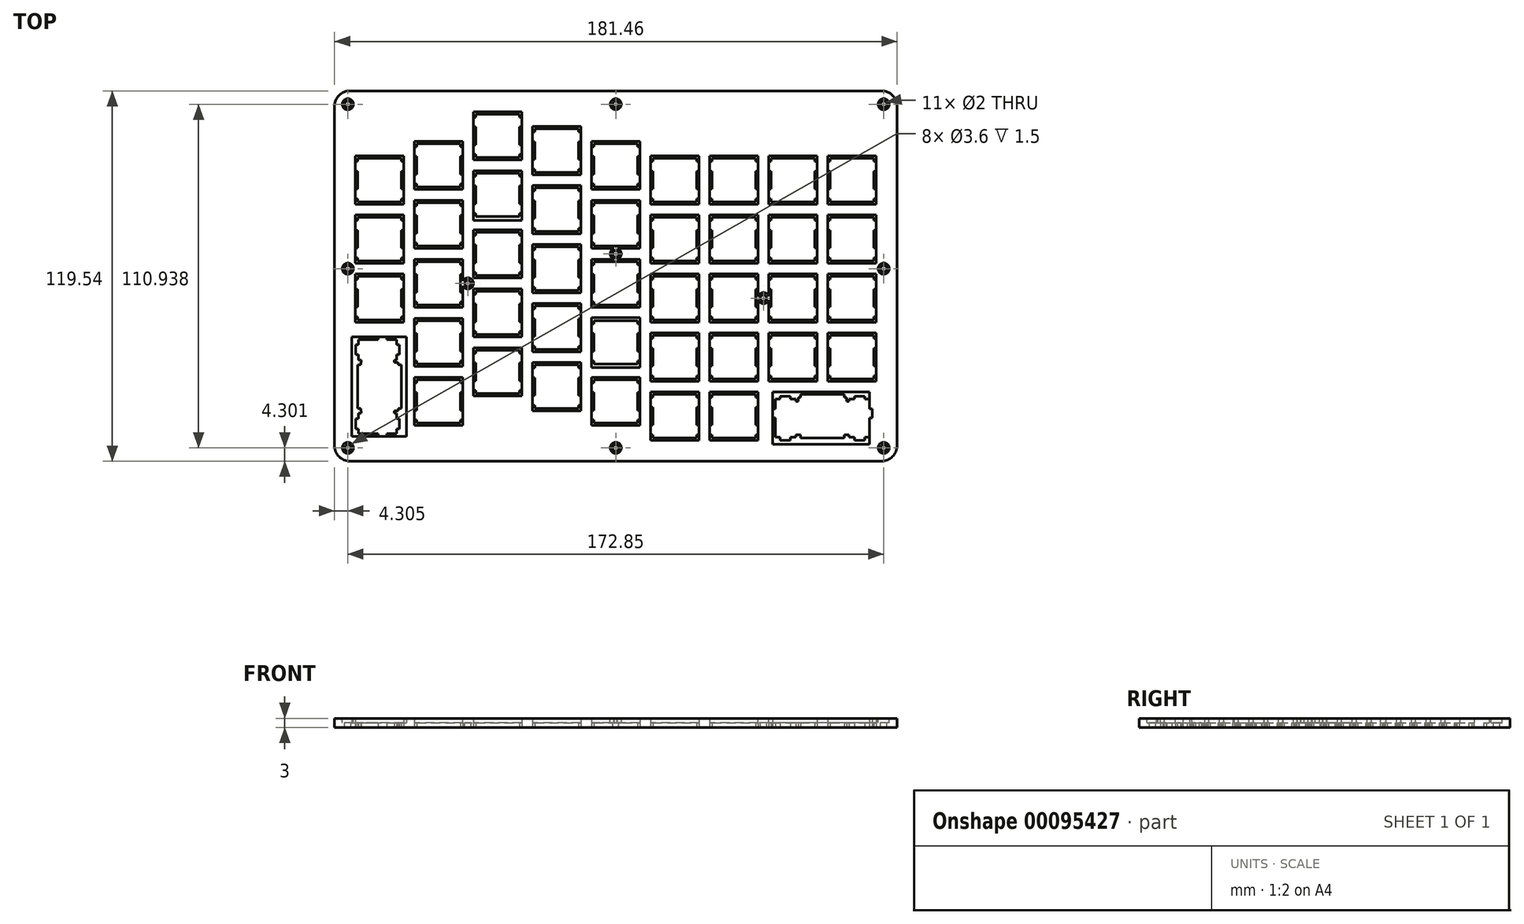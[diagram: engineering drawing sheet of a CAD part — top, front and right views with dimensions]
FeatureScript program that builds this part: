
annotation { "Feature Type Name" : "Feature", "Feature Type Description" : "" }
export const myFeature = defineFeature(function(context is Context, id is Id, definition is map)
    precondition{}
    {
        {
            var Q0;
            Q0=qCreatedBy(makeId("Top.planeOp"),FACE);
            var sketch = newSketch(context, id + "F0", { "sketchPlane" : qUnion([Q0])});
            skLineSegment(sketch, "E0", {"start": v(-90.73, 59.77) * mm, "end": v(90.73, 59.77) * mm});
            skLineSegment(sketch, "E1", {"start": v(90.73, 59.77) * mm, "end": v(90.73, -59.77) * mm});
            skLineSegment(sketch, "E2", {"start": v(90.73, -59.77) * mm, "end": v(-90.73, -59.77) * mm});
            skLineSegment(sketch, "E3", {"start": v(-90.73, -59.77) * mm, "end": v(-90.73, 59.77) * mm});
            skLineSegment(sketch, "E4", {"start": v(-70.2, -42.72) * mm, "end": v(-70.2, -43.52) * mm});
            skLineSegment(sketch, "E5", {"start": v(-70.2, -43.52) * mm, "end": v(-71.47, -43.52) * mm});
            skLineSegment(sketch, "E6", {"start": v(-71.47, -43.52) * mm, "end": v(-71.47, -44.3) * mm});
            skLineSegment(sketch, "E7", {"start": v(-71.47, -44.3) * mm, "end": v(-70.67, -44.3) * mm});
            skLineSegment(sketch, "E8", {"start": v(-70.67, -44.3) * mm, "end": v(-70.67, -46.02) * mm});
            skLineSegment(sketch, "E9", {"start": v(-70.67, -46.02) * mm, "end": v(-69.75, -46.02) * mm});
            skLineSegment(sketch, "E10", {"start": v(-69.75, -46.02) * mm, "end": v(-69.75, -49.32) * mm});
            skLineSegment(sketch, "E11", {"start": v(-69.75, -49.32) * mm, "end": v(-70.67, -49.32) * mm});
            skLineSegment(sketch, "E12", {"start": v(-70.67, -49.32) * mm, "end": v(-70.67, -50.94) * mm});
            skLineSegment(sketch, "E13", {"start": v(-70.67, -50.94) * mm, "end": v(-73.9, -50.94) * mm});
            skLineSegment(sketch, "E14", {"start": v(-73.9, -50.94) * mm, "end": v(-73.9, -51.82) * mm});
            skLineSegment(sketch, "E15", {"start": v(-73.9, -51.82) * mm, "end": v(-76.7, -51.82) * mm});
            skLineSegment(sketch, "E16", {"start": v(-76.7, -51.82) * mm, "end": v(-76.7, -50.94) * mm});
            skLineSegment(sketch, "E17", {"start": v(-76.7, -50.94) * mm, "end": v(-82.97, -50.94) * mm});
            skLineSegment(sketch, "E18", {"start": v(-82.97, -50.94) * mm, "end": v(-82.97, -49.32) * mm});
            skLineSegment(sketch, "E19", {"start": v(-82.97, -49.32) * mm, "end": v(-83.95, -49.32) * mm});
            skLineSegment(sketch, "E20", {"start": v(-83.95, -49.32) * mm, "end": v(-83.95, -46.02) * mm});
            skLineSegment(sketch, "E21", {"start": v(-83.95, -46.02) * mm, "end": v(-82.97, -46.02) * mm});
            skLineSegment(sketch, "E22", {"start": v(-82.97, -46.02) * mm, "end": v(-82.97, -44.3) * mm});
            skLineSegment(sketch, "E23", {"start": v(-82.97, -44.3) * mm, "end": v(-82.17, -44.3) * mm});
            skLineSegment(sketch, "E24", {"start": v(-82.17, -44.3) * mm, "end": v(-82.17, -43.52) * mm});
            skLineSegment(sketch, "E25", {"start": v(-82.17, -43.52) * mm, "end": v(-82.2, -43.52) * mm});
            skLineSegment(sketch, "E26", {"start": v(-82.2, -43.52) * mm, "end": v(-82.2, -42.72) * mm});
            skLineSegment(sketch, "E27", {"start": v(-82.2, -42.72) * mm, "end": v(-83.2, -42.72) * mm});
            skLineSegment(sketch, "E28", {"start": v(-83.2, -42.72) * mm, "end": v(-83.2, -28.72) * mm});
            skLineSegment(sketch, "E29", {"start": v(-83.2, -28.72) * mm, "end": v(-82.2, -28.72) * mm});
            skLineSegment(sketch, "E30", {"start": v(-82.2, -28.72) * mm, "end": v(-82.2, -27.92) * mm});
            skLineSegment(sketch, "E31", {"start": v(-82.2, -27.92) * mm, "end": v(-82.17, -27.92) * mm});
            skLineSegment(sketch, "E32", {"start": v(-82.17, -27.92) * mm, "end": v(-82.17, -27.14) * mm});
            skLineSegment(sketch, "E33", {"start": v(-82.17, -27.14) * mm, "end": v(-82.97, -27.14) * mm});
            skLineSegment(sketch, "E34", {"start": v(-82.97, -27.14) * mm, "end": v(-82.97, -25.42) * mm});
            skLineSegment(sketch, "E35", {"start": v(-82.97, -25.42) * mm, "end": v(-83.95, -25.42) * mm});
            skLineSegment(sketch, "E36", {"start": v(-83.95, -25.42) * mm, "end": v(-83.95, -22.12) * mm});
            skLineSegment(sketch, "E37", {"start": v(-83.95, -22.12) * mm, "end": v(-82.97, -22.12) * mm});
            skLineSegment(sketch, "E38", {"start": v(-82.97, -22.12) * mm, "end": v(-82.97, -20.5) * mm});
            skLineSegment(sketch, "E39", {"start": v(-82.97, -20.5) * mm, "end": v(-76.7, -20.5) * mm});
            skLineSegment(sketch, "E40", {"start": v(-76.7, -20.5) * mm, "end": v(-76.7, -19.62) * mm});
            skLineSegment(sketch, "E41", {"start": v(-76.7, -19.62) * mm, "end": v(-73.9, -19.62) * mm});
            skLineSegment(sketch, "E42", {"start": v(-73.9, -19.62) * mm, "end": v(-73.9, -20.5) * mm});
            skLineSegment(sketch, "E43", {"start": v(-73.9, -20.5) * mm, "end": v(-70.67, -20.5) * mm});
            skLineSegment(sketch, "E44", {"start": v(-70.67, -20.5) * mm, "end": v(-70.67, -22.12) * mm});
            skLineSegment(sketch, "E45", {"start": v(-70.67, -22.12) * mm, "end": v(-69.75, -22.12) * mm});
            skLineSegment(sketch, "E46", {"start": v(-69.75, -22.12) * mm, "end": v(-69.75, -25.42) * mm});
            skLineSegment(sketch, "E47", {"start": v(-69.75, -25.42) * mm, "end": v(-70.67, -25.42) * mm});
            skLineSegment(sketch, "E48", {"start": v(-70.67, -25.42) * mm, "end": v(-70.67, -27.14) * mm});
            skLineSegment(sketch, "E49", {"start": v(-70.67, -27.14) * mm, "end": v(-71.47, -27.14) * mm});
            skLineSegment(sketch, "E50", {"start": v(-71.47, -27.14) * mm, "end": v(-71.47, -27.92) * mm});
            skLineSegment(sketch, "E51", {"start": v(-71.47, -27.92) * mm, "end": v(-70.2, -27.92) * mm});
            skLineSegment(sketch, "E52", {"start": v(-70.2, -27.92) * mm, "end": v(-70.2, -28.72) * mm});
            skLineSegment(sketch, "E53", {"start": v(-70.2, -28.72) * mm, "end": v(-69.2, -28.72) * mm});
            skLineSegment(sketch, "E54", {"start": v(-69.2, -28.72) * mm, "end": v(-69.2, -42.72) * mm});
            skLineSegment(sketch, "E55", {"start": v(-69.2, -42.72) * mm, "end": v(-70.2, -42.72) * mm});
            skLineSegment(sketch, "E56", {"start": v(-69.2, 24.96) * mm, "end": v(-69.2, 23.96) * mm});
            skLineSegment(sketch, "E57", {"start": v(-69.2, 23.96) * mm, "end": v(-83.2, 23.96) * mm});
            skLineSegment(sketch, "E58", {"start": v(-83.2, 23.96) * mm, "end": v(-83.2, 24.96) * mm});
            skLineSegment(sketch, "E59", {"start": v(-83.2, 24.96) * mm, "end": v(-84, 24.96) * mm});
            skLineSegment(sketch, "E60", {"start": v(-84, 24.96) * mm, "end": v(-84, 28.06) * mm});
            skLineSegment(sketch, "E61", {"start": v(-84, 28.06) * mm, "end": v(-83.2, 28.06) * mm});
            skLineSegment(sketch, "E62", {"start": v(-83.2, 28.06) * mm, "end": v(-83.2, 33.86) * mm});
            skLineSegment(sketch, "E63", {"start": v(-83.2, 33.86) * mm, "end": v(-84, 33.86) * mm});
            skLineSegment(sketch, "E64", {"start": v(-84, 33.86) * mm, "end": v(-84, 36.96) * mm});
            skLineSegment(sketch, "E65", {"start": v(-84, 36.96) * mm, "end": v(-83.2, 36.96) * mm});
            skLineSegment(sketch, "E66", {"start": v(-83.2, 36.96) * mm, "end": v(-83.2, 37.96) * mm});
            skLineSegment(sketch, "E67", {"start": v(-83.2, 37.96) * mm, "end": v(-69.2, 37.96) * mm});
            skLineSegment(sketch, "E68", {"start": v(-69.2, 37.96) * mm, "end": v(-69.2, 36.96) * mm});
            skLineSegment(sketch, "E69", {"start": v(-69.2, 36.96) * mm, "end": v(-68.4, 36.96) * mm});
            skLineSegment(sketch, "E70", {"start": v(-68.4, 36.96) * mm, "end": v(-68.4, 33.86) * mm});
            skLineSegment(sketch, "E71", {"start": v(-68.4, 33.86) * mm, "end": v(-69.2, 33.86) * mm});
            skLineSegment(sketch, "E72", {"start": v(-69.2, 33.86) * mm, "end": v(-69.2, 28.06) * mm});
            skLineSegment(sketch, "E73", {"start": v(-69.2, 28.06) * mm, "end": v(-68.4, 28.06) * mm});
            skLineSegment(sketch, "E74", {"start": v(-68.4, 28.06) * mm, "end": v(-68.4, 24.96) * mm});
            skLineSegment(sketch, "E75", {"start": v(-68.4, 24.96) * mm, "end": v(-69.2, 24.96) * mm});
            skLineSegment(sketch, "E76", {"start": v(-69.2, 5.9) * mm, "end": v(-69.2, 4.9) * mm});
            skLineSegment(sketch, "E77", {"start": v(-69.2, 4.9) * mm, "end": v(-83.2, 4.9) * mm});
            skLineSegment(sketch, "E78", {"start": v(-83.2, 4.9) * mm, "end": v(-83.2, 5.9) * mm});
            skLineSegment(sketch, "E79", {"start": v(-83.2, 5.9) * mm, "end": v(-84, 5.9) * mm});
            skLineSegment(sketch, "E80", {"start": v(-84, 5.9) * mm, "end": v(-84, 9) * mm});
            skLineSegment(sketch, "E81", {"start": v(-84, 9) * mm, "end": v(-83.2, 9) * mm});
            skLineSegment(sketch, "E82", {"start": v(-83.2, 9) * mm, "end": v(-83.2, 14.8) * mm});
            skLineSegment(sketch, "E83", {"start": v(-83.2, 14.8) * mm, "end": v(-84, 14.8) * mm});
            skLineSegment(sketch, "E84", {"start": v(-84, 14.8) * mm, "end": v(-84, 17.9) * mm});
            skLineSegment(sketch, "E85", {"start": v(-84, 17.9) * mm, "end": v(-83.2, 17.9) * mm});
            skLineSegment(sketch, "E86", {"start": v(-83.2, 17.9) * mm, "end": v(-83.2, 18.9) * mm});
            skLineSegment(sketch, "E87", {"start": v(-83.2, 18.9) * mm, "end": v(-69.2, 18.9) * mm});
            skLineSegment(sketch, "E88", {"start": v(-69.2, 18.9) * mm, "end": v(-69.2, 17.9) * mm});
            skLineSegment(sketch, "E89", {"start": v(-69.2, 17.9) * mm, "end": v(-68.4, 17.9) * mm});
            skLineSegment(sketch, "E90", {"start": v(-68.4, 17.9) * mm, "end": v(-68.4, 14.8) * mm});
            skLineSegment(sketch, "E91", {"start": v(-68.4, 14.8) * mm, "end": v(-69.2, 14.8) * mm});
            skLineSegment(sketch, "E92", {"start": v(-69.2, 14.8) * mm, "end": v(-69.2, 9) * mm});
            skLineSegment(sketch, "E93", {"start": v(-69.2, 9) * mm, "end": v(-68.4, 9) * mm});
            skLineSegment(sketch, "E94", {"start": v(-68.4, 9) * mm, "end": v(-68.4, 5.9) * mm});
            skLineSegment(sketch, "E95", {"start": v(-68.4, 5.9) * mm, "end": v(-69.2, 5.9) * mm});
            skLineSegment(sketch, "E96", {"start": v(-69.2, -13.14) * mm, "end": v(-69.2, -14.14) * mm});
            skLineSegment(sketch, "E97", {"start": v(-69.2, -14.14) * mm, "end": v(-83.2, -14.14) * mm});
            skLineSegment(sketch, "E98", {"start": v(-83.2, -14.14) * mm, "end": v(-83.2, -13.14) * mm});
            skLineSegment(sketch, "E99", {"start": v(-83.2, -13.14) * mm, "end": v(-84, -13.14) * mm});
            skLineSegment(sketch, "E100", {"start": v(-84, -13.14) * mm, "end": v(-84, -10.04) * mm});
            skLineSegment(sketch, "E101", {"start": v(-84, -10.04) * mm, "end": v(-83.2, -10.04) * mm});
            skLineSegment(sketch, "E102", {"start": v(-83.2, -10.04) * mm, "end": v(-83.2, -4.24) * mm});
            skLineSegment(sketch, "E103", {"start": v(-83.2, -4.24) * mm, "end": v(-84, -4.24) * mm});
            skLineSegment(sketch, "E104", {"start": v(-84, -4.24) * mm, "end": v(-84, -1.14) * mm});
            skLineSegment(sketch, "E105", {"start": v(-84, -1.14) * mm, "end": v(-83.2, -1.14) * mm});
            skLineSegment(sketch, "E106", {"start": v(-83.2, -1.14) * mm, "end": v(-83.2, -0.14) * mm});
            skLineSegment(sketch, "E107", {"start": v(-83.2, -0.14) * mm, "end": v(-69.2, -0.14) * mm});
            skLineSegment(sketch, "E108", {"start": v(-69.2, -0.14) * mm, "end": v(-69.2, -1.14) * mm});
            skLineSegment(sketch, "E109", {"start": v(-69.2, -1.14) * mm, "end": v(-68.4, -1.14) * mm});
            skLineSegment(sketch, "E110", {"start": v(-68.4, -1.14) * mm, "end": v(-68.4, -4.24) * mm});
            skLineSegment(sketch, "E111", {"start": v(-68.4, -4.24) * mm, "end": v(-69.2, -4.24) * mm});
            skLineSegment(sketch, "E112", {"start": v(-69.2, -4.24) * mm, "end": v(-69.2, -10.04) * mm});
            skLineSegment(sketch, "E113", {"start": v(-69.2, -10.04) * mm, "end": v(-68.4, -10.04) * mm});
            skLineSegment(sketch, "E114", {"start": v(-68.4, -10.04) * mm, "end": v(-68.4, -13.14) * mm});
            skLineSegment(sketch, "E115", {"start": v(-68.4, -13.14) * mm, "end": v(-69.2, -13.14) * mm});
            skLineSegment(sketch, "E116", {"start": v(-50.15, 29.72) * mm, "end": v(-50.15, 28.72) * mm});
            skLineSegment(sketch, "E117", {"start": v(-50.15, 28.72) * mm, "end": v(-64.15, 28.72) * mm});
            skLineSegment(sketch, "E118", {"start": v(-64.15, 28.72) * mm, "end": v(-64.15, 29.72) * mm});
            skLineSegment(sketch, "E119", {"start": v(-64.15, 29.72) * mm, "end": v(-64.95, 29.72) * mm});
            skLineSegment(sketch, "E120", {"start": v(-64.95, 29.72) * mm, "end": v(-64.95, 32.82) * mm});
            skLineSegment(sketch, "E121", {"start": v(-64.95, 32.82) * mm, "end": v(-64.15, 32.82) * mm});
            skLineSegment(sketch, "E122", {"start": v(-64.15, 32.82) * mm, "end": v(-64.15, 38.62) * mm});
            skLineSegment(sketch, "E123", {"start": v(-64.15, 38.62) * mm, "end": v(-64.95, 38.62) * mm});
            skLineSegment(sketch, "E124", {"start": v(-64.95, 38.62) * mm, "end": v(-64.95, 41.72) * mm});
            skLineSegment(sketch, "E125", {"start": v(-64.95, 41.72) * mm, "end": v(-64.15, 41.72) * mm});
            skLineSegment(sketch, "E126", {"start": v(-64.15, 41.72) * mm, "end": v(-64.15, 42.72) * mm});
            skLineSegment(sketch, "E127", {"start": v(-64.15, 42.72) * mm, "end": v(-50.15, 42.72) * mm});
            skLineSegment(sketch, "E128", {"start": v(-50.15, 42.72) * mm, "end": v(-50.15, 41.72) * mm});
            skLineSegment(sketch, "E129", {"start": v(-50.15, 41.72) * mm, "end": v(-49.35, 41.72) * mm});
            skLineSegment(sketch, "E130", {"start": v(-49.35, 41.72) * mm, "end": v(-49.35, 38.62) * mm});
            skLineSegment(sketch, "E131", {"start": v(-49.35, 38.62) * mm, "end": v(-50.15, 38.62) * mm});
            skLineSegment(sketch, "E132", {"start": v(-50.15, 38.62) * mm, "end": v(-50.15, 32.82) * mm});
            skLineSegment(sketch, "E133", {"start": v(-50.15, 32.82) * mm, "end": v(-49.35, 32.82) * mm});
            skLineSegment(sketch, "E134", {"start": v(-49.35, 32.82) * mm, "end": v(-49.35, 29.72) * mm});
            skLineSegment(sketch, "E135", {"start": v(-49.35, 29.72) * mm, "end": v(-50.15, 29.72) * mm});
            skLineSegment(sketch, "E136", {"start": v(-50.15, 10.67) * mm, "end": v(-50.15, 9.67) * mm});
            skLineSegment(sketch, "E137", {"start": v(-50.15, 9.67) * mm, "end": v(-64.15, 9.67) * mm});
            skLineSegment(sketch, "E138", {"start": v(-64.15, 9.67) * mm, "end": v(-64.15, 10.67) * mm});
            skLineSegment(sketch, "E139", {"start": v(-64.15, 10.67) * mm, "end": v(-64.95, 10.67) * mm});
            skLineSegment(sketch, "E140", {"start": v(-64.95, 10.67) * mm, "end": v(-64.95, 13.77) * mm});
            skLineSegment(sketch, "E141", {"start": v(-64.95, 13.77) * mm, "end": v(-64.15, 13.77) * mm});
            skLineSegment(sketch, "E142", {"start": v(-64.15, 13.77) * mm, "end": v(-64.15, 19.57) * mm});
            skLineSegment(sketch, "E143", {"start": v(-64.15, 19.57) * mm, "end": v(-64.95, 19.57) * mm});
            skLineSegment(sketch, "E144", {"start": v(-64.95, 19.57) * mm, "end": v(-64.95, 22.67) * mm});
            skLineSegment(sketch, "E145", {"start": v(-64.95, 22.67) * mm, "end": v(-64.15, 22.67) * mm});
            skLineSegment(sketch, "E146", {"start": v(-64.15, 22.67) * mm, "end": v(-64.15, 23.67) * mm});
            skLineSegment(sketch, "E147", {"start": v(-64.15, 23.67) * mm, "end": v(-50.15, 23.67) * mm});
            skLineSegment(sketch, "E148", {"start": v(-50.15, 23.67) * mm, "end": v(-50.15, 22.67) * mm});
            skLineSegment(sketch, "E149", {"start": v(-50.15, 22.67) * mm, "end": v(-49.35, 22.67) * mm});
            skLineSegment(sketch, "E150", {"start": v(-49.35, 22.67) * mm, "end": v(-49.35, 19.57) * mm});
            skLineSegment(sketch, "E151", {"start": v(-49.35, 19.57) * mm, "end": v(-50.15, 19.57) * mm});
            skLineSegment(sketch, "E152", {"start": v(-50.15, 19.57) * mm, "end": v(-50.15, 13.77) * mm});
            skLineSegment(sketch, "E153", {"start": v(-50.15, 13.77) * mm, "end": v(-49.35, 13.77) * mm});
            skLineSegment(sketch, "E154", {"start": v(-49.35, 13.77) * mm, "end": v(-49.35, 10.67) * mm});
            skLineSegment(sketch, "E155", {"start": v(-49.35, 10.67) * mm, "end": v(-50.15, 10.67) * mm});
            skLineSegment(sketch, "E156", {"start": v(-50.15, -8.38) * mm, "end": v(-50.15, -9.38) * mm});
            skLineSegment(sketch, "E157", {"start": v(-50.15, -9.38) * mm, "end": v(-64.15, -9.38) * mm});
            skLineSegment(sketch, "E158", {"start": v(-64.15, -9.38) * mm, "end": v(-64.15, -8.38) * mm});
            skLineSegment(sketch, "E159", {"start": v(-64.15, -8.38) * mm, "end": v(-64.95, -8.38) * mm});
            skLineSegment(sketch, "E160", {"start": v(-64.95, -8.38) * mm, "end": v(-64.95, -5.28) * mm});
            skLineSegment(sketch, "E161", {"start": v(-64.95, -5.28) * mm, "end": v(-64.15, -5.28) * mm});
            skLineSegment(sketch, "E162", {"start": v(-64.15, -5.28) * mm, "end": v(-64.15, 0.52) * mm});
            skLineSegment(sketch, "E163", {"start": v(-64.15, 0.52) * mm, "end": v(-64.95, 0.52) * mm});
            skLineSegment(sketch, "E164", {"start": v(-64.95, 0.52) * mm, "end": v(-64.95, 3.62) * mm});
            skLineSegment(sketch, "E165", {"start": v(-64.95, 3.62) * mm, "end": v(-64.15, 3.62) * mm});
            skLineSegment(sketch, "E166", {"start": v(-64.15, 3.62) * mm, "end": v(-64.15, 4.62) * mm});
            skLineSegment(sketch, "E167", {"start": v(-64.15, 4.62) * mm, "end": v(-50.15, 4.62) * mm});
            skLineSegment(sketch, "E168", {"start": v(-50.15, 4.62) * mm, "end": v(-50.15, 3.62) * mm});
            skLineSegment(sketch, "E169", {"start": v(-50.15, 3.62) * mm, "end": v(-49.35, 3.62) * mm});
            skLineSegment(sketch, "E170", {"start": v(-49.35, 3.62) * mm, "end": v(-49.35, 0.52) * mm});
            skLineSegment(sketch, "E171", {"start": v(-49.35, 0.52) * mm, "end": v(-50.15, 0.52) * mm});
            skLineSegment(sketch, "E172", {"start": v(-50.15, 0.52) * mm, "end": v(-50.15, -5.28) * mm});
            skLineSegment(sketch, "E173", {"start": v(-50.15, -5.28) * mm, "end": v(-49.35, -5.28) * mm});
            skLineSegment(sketch, "E174", {"start": v(-49.35, -5.28) * mm, "end": v(-49.35, -8.38) * mm});
            skLineSegment(sketch, "E175", {"start": v(-49.35, -8.38) * mm, "end": v(-50.15, -8.38) * mm});
            skLineSegment(sketch, "E176", {"start": v(-50.15, -27.43) * mm, "end": v(-50.15, -28.43) * mm});
            skLineSegment(sketch, "E177", {"start": v(-50.15, -28.43) * mm, "end": v(-64.15, -28.43) * mm});
            skLineSegment(sketch, "E178", {"start": v(-64.15, -28.43) * mm, "end": v(-64.15, -27.43) * mm});
            skLineSegment(sketch, "E179", {"start": v(-64.15, -27.43) * mm, "end": v(-64.95, -27.43) * mm});
            skLineSegment(sketch, "E180", {"start": v(-64.95, -27.43) * mm, "end": v(-64.95, -24.33) * mm});
            skLineSegment(sketch, "E181", {"start": v(-64.95, -24.33) * mm, "end": v(-64.15, -24.33) * mm});
            skLineSegment(sketch, "E182", {"start": v(-64.15, -24.33) * mm, "end": v(-64.15, -18.53) * mm});
            skLineSegment(sketch, "E183", {"start": v(-64.15, -18.53) * mm, "end": v(-64.95, -18.53) * mm});
            skLineSegment(sketch, "E184", {"start": v(-64.95, -18.53) * mm, "end": v(-64.95, -15.43) * mm});
            skLineSegment(sketch, "E185", {"start": v(-64.95, -15.43) * mm, "end": v(-64.15, -15.43) * mm});
            skLineSegment(sketch, "E186", {"start": v(-64.15, -15.43) * mm, "end": v(-64.15, -14.43) * mm});
            skLineSegment(sketch, "E187", {"start": v(-64.15, -14.43) * mm, "end": v(-50.15, -14.43) * mm});
            skLineSegment(sketch, "E188", {"start": v(-50.15, -14.43) * mm, "end": v(-50.15, -15.43) * mm});
            skLineSegment(sketch, "E189", {"start": v(-50.15, -15.43) * mm, "end": v(-49.35, -15.43) * mm});
            skLineSegment(sketch, "E190", {"start": v(-49.35, -15.43) * mm, "end": v(-49.35, -18.53) * mm});
            skLineSegment(sketch, "E191", {"start": v(-49.35, -18.53) * mm, "end": v(-50.15, -18.53) * mm});
            skLineSegment(sketch, "E192", {"start": v(-50.15, -18.53) * mm, "end": v(-50.15, -24.33) * mm});
            skLineSegment(sketch, "E193", {"start": v(-50.15, -24.33) * mm, "end": v(-49.35, -24.33) * mm});
            skLineSegment(sketch, "E194", {"start": v(-49.35, -24.33) * mm, "end": v(-49.35, -27.43) * mm});
            skLineSegment(sketch, "E195", {"start": v(-49.35, -27.43) * mm, "end": v(-50.15, -27.43) * mm});
            skLineSegment(sketch, "E196", {"start": v(-50.15, -46.48) * mm, "end": v(-50.15, -47.48) * mm});
            skLineSegment(sketch, "E197", {"start": v(-50.15, -47.48) * mm, "end": v(-64.15, -47.48) * mm});
            skLineSegment(sketch, "E198", {"start": v(-64.15, -47.48) * mm, "end": v(-64.15, -46.48) * mm});
            skLineSegment(sketch, "E199", {"start": v(-64.15, -46.48) * mm, "end": v(-64.95, -46.48) * mm});
            skLineSegment(sketch, "E200", {"start": v(-64.95, -46.48) * mm, "end": v(-64.95, -43.38) * mm});
            skLineSegment(sketch, "E201", {"start": v(-64.95, -43.38) * mm, "end": v(-64.15, -43.38) * mm});
            skLineSegment(sketch, "E202", {"start": v(-64.15, -43.38) * mm, "end": v(-64.15, -37.58) * mm});
            skLineSegment(sketch, "E203", {"start": v(-64.15, -37.58) * mm, "end": v(-64.95, -37.58) * mm});
            skLineSegment(sketch, "E204", {"start": v(-64.95, -37.58) * mm, "end": v(-64.95, -34.48) * mm});
            skLineSegment(sketch, "E205", {"start": v(-64.95, -34.48) * mm, "end": v(-64.15, -34.48) * mm});
            skLineSegment(sketch, "E206", {"start": v(-64.15, -34.48) * mm, "end": v(-64.15, -33.48) * mm});
            skLineSegment(sketch, "E207", {"start": v(-64.15, -33.48) * mm, "end": v(-50.15, -33.48) * mm});
            skLineSegment(sketch, "E208", {"start": v(-50.15, -33.48) * mm, "end": v(-50.15, -34.48) * mm});
            skLineSegment(sketch, "E209", {"start": v(-50.15, -34.48) * mm, "end": v(-49.35, -34.48) * mm});
            skLineSegment(sketch, "E210", {"start": v(-49.35, -34.48) * mm, "end": v(-49.35, -37.58) * mm});
            skLineSegment(sketch, "E211", {"start": v(-49.35, -37.58) * mm, "end": v(-50.15, -37.58) * mm});
            skLineSegment(sketch, "E212", {"start": v(-50.15, -37.58) * mm, "end": v(-50.15, -43.38) * mm});
            skLineSegment(sketch, "E213", {"start": v(-50.15, -43.38) * mm, "end": v(-49.35, -43.38) * mm});
            skLineSegment(sketch, "E214", {"start": v(-49.35, -43.38) * mm, "end": v(-49.35, -46.48) * mm});
            skLineSegment(sketch, "E215", {"start": v(-49.35, -46.48) * mm, "end": v(-50.15, -46.48) * mm});
            skLineSegment(sketch, "E216", {"start": v(-31.1, 39.24) * mm, "end": v(-31.1, 38.24) * mm});
            skLineSegment(sketch, "E217", {"start": v(-31.1, 38.24) * mm, "end": v(-45.1, 38.24) * mm});
            skLineSegment(sketch, "E218", {"start": v(-45.1, 38.24) * mm, "end": v(-45.1, 39.24) * mm});
            skLineSegment(sketch, "E219", {"start": v(-45.1, 39.24) * mm, "end": v(-45.9, 39.24) * mm});
            skLineSegment(sketch, "E220", {"start": v(-45.9, 39.24) * mm, "end": v(-45.9, 42.34) * mm});
            skLineSegment(sketch, "E221", {"start": v(-45.9, 42.34) * mm, "end": v(-45.1, 42.34) * mm});
            skLineSegment(sketch, "E222", {"start": v(-45.1, 42.34) * mm, "end": v(-45.1, 48.14) * mm});
            skLineSegment(sketch, "E223", {"start": v(-45.1, 48.14) * mm, "end": v(-45.9, 48.14) * mm});
            skLineSegment(sketch, "E224", {"start": v(-45.9, 48.14) * mm, "end": v(-45.9, 51.24) * mm});
            skLineSegment(sketch, "E225", {"start": v(-45.9, 51.24) * mm, "end": v(-45.1, 51.24) * mm});
            skLineSegment(sketch, "E226", {"start": v(-45.1, 51.24) * mm, "end": v(-45.1, 52.24) * mm});
            skLineSegment(sketch, "E227", {"start": v(-45.1, 52.24) * mm, "end": v(-31.1, 52.24) * mm});
            skLineSegment(sketch, "E228", {"start": v(-31.1, 52.24) * mm, "end": v(-31.1, 51.24) * mm});
            skLineSegment(sketch, "E229", {"start": v(-31.1, 51.24) * mm, "end": v(-30.3, 51.24) * mm});
            skLineSegment(sketch, "E230", {"start": v(-30.3, 51.24) * mm, "end": v(-30.3, 48.14) * mm});
            skLineSegment(sketch, "E231", {"start": v(-30.3, 48.14) * mm, "end": v(-31.1, 48.14) * mm});
            skLineSegment(sketch, "E232", {"start": v(-31.1, 48.14) * mm, "end": v(-31.1, 42.34) * mm});
            skLineSegment(sketch, "E233", {"start": v(-31.1, 42.34) * mm, "end": v(-30.3, 42.34) * mm});
            skLineSegment(sketch, "E234", {"start": v(-30.3, 42.34) * mm, "end": v(-30.3, 39.24) * mm});
            skLineSegment(sketch, "E235", {"start": v(-30.3, 39.24) * mm, "end": v(-31.1, 39.24) * mm});
            skLineSegment(sketch, "E236", {"start": v(-31.1, 20.2) * mm, "end": v(-31.1, 19.2) * mm});
            skLineSegment(sketch, "E237", {"start": v(-31.1, 19.2) * mm, "end": v(-45.1, 19.2) * mm});
            skLineSegment(sketch, "E238", {"start": v(-45.1, 19.2) * mm, "end": v(-45.1, 20.2) * mm});
            skLineSegment(sketch, "E239", {"start": v(-45.1, 20.2) * mm, "end": v(-45.9, 20.2) * mm});
            skLineSegment(sketch, "E240", {"start": v(-45.9, 20.2) * mm, "end": v(-45.9, 23.3) * mm});
            skLineSegment(sketch, "E241", {"start": v(-45.9, 23.3) * mm, "end": v(-45.1, 23.3) * mm});
            skLineSegment(sketch, "E242", {"start": v(-45.1, 23.3) * mm, "end": v(-45.1, 29.1) * mm});
            skLineSegment(sketch, "E243", {"start": v(-45.1, 29.1) * mm, "end": v(-45.9, 29.1) * mm});
            skLineSegment(sketch, "E244", {"start": v(-45.9, 29.1) * mm, "end": v(-45.9, 32.2) * mm});
            skLineSegment(sketch, "E245", {"start": v(-45.9, 32.2) * mm, "end": v(-45.1, 32.2) * mm});
            skLineSegment(sketch, "E246", {"start": v(-45.1, 32.2) * mm, "end": v(-45.1, 33.2) * mm});
            skLineSegment(sketch, "E247", {"start": v(-45.1, 33.2) * mm, "end": v(-31.1, 33.2) * mm});
            skLineSegment(sketch, "E248", {"start": v(-31.1, 33.2) * mm, "end": v(-31.1, 32.2) * mm});
            skLineSegment(sketch, "E249", {"start": v(-31.1, 32.2) * mm, "end": v(-30.3, 32.2) * mm});
            skLineSegment(sketch, "E250", {"start": v(-30.3, 32.2) * mm, "end": v(-30.3, 29.1) * mm});
            skLineSegment(sketch, "E251", {"start": v(-30.3, 29.1) * mm, "end": v(-31.1, 29.1) * mm});
            skLineSegment(sketch, "E252", {"start": v(-31.1, 29.1) * mm, "end": v(-31.1, 23.3) * mm});
            skLineSegment(sketch, "E253", {"start": v(-31.1, 23.3) * mm, "end": v(-30.3, 23.3) * mm});
            skLineSegment(sketch, "E254", {"start": v(-30.3, 23.3) * mm, "end": v(-30.3, 20.2) * mm});
            skLineSegment(sketch, "E255", {"start": v(-30.3, 20.2) * mm, "end": v(-31.1, 20.2) * mm});
            skLineSegment(sketch, "E256", {"start": v(-31.1, 1.14) * mm, "end": v(-31.1, 0.14) * mm});
            skLineSegment(sketch, "E257", {"start": v(-31.1, 0.14) * mm, "end": v(-45.1, 0.14) * mm});
            skLineSegment(sketch, "E258", {"start": v(-45.1, 0.14) * mm, "end": v(-45.1, 1.14) * mm});
            skLineSegment(sketch, "E259", {"start": v(-45.1, 1.14) * mm, "end": v(-45.9, 1.14) * mm});
            skLineSegment(sketch, "E260", {"start": v(-45.9, 1.14) * mm, "end": v(-45.9, 4.24) * mm});
            skLineSegment(sketch, "E261", {"start": v(-45.9, 4.24) * mm, "end": v(-45.1, 4.24) * mm});
            skLineSegment(sketch, "E262", {"start": v(-45.1, 4.24) * mm, "end": v(-45.1, 10.04) * mm});
            skLineSegment(sketch, "E263", {"start": v(-45.1, 10.04) * mm, "end": v(-45.9, 10.04) * mm});
            skLineSegment(sketch, "E264", {"start": v(-45.9, 10.04) * mm, "end": v(-45.9, 13.14) * mm});
            skLineSegment(sketch, "E265", {"start": v(-45.9, 13.14) * mm, "end": v(-45.1, 13.14) * mm});
            skLineSegment(sketch, "E266", {"start": v(-45.1, 13.14) * mm, "end": v(-45.1, 14.14) * mm});
            skLineSegment(sketch, "E267", {"start": v(-45.1, 14.14) * mm, "end": v(-31.1, 14.14) * mm});
            skLineSegment(sketch, "E268", {"start": v(-31.1, 14.14) * mm, "end": v(-31.1, 13.14) * mm});
            skLineSegment(sketch, "E269", {"start": v(-31.1, 13.14) * mm, "end": v(-30.3, 13.14) * mm});
            skLineSegment(sketch, "E270", {"start": v(-30.3, 13.14) * mm, "end": v(-30.3, 10.04) * mm});
            skLineSegment(sketch, "E271", {"start": v(-30.3, 10.04) * mm, "end": v(-31.1, 10.04) * mm});
            skLineSegment(sketch, "E272", {"start": v(-31.1, 10.04) * mm, "end": v(-31.1, 4.24) * mm});
            skLineSegment(sketch, "E273", {"start": v(-31.1, 4.24) * mm, "end": v(-30.3, 4.24) * mm});
            skLineSegment(sketch, "E274", {"start": v(-30.3, 4.24) * mm, "end": v(-30.3, 1.14) * mm});
            skLineSegment(sketch, "E275", {"start": v(-30.3, 1.14) * mm, "end": v(-31.1, 1.14) * mm});
            skLineSegment(sketch, "E276", {"start": v(-31.1, -17.9) * mm, "end": v(-31.1, -18.9) * mm});
            skLineSegment(sketch, "E277", {"start": v(-31.1, -18.9) * mm, "end": v(-45.1, -18.9) * mm});
            skLineSegment(sketch, "E278", {"start": v(-45.1, -18.9) * mm, "end": v(-45.1, -17.9) * mm});
            skLineSegment(sketch, "E279", {"start": v(-45.1, -17.9) * mm, "end": v(-45.9, -17.9) * mm});
            skLineSegment(sketch, "E280", {"start": v(-45.9, -17.9) * mm, "end": v(-45.9, -14.8) * mm});
            skLineSegment(sketch, "E281", {"start": v(-45.9, -14.8) * mm, "end": v(-45.1, -14.8) * mm});
            skLineSegment(sketch, "E282", {"start": v(-45.1, -14.8) * mm, "end": v(-45.1, -9) * mm});
            skLineSegment(sketch, "E283", {"start": v(-45.1, -9) * mm, "end": v(-45.9, -9) * mm});
            skLineSegment(sketch, "E284", {"start": v(-45.9, -9) * mm, "end": v(-45.9, -5.9) * mm});
            skLineSegment(sketch, "E285", {"start": v(-45.9, -5.9) * mm, "end": v(-45.1, -5.9) * mm});
            skLineSegment(sketch, "E286", {"start": v(-45.1, -5.9) * mm, "end": v(-45.1, -4.9) * mm});
            skLineSegment(sketch, "E287", {"start": v(-45.1, -4.9) * mm, "end": v(-31.1, -4.9) * mm});
            skLineSegment(sketch, "E288", {"start": v(-31.1, -4.9) * mm, "end": v(-31.1, -5.9) * mm});
            skLineSegment(sketch, "E289", {"start": v(-31.1, -5.9) * mm, "end": v(-30.3, -5.9) * mm});
            skLineSegment(sketch, "E290", {"start": v(-30.3, -5.9) * mm, "end": v(-30.3, -9) * mm});
            skLineSegment(sketch, "E291", {"start": v(-30.3, -9) * mm, "end": v(-31.1, -9) * mm});
            skLineSegment(sketch, "E292", {"start": v(-31.1, -9) * mm, "end": v(-31.1, -14.8) * mm});
            skLineSegment(sketch, "E293", {"start": v(-31.1, -14.8) * mm, "end": v(-30.3, -14.8) * mm});
            skLineSegment(sketch, "E294", {"start": v(-30.3, -14.8) * mm, "end": v(-30.3, -17.9) * mm});
            skLineSegment(sketch, "E295", {"start": v(-30.3, -17.9) * mm, "end": v(-31.1, -17.9) * mm});
            skLineSegment(sketch, "E296", {"start": v(-31.1, -36.96) * mm, "end": v(-31.1, -37.96) * mm});
            skLineSegment(sketch, "E297", {"start": v(-31.1, -37.96) * mm, "end": v(-45.1, -37.96) * mm});
            skLineSegment(sketch, "E298", {"start": v(-45.1, -37.96) * mm, "end": v(-45.1, -36.96) * mm});
            skLineSegment(sketch, "E299", {"start": v(-45.1, -36.96) * mm, "end": v(-45.9, -36.96) * mm});
            skLineSegment(sketch, "E300", {"start": v(-45.9, -36.96) * mm, "end": v(-45.9, -33.86) * mm});
            skLineSegment(sketch, "E301", {"start": v(-45.9, -33.86) * mm, "end": v(-45.1, -33.86) * mm});
            skLineSegment(sketch, "E302", {"start": v(-45.1, -33.86) * mm, "end": v(-45.1, -28.06) * mm});
            skLineSegment(sketch, "E303", {"start": v(-45.1, -28.06) * mm, "end": v(-45.9, -28.06) * mm});
            skLineSegment(sketch, "E304", {"start": v(-45.9, -28.06) * mm, "end": v(-45.9, -24.96) * mm});
            skLineSegment(sketch, "E305", {"start": v(-45.9, -24.96) * mm, "end": v(-45.1, -24.96) * mm});
            skLineSegment(sketch, "E306", {"start": v(-45.1, -24.96) * mm, "end": v(-45.1, -23.96) * mm});
            skLineSegment(sketch, "E307", {"start": v(-45.1, -23.96) * mm, "end": v(-31.1, -23.96) * mm});
            skLineSegment(sketch, "E308", {"start": v(-31.1, -23.96) * mm, "end": v(-31.1, -24.96) * mm});
            skLineSegment(sketch, "E309", {"start": v(-31.1, -24.96) * mm, "end": v(-30.3, -24.96) * mm});
            skLineSegment(sketch, "E310", {"start": v(-30.3, -24.96) * mm, "end": v(-30.3, -28.06) * mm});
            skLineSegment(sketch, "E311", {"start": v(-30.3, -28.06) * mm, "end": v(-31.1, -28.06) * mm});
            skLineSegment(sketch, "E312", {"start": v(-31.1, -28.06) * mm, "end": v(-31.1, -33.86) * mm});
            skLineSegment(sketch, "E313", {"start": v(-31.1, -33.86) * mm, "end": v(-30.3, -33.86) * mm});
            skLineSegment(sketch, "E314", {"start": v(-30.3, -33.86) * mm, "end": v(-30.3, -36.96) * mm});
            skLineSegment(sketch, "E315", {"start": v(-30.3, -36.96) * mm, "end": v(-31.1, -36.96) * mm});
            skLineSegment(sketch, "E316", {"start": v(-12.05, 34.48) * mm, "end": v(-12.05, 33.48) * mm});
            skLineSegment(sketch, "E317", {"start": v(-12.05, 33.48) * mm, "end": v(-26.05, 33.48) * mm});
            skLineSegment(sketch, "E318", {"start": v(-26.05, 33.48) * mm, "end": v(-26.05, 34.48) * mm});
            skLineSegment(sketch, "E319", {"start": v(-26.05, 34.48) * mm, "end": v(-26.85, 34.48) * mm});
            skLineSegment(sketch, "E320", {"start": v(-26.85, 34.48) * mm, "end": v(-26.85, 37.58) * mm});
            skLineSegment(sketch, "E321", {"start": v(-26.85, 37.58) * mm, "end": v(-26.05, 37.58) * mm});
            skLineSegment(sketch, "E322", {"start": v(-26.05, 37.58) * mm, "end": v(-26.05, 43.38) * mm});
            skLineSegment(sketch, "E323", {"start": v(-26.05, 43.38) * mm, "end": v(-26.85, 43.38) * mm});
            skLineSegment(sketch, "E324", {"start": v(-26.85, 43.38) * mm, "end": v(-26.85, 46.48) * mm});
            skLineSegment(sketch, "E325", {"start": v(-26.85, 46.48) * mm, "end": v(-26.05, 46.48) * mm});
            skLineSegment(sketch, "E326", {"start": v(-26.05, 46.48) * mm, "end": v(-26.05, 47.48) * mm});
            skLineSegment(sketch, "E327", {"start": v(-26.05, 47.48) * mm, "end": v(-12.05, 47.48) * mm});
            skLineSegment(sketch, "E328", {"start": v(-12.05, 47.48) * mm, "end": v(-12.05, 46.48) * mm});
            skLineSegment(sketch, "E329", {"start": v(-12.05, 46.48) * mm, "end": v(-11.25, 46.48) * mm});
            skLineSegment(sketch, "E330", {"start": v(-11.25, 46.48) * mm, "end": v(-11.25, 43.38) * mm});
            skLineSegment(sketch, "E331", {"start": v(-11.25, 43.38) * mm, "end": v(-12.05, 43.38) * mm});
            skLineSegment(sketch, "E332", {"start": v(-12.05, 43.38) * mm, "end": v(-12.05, 37.58) * mm});
            skLineSegment(sketch, "E333", {"start": v(-12.05, 37.58) * mm, "end": v(-11.25, 37.58) * mm});
            skLineSegment(sketch, "E334", {"start": v(-11.25, 37.58) * mm, "end": v(-11.25, 34.48) * mm});
            skLineSegment(sketch, "E335", {"start": v(-11.25, 34.48) * mm, "end": v(-12.05, 34.48) * mm});
            skLineSegment(sketch, "E336", {"start": v(-12.05, 15.43) * mm, "end": v(-12.05, 14.43) * mm});
            skLineSegment(sketch, "E337", {"start": v(-12.05, 14.43) * mm, "end": v(-26.05, 14.43) * mm});
            skLineSegment(sketch, "E338", {"start": v(-26.05, 14.43) * mm, "end": v(-26.05, 15.43) * mm});
            skLineSegment(sketch, "E339", {"start": v(-26.05, 15.43) * mm, "end": v(-26.85, 15.43) * mm});
            skLineSegment(sketch, "E340", {"start": v(-26.85, 15.43) * mm, "end": v(-26.85, 18.53) * mm});
            skLineSegment(sketch, "E341", {"start": v(-26.85, 18.53) * mm, "end": v(-26.05, 18.53) * mm});
            skLineSegment(sketch, "E342", {"start": v(-26.05, 18.53) * mm, "end": v(-26.05, 24.33) * mm});
            skLineSegment(sketch, "E343", {"start": v(-26.05, 24.33) * mm, "end": v(-26.85, 24.33) * mm});
            skLineSegment(sketch, "E344", {"start": v(-26.85, 24.33) * mm, "end": v(-26.85, 27.43) * mm});
            skLineSegment(sketch, "E345", {"start": v(-26.85, 27.43) * mm, "end": v(-26.05, 27.43) * mm});
            skLineSegment(sketch, "E346", {"start": v(-26.05, 27.43) * mm, "end": v(-26.05, 28.43) * mm});
            skLineSegment(sketch, "E347", {"start": v(-26.05, 28.43) * mm, "end": v(-12.05, 28.43) * mm});
            skLineSegment(sketch, "E348", {"start": v(-12.05, 28.43) * mm, "end": v(-12.05, 27.43) * mm});
            skLineSegment(sketch, "E349", {"start": v(-12.05, 27.43) * mm, "end": v(-11.25, 27.43) * mm});
            skLineSegment(sketch, "E350", {"start": v(-11.25, 27.43) * mm, "end": v(-11.25, 24.33) * mm});
            skLineSegment(sketch, "E351", {"start": v(-11.25, 24.33) * mm, "end": v(-12.05, 24.33) * mm});
            skLineSegment(sketch, "E352", {"start": v(-12.05, 24.33) * mm, "end": v(-12.05, 18.53) * mm});
            skLineSegment(sketch, "E353", {"start": v(-12.05, 18.53) * mm, "end": v(-11.25, 18.53) * mm});
            skLineSegment(sketch, "E354", {"start": v(-11.25, 18.53) * mm, "end": v(-11.25, 15.43) * mm});
            skLineSegment(sketch, "E355", {"start": v(-11.25, 15.43) * mm, "end": v(-12.05, 15.43) * mm});
            skLineSegment(sketch, "E356", {"start": v(-12.05, -3.62) * mm, "end": v(-12.05, -4.62) * mm});
            skLineSegment(sketch, "E357", {"start": v(-12.05, -4.62) * mm, "end": v(-26.05, -4.62) * mm});
            skLineSegment(sketch, "E358", {"start": v(-26.05, -4.62) * mm, "end": v(-26.05, -3.62) * mm});
            skLineSegment(sketch, "E359", {"start": v(-26.05, -3.62) * mm, "end": v(-26.85, -3.62) * mm});
            skLineSegment(sketch, "E360", {"start": v(-26.85, -3.62) * mm, "end": v(-26.85, -0.52) * mm});
            skLineSegment(sketch, "E361", {"start": v(-26.85, -0.52) * mm, "end": v(-26.05, -0.52) * mm});
            skLineSegment(sketch, "E362", {"start": v(-26.05, -0.52) * mm, "end": v(-26.05, 5.28) * mm});
            skLineSegment(sketch, "E363", {"start": v(-26.05, 5.28) * mm, "end": v(-26.85, 5.28) * mm});
            skLineSegment(sketch, "E364", {"start": v(-26.85, 5.28) * mm, "end": v(-26.85, 8.38) * mm});
            skLineSegment(sketch, "E365", {"start": v(-26.85, 8.38) * mm, "end": v(-26.05, 8.38) * mm});
            skLineSegment(sketch, "E366", {"start": v(-26.05, 8.38) * mm, "end": v(-26.05, 9.38) * mm});
            skLineSegment(sketch, "E367", {"start": v(-26.05, 9.38) * mm, "end": v(-12.05, 9.38) * mm});
            skLineSegment(sketch, "E368", {"start": v(-12.05, 9.38) * mm, "end": v(-12.05, 8.38) * mm});
            skLineSegment(sketch, "E369", {"start": v(-12.05, 8.38) * mm, "end": v(-11.25, 8.38) * mm});
            skLineSegment(sketch, "E370", {"start": v(-11.25, 8.38) * mm, "end": v(-11.25, 5.28) * mm});
            skLineSegment(sketch, "E371", {"start": v(-11.25, 5.28) * mm, "end": v(-12.05, 5.28) * mm});
            skLineSegment(sketch, "E372", {"start": v(-12.05, 5.28) * mm, "end": v(-12.05, -0.52) * mm});
            skLineSegment(sketch, "E373", {"start": v(-12.05, -0.52) * mm, "end": v(-11.25, -0.52) * mm});
            skLineSegment(sketch, "E374", {"start": v(-11.25, -0.52) * mm, "end": v(-11.25, -3.62) * mm});
            skLineSegment(sketch, "E375", {"start": v(-11.25, -3.62) * mm, "end": v(-12.05, -3.62) * mm});
            skLineSegment(sketch, "E376", {"start": v(-12.05, -22.67) * mm, "end": v(-12.05, -23.67) * mm});
            skLineSegment(sketch, "E377", {"start": v(-12.05, -23.67) * mm, "end": v(-26.05, -23.67) * mm});
            skLineSegment(sketch, "E378", {"start": v(-26.05, -23.67) * mm, "end": v(-26.05, -22.67) * mm});
            skLineSegment(sketch, "E379", {"start": v(-26.05, -22.67) * mm, "end": v(-26.85, -22.67) * mm});
            skLineSegment(sketch, "E380", {"start": v(-26.85, -22.67) * mm, "end": v(-26.85, -19.57) * mm});
            skLineSegment(sketch, "E381", {"start": v(-26.85, -19.57) * mm, "end": v(-26.05, -19.57) * mm});
            skLineSegment(sketch, "E382", {"start": v(-26.05, -19.57) * mm, "end": v(-26.05, -13.77) * mm});
            skLineSegment(sketch, "E383", {"start": v(-26.05, -13.77) * mm, "end": v(-26.85, -13.77) * mm});
            skLineSegment(sketch, "E384", {"start": v(-26.85, -13.77) * mm, "end": v(-26.85, -10.67) * mm});
            skLineSegment(sketch, "E385", {"start": v(-26.85, -10.67) * mm, "end": v(-26.05, -10.67) * mm});
            skLineSegment(sketch, "E386", {"start": v(-26.05, -10.67) * mm, "end": v(-26.05, -9.67) * mm});
            skLineSegment(sketch, "E387", {"start": v(-26.05, -9.67) * mm, "end": v(-12.05, -9.67) * mm});
            skLineSegment(sketch, "E388", {"start": v(-12.05, -9.67) * mm, "end": v(-12.05, -10.67) * mm});
            skLineSegment(sketch, "E389", {"start": v(-12.05, -10.67) * mm, "end": v(-11.25, -10.67) * mm});
            skLineSegment(sketch, "E390", {"start": v(-11.25, -10.67) * mm, "end": v(-11.25, -13.77) * mm});
            skLineSegment(sketch, "E391", {"start": v(-11.25, -13.77) * mm, "end": v(-12.05, -13.77) * mm});
            skLineSegment(sketch, "E392", {"start": v(-12.05, -13.77) * mm, "end": v(-12.05, -19.57) * mm});
            skLineSegment(sketch, "E393", {"start": v(-12.05, -19.57) * mm, "end": v(-11.25, -19.57) * mm});
            skLineSegment(sketch, "E394", {"start": v(-11.25, -19.57) * mm, "end": v(-11.25, -22.67) * mm});
            skLineSegment(sketch, "E395", {"start": v(-11.25, -22.67) * mm, "end": v(-12.05, -22.67) * mm});
            skLineSegment(sketch, "E396", {"start": v(-12.05, -41.72) * mm, "end": v(-12.05, -42.72) * mm});
            skLineSegment(sketch, "E397", {"start": v(-12.05, -42.72) * mm, "end": v(-26.05, -42.72) * mm});
            skLineSegment(sketch, "E398", {"start": v(-26.05, -42.72) * mm, "end": v(-26.05, -41.72) * mm});
            skLineSegment(sketch, "E399", {"start": v(-26.05, -41.72) * mm, "end": v(-26.85, -41.72) * mm});
            skLineSegment(sketch, "E400", {"start": v(-26.85, -41.72) * mm, "end": v(-26.85, -38.62) * mm});
            skLineSegment(sketch, "E401", {"start": v(-26.85, -38.62) * mm, "end": v(-26.05, -38.62) * mm});
            skLineSegment(sketch, "E402", {"start": v(-26.05, -38.62) * mm, "end": v(-26.05, -32.82) * mm});
            skLineSegment(sketch, "E403", {"start": v(-26.05, -32.82) * mm, "end": v(-26.85, -32.82) * mm});
            skLineSegment(sketch, "E404", {"start": v(-26.85, -32.82) * mm, "end": v(-26.85, -29.72) * mm});
            skLineSegment(sketch, "E405", {"start": v(-26.85, -29.72) * mm, "end": v(-26.05, -29.72) * mm});
            skLineSegment(sketch, "E406", {"start": v(-26.05, -29.72) * mm, "end": v(-26.05, -28.72) * mm});
            skLineSegment(sketch, "E407", {"start": v(-26.05, -28.72) * mm, "end": v(-12.05, -28.72) * mm});
            skLineSegment(sketch, "E408", {"start": v(-12.05, -28.72) * mm, "end": v(-12.05, -29.72) * mm});
            skLineSegment(sketch, "E409", {"start": v(-12.05, -29.72) * mm, "end": v(-11.25, -29.72) * mm});
            skLineSegment(sketch, "E410", {"start": v(-11.25, -29.72) * mm, "end": v(-11.25, -32.82) * mm});
            skLineSegment(sketch, "E411", {"start": v(-11.25, -32.82) * mm, "end": v(-12.05, -32.82) * mm});
            skLineSegment(sketch, "E412", {"start": v(-12.05, -32.82) * mm, "end": v(-12.05, -38.62) * mm});
            skLineSegment(sketch, "E413", {"start": v(-12.05, -38.62) * mm, "end": v(-11.25, -38.62) * mm});
            skLineSegment(sketch, "E414", {"start": v(-11.25, -38.62) * mm, "end": v(-11.25, -41.72) * mm});
            skLineSegment(sketch, "E415", {"start": v(-11.25, -41.72) * mm, "end": v(-12.05, -41.72) * mm});
            skLineSegment(sketch, "E416", {"start": v(7, 29.72) * mm, "end": v(7, 28.72) * mm});
            skLineSegment(sketch, "E417", {"start": v(7, 28.72) * mm, "end": v(-7, 28.72) * mm});
            skLineSegment(sketch, "E418", {"start": v(-7, 28.72) * mm, "end": v(-7, 29.72) * mm});
            skLineSegment(sketch, "E419", {"start": v(-7, 29.72) * mm, "end": v(-7.8, 29.72) * mm});
            skLineSegment(sketch, "E420", {"start": v(-7.8, 29.72) * mm, "end": v(-7.8, 32.82) * mm});
            skLineSegment(sketch, "E421", {"start": v(-7.8, 32.82) * mm, "end": v(-7, 32.82) * mm});
            skLineSegment(sketch, "E422", {"start": v(-7, 32.82) * mm, "end": v(-7, 38.62) * mm});
            skLineSegment(sketch, "E423", {"start": v(-7, 38.62) * mm, "end": v(-7.8, 38.62) * mm});
            skLineSegment(sketch, "E424", {"start": v(-7.8, 38.62) * mm, "end": v(-7.8, 41.72) * mm});
            skLineSegment(sketch, "E425", {"start": v(-7.8, 41.72) * mm, "end": v(-7, 41.72) * mm});
            skLineSegment(sketch, "E426", {"start": v(-7, 41.72) * mm, "end": v(-7, 42.72) * mm});
            skLineSegment(sketch, "E427", {"start": v(-7, 42.72) * mm, "end": v(7, 42.72) * mm});
            skLineSegment(sketch, "E428", {"start": v(7, 42.72) * mm, "end": v(7, 41.72) * mm});
            skLineSegment(sketch, "E429", {"start": v(7, 41.72) * mm, "end": v(7.8, 41.72) * mm});
            skLineSegment(sketch, "E430", {"start": v(7.8, 41.72) * mm, "end": v(7.8, 38.62) * mm});
            skLineSegment(sketch, "E431", {"start": v(7.8, 38.62) * mm, "end": v(7, 38.62) * mm});
            skLineSegment(sketch, "E432", {"start": v(7, 38.62) * mm, "end": v(7, 32.82) * mm});
            skLineSegment(sketch, "E433", {"start": v(7, 32.82) * mm, "end": v(7.8, 32.82) * mm});
            skLineSegment(sketch, "E434", {"start": v(7.8, 32.82) * mm, "end": v(7.8, 29.72) * mm});
            skLineSegment(sketch, "E435", {"start": v(7.8, 29.72) * mm, "end": v(7, 29.72) * mm});
            skLineSegment(sketch, "E436", {"start": v(7, 10.67) * mm, "end": v(7, 9.67) * mm});
            skLineSegment(sketch, "E437", {"start": v(7, 9.67) * mm, "end": v(-7, 9.67) * mm});
            skLineSegment(sketch, "E438", {"start": v(-7, 9.67) * mm, "end": v(-7, 10.67) * mm});
            skLineSegment(sketch, "E439", {"start": v(-7, 10.67) * mm, "end": v(-7.8, 10.67) * mm});
            skLineSegment(sketch, "E440", {"start": v(-7.8, 10.67) * mm, "end": v(-7.8, 13.77) * mm});
            skLineSegment(sketch, "E441", {"start": v(-7.8, 13.77) * mm, "end": v(-7, 13.77) * mm});
            skLineSegment(sketch, "E442", {"start": v(-7, 13.77) * mm, "end": v(-7, 19.57) * mm});
            skLineSegment(sketch, "E443", {"start": v(-7, 19.57) * mm, "end": v(-7.8, 19.57) * mm});
            skLineSegment(sketch, "E444", {"start": v(-7.8, 19.57) * mm, "end": v(-7.8, 22.67) * mm});
            skLineSegment(sketch, "E445", {"start": v(-7.8, 22.67) * mm, "end": v(-7, 22.67) * mm});
            skLineSegment(sketch, "E446", {"start": v(-7, 22.67) * mm, "end": v(-7, 23.67) * mm});
            skLineSegment(sketch, "E447", {"start": v(-7, 23.67) * mm, "end": v(7, 23.67) * mm});
            skLineSegment(sketch, "E448", {"start": v(7, 23.67) * mm, "end": v(7, 22.67) * mm});
            skLineSegment(sketch, "E449", {"start": v(7, 22.67) * mm, "end": v(7.8, 22.67) * mm});
            skLineSegment(sketch, "E450", {"start": v(7.8, 22.67) * mm, "end": v(7.8, 19.57) * mm});
            skLineSegment(sketch, "E451", {"start": v(7.8, 19.57) * mm, "end": v(7, 19.57) * mm});
            skLineSegment(sketch, "E452", {"start": v(7, 19.57) * mm, "end": v(7, 13.77) * mm});
            skLineSegment(sketch, "E453", {"start": v(7, 13.77) * mm, "end": v(7.8, 13.77) * mm});
            skLineSegment(sketch, "E454", {"start": v(7.8, 13.77) * mm, "end": v(7.8, 10.67) * mm});
            skLineSegment(sketch, "E455", {"start": v(7.8, 10.67) * mm, "end": v(7, 10.67) * mm});
            skLineSegment(sketch, "E456", {"start": v(7, -8.38) * mm, "end": v(7, -9.38) * mm});
            skLineSegment(sketch, "E457", {"start": v(7, -9.38) * mm, "end": v(-7, -9.38) * mm});
            skLineSegment(sketch, "E458", {"start": v(-7, -9.38) * mm, "end": v(-7, -8.38) * mm});
            skLineSegment(sketch, "E459", {"start": v(-7, -8.38) * mm, "end": v(-7.8, -8.38) * mm});
            skLineSegment(sketch, "E460", {"start": v(-7.8, -8.38) * mm, "end": v(-7.8, -5.28) * mm});
            skLineSegment(sketch, "E461", {"start": v(-7.8, -5.28) * mm, "end": v(-7, -5.28) * mm});
            skLineSegment(sketch, "E462", {"start": v(-7, -5.28) * mm, "end": v(-7, 0.52) * mm});
            skLineSegment(sketch, "E463", {"start": v(-7, 0.52) * mm, "end": v(-7.8, 0.52) * mm});
            skLineSegment(sketch, "E464", {"start": v(-7.8, 0.52) * mm, "end": v(-7.8, 3.62) * mm});
            skLineSegment(sketch, "E465", {"start": v(-7.8, 3.62) * mm, "end": v(-7, 3.62) * mm});
            skLineSegment(sketch, "E466", {"start": v(-7, 3.62) * mm, "end": v(-7, 4.62) * mm});
            skLineSegment(sketch, "E467", {"start": v(-7, 4.62) * mm, "end": v(7, 4.62) * mm});
            skLineSegment(sketch, "E468", {"start": v(7, 4.62) * mm, "end": v(7, 3.62) * mm});
            skLineSegment(sketch, "E469", {"start": v(7, 3.62) * mm, "end": v(7.8, 3.62) * mm});
            skLineSegment(sketch, "E470", {"start": v(7.8, 3.62) * mm, "end": v(7.8, 0.52) * mm});
            skLineSegment(sketch, "E471", {"start": v(7.8, 0.52) * mm, "end": v(7, 0.52) * mm});
            skLineSegment(sketch, "E472", {"start": v(7, 0.52) * mm, "end": v(7, -5.28) * mm});
            skLineSegment(sketch, "E473", {"start": v(7, -5.28) * mm, "end": v(7.8, -5.28) * mm});
            skLineSegment(sketch, "E474", {"start": v(7.8, -5.28) * mm, "end": v(7.8, -8.38) * mm});
            skLineSegment(sketch, "E475", {"start": v(7.8, -8.38) * mm, "end": v(7, -8.38) * mm});
            skLineSegment(sketch, "E476", {"start": v(7, -27.43) * mm, "end": v(7, -28.43) * mm});
            skLineSegment(sketch, "E477", {"start": v(7, -28.43) * mm, "end": v(-7, -28.43) * mm});
            skLineSegment(sketch, "E478", {"start": v(-7, -28.43) * mm, "end": v(-7, -27.43) * mm});
            skLineSegment(sketch, "E479", {"start": v(-7, -27.43) * mm, "end": v(-7.8, -27.43) * mm});
            skLineSegment(sketch, "E480", {"start": v(-7.8, -27.43) * mm, "end": v(-7.8, -24.33) * mm});
            skLineSegment(sketch, "E481", {"start": v(-7.8, -24.33) * mm, "end": v(-7, -24.33) * mm});
            skLineSegment(sketch, "E482", {"start": v(-7, -24.33) * mm, "end": v(-7, -18.53) * mm});
            skLineSegment(sketch, "E483", {"start": v(-7, -18.53) * mm, "end": v(-7.8, -18.53) * mm});
            skLineSegment(sketch, "E484", {"start": v(-7.8, -18.53) * mm, "end": v(-7.8, -15.43) * mm});
            skLineSegment(sketch, "E485", {"start": v(-7.8, -15.43) * mm, "end": v(-7, -15.43) * mm});
            skLineSegment(sketch, "E486", {"start": v(-7, -15.43) * mm, "end": v(-7, -14.43) * mm});
            skLineSegment(sketch, "E487", {"start": v(-7, -14.43) * mm, "end": v(7, -14.43) * mm});
            skLineSegment(sketch, "E488", {"start": v(7, -14.43) * mm, "end": v(7, -15.43) * mm});
            skLineSegment(sketch, "E489", {"start": v(7, -15.43) * mm, "end": v(7.8, -15.43) * mm});
            skLineSegment(sketch, "E490", {"start": v(7.8, -15.43) * mm, "end": v(7.8, -18.53) * mm});
            skLineSegment(sketch, "E491", {"start": v(7.8, -18.53) * mm, "end": v(7, -18.53) * mm});
            skLineSegment(sketch, "E492", {"start": v(7, -18.53) * mm, "end": v(7, -24.33) * mm});
            skLineSegment(sketch, "E493", {"start": v(7, -24.33) * mm, "end": v(7.8, -24.33) * mm});
            skLineSegment(sketch, "E494", {"start": v(7.8, -24.33) * mm, "end": v(7.8, -27.43) * mm});
            skLineSegment(sketch, "E495", {"start": v(7.8, -27.43) * mm, "end": v(7, -27.43) * mm});
            skLineSegment(sketch, "E496", {"start": v(7, -46.48) * mm, "end": v(7, -47.48) * mm});
            skLineSegment(sketch, "E497", {"start": v(7, -47.48) * mm, "end": v(-7, -47.48) * mm});
            skLineSegment(sketch, "E498", {"start": v(-7, -47.48) * mm, "end": v(-7, -46.48) * mm});
            skLineSegment(sketch, "E499", {"start": v(-7, -46.48) * mm, "end": v(-7.8, -46.48) * mm});
            skLineSegment(sketch, "E500", {"start": v(-7.8, -46.48) * mm, "end": v(-7.8, -43.38) * mm});
            skLineSegment(sketch, "E501", {"start": v(-7.8, -43.38) * mm, "end": v(-7, -43.38) * mm});
            skLineSegment(sketch, "E502", {"start": v(-7, -43.38) * mm, "end": v(-7, -37.58) * mm});
            skLineSegment(sketch, "E503", {"start": v(-7, -37.58) * mm, "end": v(-7.8, -37.58) * mm});
            skLineSegment(sketch, "E504", {"start": v(-7.8, -37.58) * mm, "end": v(-7.8, -34.48) * mm});
            skLineSegment(sketch, "E505", {"start": v(-7.8, -34.48) * mm, "end": v(-7, -34.48) * mm});
            skLineSegment(sketch, "E506", {"start": v(-7, -34.48) * mm, "end": v(-7, -33.48) * mm});
            skLineSegment(sketch, "E507", {"start": v(-7, -33.48) * mm, "end": v(7, -33.48) * mm});
            skLineSegment(sketch, "E508", {"start": v(7, -33.48) * mm, "end": v(7, -34.48) * mm});
            skLineSegment(sketch, "E509", {"start": v(7, -34.48) * mm, "end": v(7.8, -34.48) * mm});
            skLineSegment(sketch, "E510", {"start": v(7.8, -34.48) * mm, "end": v(7.8, -37.58) * mm});
            skLineSegment(sketch, "E511", {"start": v(7.8, -37.58) * mm, "end": v(7, -37.58) * mm});
            skLineSegment(sketch, "E512", {"start": v(7, -37.58) * mm, "end": v(7, -43.38) * mm});
            skLineSegment(sketch, "E513", {"start": v(7, -43.38) * mm, "end": v(7.8, -43.38) * mm});
            skLineSegment(sketch, "E514", {"start": v(7.8, -43.38) * mm, "end": v(7.8, -46.48) * mm});
            skLineSegment(sketch, "E515", {"start": v(7.8, -46.48) * mm, "end": v(7, -46.48) * mm});
            skLineSegment(sketch, "E516", {"start": v(26.05, 24.96) * mm, "end": v(26.05, 23.96) * mm});
            skLineSegment(sketch, "E517", {"start": v(26.05, 23.96) * mm, "end": v(12.05, 23.96) * mm});
            skLineSegment(sketch, "E518", {"start": v(12.05, 23.96) * mm, "end": v(12.05, 24.96) * mm});
            skLineSegment(sketch, "E519", {"start": v(12.05, 24.96) * mm, "end": v(11.25, 24.96) * mm});
            skLineSegment(sketch, "E520", {"start": v(11.25, 24.96) * mm, "end": v(11.25, 28.06) * mm});
            skLineSegment(sketch, "E521", {"start": v(11.25, 28.06) * mm, "end": v(12.05, 28.06) * mm});
            skLineSegment(sketch, "E522", {"start": v(12.05, 28.06) * mm, "end": v(12.05, 33.86) * mm});
            skLineSegment(sketch, "E523", {"start": v(12.05, 33.86) * mm, "end": v(11.25, 33.86) * mm});
            skLineSegment(sketch, "E524", {"start": v(11.25, 33.86) * mm, "end": v(11.25, 36.96) * mm});
            skLineSegment(sketch, "E525", {"start": v(11.25, 36.96) * mm, "end": v(12.05, 36.96) * mm});
            skLineSegment(sketch, "E526", {"start": v(12.05, 36.96) * mm, "end": v(12.05, 37.96) * mm});
            skLineSegment(sketch, "E527", {"start": v(12.05, 37.96) * mm, "end": v(26.05, 37.96) * mm});
            skLineSegment(sketch, "E528", {"start": v(26.05, 37.96) * mm, "end": v(26.05, 36.96) * mm});
            skLineSegment(sketch, "E529", {"start": v(26.05, 36.96) * mm, "end": v(26.85, 36.96) * mm});
            skLineSegment(sketch, "E530", {"start": v(26.85, 36.96) * mm, "end": v(26.85, 33.86) * mm});
            skLineSegment(sketch, "E531", {"start": v(26.85, 33.86) * mm, "end": v(26.05, 33.86) * mm});
            skLineSegment(sketch, "E532", {"start": v(26.05, 33.86) * mm, "end": v(26.05, 28.06) * mm});
            skLineSegment(sketch, "E533", {"start": v(26.05, 28.06) * mm, "end": v(26.85, 28.06) * mm});
            skLineSegment(sketch, "E534", {"start": v(26.85, 28.06) * mm, "end": v(26.85, 24.96) * mm});
            skLineSegment(sketch, "E535", {"start": v(26.85, 24.96) * mm, "end": v(26.05, 24.96) * mm});
            skLineSegment(sketch, "E536", {"start": v(26.05, 5.9) * mm, "end": v(26.05, 4.9) * mm});
            skLineSegment(sketch, "E537", {"start": v(26.05, 4.9) * mm, "end": v(12.05, 4.9) * mm});
            skLineSegment(sketch, "E538", {"start": v(12.05, 4.9) * mm, "end": v(12.05, 5.9) * mm});
            skLineSegment(sketch, "E539", {"start": v(12.05, 5.9) * mm, "end": v(11.25, 5.9) * mm});
            skLineSegment(sketch, "E540", {"start": v(11.25, 5.9) * mm, "end": v(11.25, 9) * mm});
            skLineSegment(sketch, "E541", {"start": v(11.25, 9) * mm, "end": v(12.05, 9) * mm});
            skLineSegment(sketch, "E542", {"start": v(12.05, 9) * mm, "end": v(12.05, 14.8) * mm});
            skLineSegment(sketch, "E543", {"start": v(12.05, 14.8) * mm, "end": v(11.25, 14.8) * mm});
            skLineSegment(sketch, "E544", {"start": v(11.25, 14.8) * mm, "end": v(11.25, 17.9) * mm});
            skLineSegment(sketch, "E545", {"start": v(11.25, 17.9) * mm, "end": v(12.05, 17.9) * mm});
            skLineSegment(sketch, "E546", {"start": v(12.05, 17.9) * mm, "end": v(12.05, 18.9) * mm});
            skLineSegment(sketch, "E547", {"start": v(12.05, 18.9) * mm, "end": v(26.05, 18.9) * mm});
            skLineSegment(sketch, "E548", {"start": v(26.05, 18.9) * mm, "end": v(26.05, 17.9) * mm});
            skLineSegment(sketch, "E549", {"start": v(26.05, 17.9) * mm, "end": v(26.85, 17.9) * mm});
            skLineSegment(sketch, "E550", {"start": v(26.85, 17.9) * mm, "end": v(26.85, 14.8) * mm});
            skLineSegment(sketch, "E551", {"start": v(26.85, 14.8) * mm, "end": v(26.05, 14.8) * mm});
            skLineSegment(sketch, "E552", {"start": v(26.05, 14.8) * mm, "end": v(26.05, 9) * mm});
            skLineSegment(sketch, "E553", {"start": v(26.05, 9) * mm, "end": v(26.85, 9) * mm});
            skLineSegment(sketch, "E554", {"start": v(26.85, 9) * mm, "end": v(26.85, 5.9) * mm});
            skLineSegment(sketch, "E555", {"start": v(26.85, 5.9) * mm, "end": v(26.05, 5.9) * mm});
            skLineSegment(sketch, "E556", {"start": v(26.05, -13.14) * mm, "end": v(26.05, -14.14) * mm});
            skLineSegment(sketch, "E557", {"start": v(26.05, -14.14) * mm, "end": v(12.05, -14.14) * mm});
            skLineSegment(sketch, "E558", {"start": v(12.05, -14.14) * mm, "end": v(12.05, -13.14) * mm});
            skLineSegment(sketch, "E559", {"start": v(12.05, -13.14) * mm, "end": v(11.25, -13.14) * mm});
            skLineSegment(sketch, "E560", {"start": v(11.25, -13.14) * mm, "end": v(11.25, -10.04) * mm});
            skLineSegment(sketch, "E561", {"start": v(11.25, -10.04) * mm, "end": v(12.05, -10.04) * mm});
            skLineSegment(sketch, "E562", {"start": v(12.05, -10.04) * mm, "end": v(12.05, -4.24) * mm});
            skLineSegment(sketch, "E563", {"start": v(12.05, -4.24) * mm, "end": v(11.25, -4.24) * mm});
            skLineSegment(sketch, "E564", {"start": v(11.25, -4.24) * mm, "end": v(11.25, -1.14) * mm});
            skLineSegment(sketch, "E565", {"start": v(11.25, -1.14) * mm, "end": v(12.05, -1.14) * mm});
            skLineSegment(sketch, "E566", {"start": v(12.05, -1.14) * mm, "end": v(12.05, -0.14) * mm});
            skLineSegment(sketch, "E567", {"start": v(12.05, -0.14) * mm, "end": v(26.05, -0.14) * mm});
            skLineSegment(sketch, "E568", {"start": v(26.05, -0.14) * mm, "end": v(26.05, -1.14) * mm});
            skLineSegment(sketch, "E569", {"start": v(26.05, -1.14) * mm, "end": v(26.85, -1.14) * mm});
            skLineSegment(sketch, "E570", {"start": v(26.85, -1.14) * mm, "end": v(26.85, -4.24) * mm});
            skLineSegment(sketch, "E571", {"start": v(26.85, -4.24) * mm, "end": v(26.05, -4.24) * mm});
            skLineSegment(sketch, "E572", {"start": v(26.05, -4.24) * mm, "end": v(26.05, -10.04) * mm});
            skLineSegment(sketch, "E573", {"start": v(26.05, -10.04) * mm, "end": v(26.85, -10.04) * mm});
            skLineSegment(sketch, "E574", {"start": v(26.85, -10.04) * mm, "end": v(26.85, -13.14) * mm});
            skLineSegment(sketch, "E575", {"start": v(26.85, -13.14) * mm, "end": v(26.05, -13.14) * mm});
            skLineSegment(sketch, "E576", {"start": v(26.05, -32.2) * mm, "end": v(26.05, -33.2) * mm});
            skLineSegment(sketch, "E577", {"start": v(26.05, -33.2) * mm, "end": v(12.05, -33.2) * mm});
            skLineSegment(sketch, "E578", {"start": v(12.05, -33.2) * mm, "end": v(12.05, -32.2) * mm});
            skLineSegment(sketch, "E579", {"start": v(12.05, -32.2) * mm, "end": v(11.25, -32.2) * mm});
            skLineSegment(sketch, "E580", {"start": v(11.25, -32.2) * mm, "end": v(11.25, -29.1) * mm});
            skLineSegment(sketch, "E581", {"start": v(11.25, -29.1) * mm, "end": v(12.05, -29.1) * mm});
            skLineSegment(sketch, "E582", {"start": v(12.05, -29.1) * mm, "end": v(12.05, -23.3) * mm});
            skLineSegment(sketch, "E583", {"start": v(12.05, -23.3) * mm, "end": v(11.25, -23.3) * mm});
            skLineSegment(sketch, "E584", {"start": v(11.25, -23.3) * mm, "end": v(11.25, -20.2) * mm});
            skLineSegment(sketch, "E585", {"start": v(11.25, -20.2) * mm, "end": v(12.05, -20.2) * mm});
            skLineSegment(sketch, "E586", {"start": v(12.05, -20.2) * mm, "end": v(12.05, -19.2) * mm});
            skLineSegment(sketch, "E587", {"start": v(12.05, -19.2) * mm, "end": v(26.05, -19.2) * mm});
            skLineSegment(sketch, "E588", {"start": v(26.05, -19.2) * mm, "end": v(26.05, -20.2) * mm});
            skLineSegment(sketch, "E589", {"start": v(26.05, -20.2) * mm, "end": v(26.85, -20.2) * mm});
            skLineSegment(sketch, "E590", {"start": v(26.85, -20.2) * mm, "end": v(26.85, -23.3) * mm});
            skLineSegment(sketch, "E591", {"start": v(26.85, -23.3) * mm, "end": v(26.05, -23.3) * mm});
            skLineSegment(sketch, "E592", {"start": v(26.05, -23.3) * mm, "end": v(26.05, -29.1) * mm});
            skLineSegment(sketch, "E593", {"start": v(26.05, -29.1) * mm, "end": v(26.85, -29.1) * mm});
            skLineSegment(sketch, "E594", {"start": v(26.85, -29.1) * mm, "end": v(26.85, -32.2) * mm});
            skLineSegment(sketch, "E595", {"start": v(26.85, -32.2) * mm, "end": v(26.05, -32.2) * mm});
            skLineSegment(sketch, "E596", {"start": v(26.05, -51.24) * mm, "end": v(26.05, -52.24) * mm});
            skLineSegment(sketch, "E597", {"start": v(26.05, -52.24) * mm, "end": v(12.05, -52.24) * mm});
            skLineSegment(sketch, "E598", {"start": v(12.05, -52.24) * mm, "end": v(12.05, -51.24) * mm});
            skLineSegment(sketch, "E599", {"start": v(12.05, -51.24) * mm, "end": v(11.25, -51.24) * mm});
            skLineSegment(sketch, "E600", {"start": v(11.25, -51.24) * mm, "end": v(11.25, -48.14) * mm});
            skLineSegment(sketch, "E601", {"start": v(11.25, -48.14) * mm, "end": v(12.05, -48.14) * mm});
            skLineSegment(sketch, "E602", {"start": v(12.05, -48.14) * mm, "end": v(12.05, -42.34) * mm});
            skLineSegment(sketch, "E603", {"start": v(12.05, -42.34) * mm, "end": v(11.25, -42.34) * mm});
            skLineSegment(sketch, "E604", {"start": v(11.25, -42.34) * mm, "end": v(11.25, -39.24) * mm});
            skLineSegment(sketch, "E605", {"start": v(11.25, -39.24) * mm, "end": v(12.05, -39.24) * mm});
            skLineSegment(sketch, "E606", {"start": v(12.05, -39.24) * mm, "end": v(12.05, -38.24) * mm});
            skLineSegment(sketch, "E607", {"start": v(12.05, -38.24) * mm, "end": v(26.05, -38.24) * mm});
            skLineSegment(sketch, "E608", {"start": v(26.05, -38.24) * mm, "end": v(26.05, -39.24) * mm});
            skLineSegment(sketch, "E609", {"start": v(26.05, -39.24) * mm, "end": v(26.85, -39.24) * mm});
            skLineSegment(sketch, "E610", {"start": v(26.85, -39.24) * mm, "end": v(26.85, -42.34) * mm});
            skLineSegment(sketch, "E611", {"start": v(26.85, -42.34) * mm, "end": v(26.05, -42.34) * mm});
            skLineSegment(sketch, "E612", {"start": v(26.05, -42.34) * mm, "end": v(26.05, -48.14) * mm});
            skLineSegment(sketch, "E613", {"start": v(26.05, -48.14) * mm, "end": v(26.85, -48.14) * mm});
            skLineSegment(sketch, "E614", {"start": v(26.85, -48.14) * mm, "end": v(26.85, -51.24) * mm});
            skLineSegment(sketch, "E615", {"start": v(26.85, -51.24) * mm, "end": v(26.05, -51.24) * mm});
            skLineSegment(sketch, "E616", {"start": v(45.1, 24.96) * mm, "end": v(45.1, 23.96) * mm});
            skLineSegment(sketch, "E617", {"start": v(45.1, 23.96) * mm, "end": v(31.1, 23.96) * mm});
            skLineSegment(sketch, "E618", {"start": v(31.1, 23.96) * mm, "end": v(31.1, 24.96) * mm});
            skLineSegment(sketch, "E619", {"start": v(31.1, 24.96) * mm, "end": v(30.3, 24.96) * mm});
            skLineSegment(sketch, "E620", {"start": v(30.3, 24.96) * mm, "end": v(30.3, 28.06) * mm});
            skLineSegment(sketch, "E621", {"start": v(30.3, 28.06) * mm, "end": v(31.1, 28.06) * mm});
            skLineSegment(sketch, "E622", {"start": v(31.1, 28.06) * mm, "end": v(31.1, 33.86) * mm});
            skLineSegment(sketch, "E623", {"start": v(31.1, 33.86) * mm, "end": v(30.3, 33.86) * mm});
            skLineSegment(sketch, "E624", {"start": v(30.3, 33.86) * mm, "end": v(30.3, 36.96) * mm});
            skLineSegment(sketch, "E625", {"start": v(30.3, 36.96) * mm, "end": v(31.1, 36.96) * mm});
            skLineSegment(sketch, "E626", {"start": v(31.1, 36.96) * mm, "end": v(31.1, 37.96) * mm});
            skLineSegment(sketch, "E627", {"start": v(31.1, 37.96) * mm, "end": v(45.1, 37.96) * mm});
            skLineSegment(sketch, "E628", {"start": v(45.1, 37.96) * mm, "end": v(45.1, 36.96) * mm});
            skLineSegment(sketch, "E629", {"start": v(45.1, 36.96) * mm, "end": v(45.9, 36.96) * mm});
            skLineSegment(sketch, "E630", {"start": v(45.9, 36.96) * mm, "end": v(45.9, 33.86) * mm});
            skLineSegment(sketch, "E631", {"start": v(45.9, 33.86) * mm, "end": v(45.1, 33.86) * mm});
            skLineSegment(sketch, "E632", {"start": v(45.1, 33.86) * mm, "end": v(45.1, 28.06) * mm});
            skLineSegment(sketch, "E633", {"start": v(45.1, 28.06) * mm, "end": v(45.9, 28.06) * mm});
            skLineSegment(sketch, "E634", {"start": v(45.9, 28.06) * mm, "end": v(45.9, 24.96) * mm});
            skLineSegment(sketch, "E635", {"start": v(45.9, 24.96) * mm, "end": v(45.1, 24.96) * mm});
            skLineSegment(sketch, "E636", {"start": v(45.1, 5.9) * mm, "end": v(45.1, 4.9) * mm});
            skLineSegment(sketch, "E637", {"start": v(45.1, 4.9) * mm, "end": v(31.1, 4.9) * mm});
            skLineSegment(sketch, "E638", {"start": v(31.1, 4.9) * mm, "end": v(31.1, 5.9) * mm});
            skLineSegment(sketch, "E639", {"start": v(31.1, 5.9) * mm, "end": v(30.3, 5.9) * mm});
            skLineSegment(sketch, "E640", {"start": v(30.3, 5.9) * mm, "end": v(30.3, 9) * mm});
            skLineSegment(sketch, "E641", {"start": v(30.3, 9) * mm, "end": v(31.1, 9) * mm});
            skLineSegment(sketch, "E642", {"start": v(31.1, 9) * mm, "end": v(31.1, 14.8) * mm});
            skLineSegment(sketch, "E643", {"start": v(31.1, 14.8) * mm, "end": v(30.3, 14.8) * mm});
            skLineSegment(sketch, "E644", {"start": v(30.3, 14.8) * mm, "end": v(30.3, 17.9) * mm});
            skLineSegment(sketch, "E645", {"start": v(30.3, 17.9) * mm, "end": v(31.1, 17.9) * mm});
            skLineSegment(sketch, "E646", {"start": v(31.1, 17.9) * mm, "end": v(31.1, 18.9) * mm});
            skLineSegment(sketch, "E647", {"start": v(31.1, 18.9) * mm, "end": v(45.1, 18.9) * mm});
            skLineSegment(sketch, "E648", {"start": v(45.1, 18.9) * mm, "end": v(45.1, 17.9) * mm});
            skLineSegment(sketch, "E649", {"start": v(45.1, 17.9) * mm, "end": v(45.9, 17.9) * mm});
            skLineSegment(sketch, "E650", {"start": v(45.9, 17.9) * mm, "end": v(45.9, 14.8) * mm});
            skLineSegment(sketch, "E651", {"start": v(45.9, 14.8) * mm, "end": v(45.1, 14.8) * mm});
            skLineSegment(sketch, "E652", {"start": v(45.1, 14.8) * mm, "end": v(45.1, 9) * mm});
            skLineSegment(sketch, "E653", {"start": v(45.1, 9) * mm, "end": v(45.9, 9) * mm});
            skLineSegment(sketch, "E654", {"start": v(45.9, 9) * mm, "end": v(45.9, 5.9) * mm});
            skLineSegment(sketch, "E655", {"start": v(45.9, 5.9) * mm, "end": v(45.1, 5.9) * mm});
            skLineSegment(sketch, "E656", {"start": v(45.1, -13.14) * mm, "end": v(45.1, -14.14) * mm});
            skLineSegment(sketch, "E657", {"start": v(45.1, -14.14) * mm, "end": v(31.1, -14.14) * mm});
            skLineSegment(sketch, "E658", {"start": v(31.1, -14.14) * mm, "end": v(31.1, -13.14) * mm});
            skLineSegment(sketch, "E659", {"start": v(31.1, -13.14) * mm, "end": v(30.3, -13.14) * mm});
            skLineSegment(sketch, "E660", {"start": v(30.3, -13.14) * mm, "end": v(30.3, -10.04) * mm});
            skLineSegment(sketch, "E661", {"start": v(30.3, -10.04) * mm, "end": v(31.1, -10.04) * mm});
            skLineSegment(sketch, "E662", {"start": v(31.1, -10.04) * mm, "end": v(31.1, -4.24) * mm});
            skLineSegment(sketch, "E663", {"start": v(31.1, -4.24) * mm, "end": v(30.3, -4.24) * mm});
            skLineSegment(sketch, "E664", {"start": v(30.3, -4.24) * mm, "end": v(30.3, -1.14) * mm});
            skLineSegment(sketch, "E665", {"start": v(30.3, -1.14) * mm, "end": v(31.1, -1.14) * mm});
            skLineSegment(sketch, "E666", {"start": v(31.1, -1.14) * mm, "end": v(31.1, -0.14) * mm});
            skLineSegment(sketch, "E667", {"start": v(31.1, -0.14) * mm, "end": v(45.1, -0.14) * mm});
            skLineSegment(sketch, "E668", {"start": v(45.1, -0.14) * mm, "end": v(45.1, -1.14) * mm});
            skLineSegment(sketch, "E669", {"start": v(45.1, -1.14) * mm, "end": v(45.9, -1.14) * mm});
            skLineSegment(sketch, "E670", {"start": v(45.9, -1.14) * mm, "end": v(45.9, -4.24) * mm});
            skLineSegment(sketch, "E671", {"start": v(45.9, -4.24) * mm, "end": v(45.1, -4.24) * mm});
            skLineSegment(sketch, "E672", {"start": v(45.1, -4.24) * mm, "end": v(45.1, -10.04) * mm});
            skLineSegment(sketch, "E673", {"start": v(45.1, -10.04) * mm, "end": v(45.9, -10.04) * mm});
            skLineSegment(sketch, "E674", {"start": v(45.9, -10.04) * mm, "end": v(45.9, -13.14) * mm});
            skLineSegment(sketch, "E675", {"start": v(45.9, -13.14) * mm, "end": v(45.1, -13.14) * mm});
            skLineSegment(sketch, "E676", {"start": v(45.1, -32.2) * mm, "end": v(45.1, -33.2) * mm});
            skLineSegment(sketch, "E677", {"start": v(45.1, -33.2) * mm, "end": v(31.1, -33.2) * mm});
            skLineSegment(sketch, "E678", {"start": v(31.1, -33.2) * mm, "end": v(31.1, -32.2) * mm});
            skLineSegment(sketch, "E679", {"start": v(31.1, -32.2) * mm, "end": v(30.3, -32.2) * mm});
            skLineSegment(sketch, "E680", {"start": v(30.3, -32.2) * mm, "end": v(30.3, -29.1) * mm});
            skLineSegment(sketch, "E681", {"start": v(30.3, -29.1) * mm, "end": v(31.1, -29.1) * mm});
            skLineSegment(sketch, "E682", {"start": v(31.1, -29.1) * mm, "end": v(31.1, -23.3) * mm});
            skLineSegment(sketch, "E683", {"start": v(31.1, -23.3) * mm, "end": v(30.3, -23.3) * mm});
            skLineSegment(sketch, "E684", {"start": v(30.3, -23.3) * mm, "end": v(30.3, -20.2) * mm});
            skLineSegment(sketch, "E685", {"start": v(30.3, -20.2) * mm, "end": v(31.1, -20.2) * mm});
            skLineSegment(sketch, "E686", {"start": v(31.1, -20.2) * mm, "end": v(31.1, -19.2) * mm});
            skLineSegment(sketch, "E687", {"start": v(31.1, -19.2) * mm, "end": v(45.1, -19.2) * mm});
            skLineSegment(sketch, "E688", {"start": v(45.1, -19.2) * mm, "end": v(45.1, -20.2) * mm});
            skLineSegment(sketch, "E689", {"start": v(45.1, -20.2) * mm, "end": v(45.9, -20.2) * mm});
            skLineSegment(sketch, "E690", {"start": v(45.9, -20.2) * mm, "end": v(45.9, -23.3) * mm});
            skLineSegment(sketch, "E691", {"start": v(45.9, -23.3) * mm, "end": v(45.1, -23.3) * mm});
            skLineSegment(sketch, "E692", {"start": v(45.1, -23.3) * mm, "end": v(45.1, -29.1) * mm});
            skLineSegment(sketch, "E693", {"start": v(45.1, -29.1) * mm, "end": v(45.9, -29.1) * mm});
            skLineSegment(sketch, "E694", {"start": v(45.9, -29.1) * mm, "end": v(45.9, -32.2) * mm});
            skLineSegment(sketch, "E695", {"start": v(45.9, -32.2) * mm, "end": v(45.1, -32.2) * mm});
            skLineSegment(sketch, "E696", {"start": v(45.1, -51.24) * mm, "end": v(45.1, -52.24) * mm});
            skLineSegment(sketch, "E697", {"start": v(45.1, -52.24) * mm, "end": v(31.1, -52.24) * mm});
            skLineSegment(sketch, "E698", {"start": v(31.1, -52.24) * mm, "end": v(31.1, -51.24) * mm});
            skLineSegment(sketch, "E699", {"start": v(31.1, -51.24) * mm, "end": v(30.3, -51.24) * mm});
            skLineSegment(sketch, "E700", {"start": v(30.3, -51.24) * mm, "end": v(30.3, -48.14) * mm});
            skLineSegment(sketch, "E701", {"start": v(30.3, -48.14) * mm, "end": v(31.1, -48.14) * mm});
            skLineSegment(sketch, "E702", {"start": v(31.1, -48.14) * mm, "end": v(31.1, -42.34) * mm});
            skLineSegment(sketch, "E703", {"start": v(31.1, -42.34) * mm, "end": v(30.3, -42.34) * mm});
            skLineSegment(sketch, "E704", {"start": v(30.3, -42.34) * mm, "end": v(30.3, -39.24) * mm});
            skLineSegment(sketch, "E705", {"start": v(30.3, -39.24) * mm, "end": v(31.1, -39.24) * mm});
            skLineSegment(sketch, "E706", {"start": v(31.1, -39.24) * mm, "end": v(31.1, -38.24) * mm});
            skLineSegment(sketch, "E707", {"start": v(31.1, -38.24) * mm, "end": v(45.1, -38.24) * mm});
            skLineSegment(sketch, "E708", {"start": v(45.1, -38.24) * mm, "end": v(45.1, -39.24) * mm});
            skLineSegment(sketch, "E709", {"start": v(45.1, -39.24) * mm, "end": v(45.9, -39.24) * mm});
            skLineSegment(sketch, "E710", {"start": v(45.9, -39.24) * mm, "end": v(45.9, -42.34) * mm});
            skLineSegment(sketch, "E711", {"start": v(45.9, -42.34) * mm, "end": v(45.1, -42.34) * mm});
            skLineSegment(sketch, "E712", {"start": v(45.1, -42.34) * mm, "end": v(45.1, -48.14) * mm});
            skLineSegment(sketch, "E713", {"start": v(45.1, -48.14) * mm, "end": v(45.9, -48.14) * mm});
            skLineSegment(sketch, "E714", {"start": v(45.9, -48.14) * mm, "end": v(45.9, -51.24) * mm});
            skLineSegment(sketch, "E715", {"start": v(45.9, -51.24) * mm, "end": v(45.1, -51.24) * mm});
            skLineSegment(sketch, "E716", {"start": v(64.15, 24.96) * mm, "end": v(64.15, 23.96) * mm});
            skLineSegment(sketch, "E717", {"start": v(64.15, 23.96) * mm, "end": v(50.15, 23.96) * mm});
            skLineSegment(sketch, "E718", {"start": v(50.15, 23.96) * mm, "end": v(50.15, 24.96) * mm});
            skLineSegment(sketch, "E719", {"start": v(50.15, 24.96) * mm, "end": v(49.35, 24.96) * mm});
            skLineSegment(sketch, "E720", {"start": v(49.35, 24.96) * mm, "end": v(49.35, 28.06) * mm});
            skLineSegment(sketch, "E721", {"start": v(49.35, 28.06) * mm, "end": v(50.15, 28.06) * mm});
            skLineSegment(sketch, "E722", {"start": v(50.15, 28.06) * mm, "end": v(50.15, 33.86) * mm});
            skLineSegment(sketch, "E723", {"start": v(50.15, 33.86) * mm, "end": v(49.35, 33.86) * mm});
            skLineSegment(sketch, "E724", {"start": v(49.35, 33.86) * mm, "end": v(49.35, 36.96) * mm});
            skLineSegment(sketch, "E725", {"start": v(49.35, 36.96) * mm, "end": v(50.15, 36.96) * mm});
            skLineSegment(sketch, "E726", {"start": v(50.15, 36.96) * mm, "end": v(50.15, 37.96) * mm});
            skLineSegment(sketch, "E727", {"start": v(50.15, 37.96) * mm, "end": v(64.15, 37.96) * mm});
            skLineSegment(sketch, "E728", {"start": v(64.15, 37.96) * mm, "end": v(64.15, 36.96) * mm});
            skLineSegment(sketch, "E729", {"start": v(64.15, 36.96) * mm, "end": v(64.95, 36.96) * mm});
            skLineSegment(sketch, "E730", {"start": v(64.95, 36.96) * mm, "end": v(64.95, 33.86) * mm});
            skLineSegment(sketch, "E731", {"start": v(64.95, 33.86) * mm, "end": v(64.15, 33.86) * mm});
            skLineSegment(sketch, "E732", {"start": v(64.15, 33.86) * mm, "end": v(64.15, 28.06) * mm});
            skLineSegment(sketch, "E733", {"start": v(64.15, 28.06) * mm, "end": v(64.95, 28.06) * mm});
            skLineSegment(sketch, "E734", {"start": v(64.95, 28.06) * mm, "end": v(64.95, 24.96) * mm});
            skLineSegment(sketch, "E735", {"start": v(64.95, 24.96) * mm, "end": v(64.15, 24.96) * mm});
            skLineSegment(sketch, "E736", {"start": v(64.15, 5.9) * mm, "end": v(64.15, 4.9) * mm});
            skLineSegment(sketch, "E737", {"start": v(64.15, 4.9) * mm, "end": v(50.15, 4.9) * mm});
            skLineSegment(sketch, "E738", {"start": v(50.15, 4.9) * mm, "end": v(50.15, 5.9) * mm});
            skLineSegment(sketch, "E739", {"start": v(50.15, 5.9) * mm, "end": v(49.35, 5.9) * mm});
            skLineSegment(sketch, "E740", {"start": v(49.35, 5.9) * mm, "end": v(49.35, 9) * mm});
            skLineSegment(sketch, "E741", {"start": v(49.35, 9) * mm, "end": v(50.15, 9) * mm});
            skLineSegment(sketch, "E742", {"start": v(50.15, 9) * mm, "end": v(50.15, 14.8) * mm});
            skLineSegment(sketch, "E743", {"start": v(50.15, 14.8) * mm, "end": v(49.35, 14.8) * mm});
            skLineSegment(sketch, "E744", {"start": v(49.35, 14.8) * mm, "end": v(49.35, 17.9) * mm});
            skLineSegment(sketch, "E745", {"start": v(49.35, 17.9) * mm, "end": v(50.15, 17.9) * mm});
            skLineSegment(sketch, "E746", {"start": v(50.15, 17.9) * mm, "end": v(50.15, 18.9) * mm});
            skLineSegment(sketch, "E747", {"start": v(50.15, 18.9) * mm, "end": v(64.15, 18.9) * mm});
            skLineSegment(sketch, "E748", {"start": v(64.15, 18.9) * mm, "end": v(64.15, 17.9) * mm});
            skLineSegment(sketch, "E749", {"start": v(64.15, 17.9) * mm, "end": v(64.95, 17.9) * mm});
            skLineSegment(sketch, "E750", {"start": v(64.95, 17.9) * mm, "end": v(64.95, 14.8) * mm});
            skLineSegment(sketch, "E751", {"start": v(64.95, 14.8) * mm, "end": v(64.15, 14.8) * mm});
            skLineSegment(sketch, "E752", {"start": v(64.15, 14.8) * mm, "end": v(64.15, 9) * mm});
            skLineSegment(sketch, "E753", {"start": v(64.15, 9) * mm, "end": v(64.95, 9) * mm});
            skLineSegment(sketch, "E754", {"start": v(64.95, 9) * mm, "end": v(64.95, 5.9) * mm});
            skLineSegment(sketch, "E755", {"start": v(64.95, 5.9) * mm, "end": v(64.15, 5.9) * mm});
            skLineSegment(sketch, "E756", {"start": v(64.15, -13.14) * mm, "end": v(64.15, -14.14) * mm});
            skLineSegment(sketch, "E757", {"start": v(64.15, -14.14) * mm, "end": v(50.15, -14.14) * mm});
            skLineSegment(sketch, "E758", {"start": v(50.15, -14.14) * mm, "end": v(50.15, -13.14) * mm});
            skLineSegment(sketch, "E759", {"start": v(50.15, -13.14) * mm, "end": v(49.35, -13.14) * mm});
            skLineSegment(sketch, "E760", {"start": v(49.35, -13.14) * mm, "end": v(49.35, -10.04) * mm});
            skLineSegment(sketch, "E761", {"start": v(49.35, -10.04) * mm, "end": v(50.15, -10.04) * mm});
            skLineSegment(sketch, "E762", {"start": v(50.15, -10.04) * mm, "end": v(50.15, -4.24) * mm});
            skLineSegment(sketch, "E763", {"start": v(50.15, -4.24) * mm, "end": v(49.35, -4.24) * mm});
            skLineSegment(sketch, "E764", {"start": v(49.35, -4.24) * mm, "end": v(49.35, -1.14) * mm});
            skLineSegment(sketch, "E765", {"start": v(49.35, -1.14) * mm, "end": v(50.15, -1.14) * mm});
            skLineSegment(sketch, "E766", {"start": v(50.15, -1.14) * mm, "end": v(50.15, -0.14) * mm});
            skLineSegment(sketch, "E767", {"start": v(50.15, -0.14) * mm, "end": v(64.15, -0.14) * mm});
            skLineSegment(sketch, "E768", {"start": v(64.15, -0.14) * mm, "end": v(64.15, -1.14) * mm});
            skLineSegment(sketch, "E769", {"start": v(64.15, -1.14) * mm, "end": v(64.95, -1.14) * mm});
            skLineSegment(sketch, "E770", {"start": v(64.95, -1.14) * mm, "end": v(64.95, -4.24) * mm});
            skLineSegment(sketch, "E771", {"start": v(64.95, -4.24) * mm, "end": v(64.15, -4.24) * mm});
            skLineSegment(sketch, "E772", {"start": v(64.15, -4.24) * mm, "end": v(64.15, -10.04) * mm});
            skLineSegment(sketch, "E773", {"start": v(64.15, -10.04) * mm, "end": v(64.95, -10.04) * mm});
            skLineSegment(sketch, "E774", {"start": v(64.95, -10.04) * mm, "end": v(64.95, -13.14) * mm});
            skLineSegment(sketch, "E775", {"start": v(64.95, -13.14) * mm, "end": v(64.15, -13.14) * mm});
            skLineSegment(sketch, "E776", {"start": v(64.15, -32.2) * mm, "end": v(64.15, -33.2) * mm});
            skLineSegment(sketch, "E777", {"start": v(64.15, -33.2) * mm, "end": v(50.15, -33.2) * mm});
            skLineSegment(sketch, "E778", {"start": v(50.15, -33.2) * mm, "end": v(50.15, -32.2) * mm});
            skLineSegment(sketch, "E779", {"start": v(50.15, -32.2) * mm, "end": v(49.35, -32.2) * mm});
            skLineSegment(sketch, "E780", {"start": v(49.35, -32.2) * mm, "end": v(49.35, -29.1) * mm});
            skLineSegment(sketch, "E781", {"start": v(49.35, -29.1) * mm, "end": v(50.15, -29.1) * mm});
            skLineSegment(sketch, "E782", {"start": v(50.15, -29.1) * mm, "end": v(50.15, -23.3) * mm});
            skLineSegment(sketch, "E783", {"start": v(50.15, -23.3) * mm, "end": v(49.35, -23.3) * mm});
            skLineSegment(sketch, "E784", {"start": v(49.35, -23.3) * mm, "end": v(49.35, -20.2) * mm});
            skLineSegment(sketch, "E785", {"start": v(49.35, -20.2) * mm, "end": v(50.15, -20.2) * mm});
            skLineSegment(sketch, "E786", {"start": v(50.15, -20.2) * mm, "end": v(50.15, -19.2) * mm});
            skLineSegment(sketch, "E787", {"start": v(50.15, -19.2) * mm, "end": v(64.15, -19.2) * mm});
            skLineSegment(sketch, "E788", {"start": v(64.15, -19.2) * mm, "end": v(64.15, -20.2) * mm});
            skLineSegment(sketch, "E789", {"start": v(64.15, -20.2) * mm, "end": v(64.95, -20.2) * mm});
            skLineSegment(sketch, "E790", {"start": v(64.95, -20.2) * mm, "end": v(64.95, -23.3) * mm});
            skLineSegment(sketch, "E791", {"start": v(64.95, -23.3) * mm, "end": v(64.15, -23.3) * mm});
            skLineSegment(sketch, "E792", {"start": v(64.15, -23.3) * mm, "end": v(64.15, -29.1) * mm});
            skLineSegment(sketch, "E793", {"start": v(64.15, -29.1) * mm, "end": v(64.95, -29.1) * mm});
            skLineSegment(sketch, "E794", {"start": v(64.95, -29.1) * mm, "end": v(64.95, -32.2) * mm});
            skLineSegment(sketch, "E795", {"start": v(64.95, -32.2) * mm, "end": v(64.15, -32.2) * mm});
            skLineSegment(sketch, "E796", {"start": v(81.9, -45.74) * mm, "end": v(81.9, -52.01) * mm});
            skLineSegment(sketch, "E797", {"start": v(81.9, -52.01) * mm, "end": v(80.27, -52.01) * mm});
            skLineSegment(sketch, "E798", {"start": v(80.27, -52.01) * mm, "end": v(80.27, -53) * mm});
            skLineSegment(sketch, "E799", {"start": v(80.27, -53) * mm, "end": v(76.98, -53) * mm});
            skLineSegment(sketch, "E800", {"start": v(76.98, -53) * mm, "end": v(76.98, -52.01) * mm});
            skLineSegment(sketch, "E801", {"start": v(76.98, -52.01) * mm, "end": v(75.25, -52.01) * mm});
            skLineSegment(sketch, "E802", {"start": v(75.25, -52.01) * mm, "end": v(75.25, -51.21) * mm});
            skLineSegment(sketch, "E803", {"start": v(75.25, -51.21) * mm, "end": v(74.48, -51.21) * mm});
            skLineSegment(sketch, "E804", {"start": v(74.48, -51.21) * mm, "end": v(74.48, -51.24) * mm});
            skLineSegment(sketch, "E805", {"start": v(74.48, -51.24) * mm, "end": v(73.68, -51.24) * mm});
            skLineSegment(sketch, "E806", {"start": v(73.68, -51.24) * mm, "end": v(73.68, -52.24) * mm});
            skLineSegment(sketch, "E807", {"start": v(73.68, -52.24) * mm, "end": v(59.68, -52.24) * mm});
            skLineSegment(sketch, "E808", {"start": v(59.68, -52.24) * mm, "end": v(59.68, -51.24) * mm});
            skLineSegment(sketch, "E809", {"start": v(59.68, -51.24) * mm, "end": v(58.87, -51.24) * mm});
            skLineSegment(sketch, "E810", {"start": v(58.87, -51.24) * mm, "end": v(58.87, -51.21) * mm});
            skLineSegment(sketch, "E811", {"start": v(58.87, -51.21) * mm, "end": v(58.1, -51.21) * mm});
            skLineSegment(sketch, "E812", {"start": v(58.1, -51.21) * mm, "end": v(58.1, -52.01) * mm});
            skLineSegment(sketch, "E813", {"start": v(58.1, -52.01) * mm, "end": v(56.38, -52.01) * mm});
            skLineSegment(sketch, "E814", {"start": v(56.38, -52.01) * mm, "end": v(56.38, -53) * mm});
            skLineSegment(sketch, "E815", {"start": v(56.38, -53) * mm, "end": v(53.07, -53) * mm});
            skLineSegment(sketch, "E816", {"start": v(53.07, -53) * mm, "end": v(53.07, -52.01) * mm});
            skLineSegment(sketch, "E817", {"start": v(53.07, -52.01) * mm, "end": v(51.45, -52.01) * mm});
            skLineSegment(sketch, "E818", {"start": v(51.45, -52.01) * mm, "end": v(51.45, -45.74) * mm});
            skLineSegment(sketch, "E819", {"start": v(51.45, -45.74) * mm, "end": v(50.58, -45.74) * mm});
            skLineSegment(sketch, "E820", {"start": v(50.58, -45.74) * mm, "end": v(50.58, -42.94) * mm});
            skLineSegment(sketch, "E821", {"start": v(50.58, -42.94) * mm, "end": v(51.45, -42.94) * mm});
            skLineSegment(sketch, "E822", {"start": v(51.45, -42.94) * mm, "end": v(51.45, -39.71) * mm});
            skLineSegment(sketch, "E823", {"start": v(51.45, -39.71) * mm, "end": v(53.07, -39.71) * mm});
            skLineSegment(sketch, "E824", {"start": v(53.07, -39.71) * mm, "end": v(53.07, -38.8) * mm});
            skLineSegment(sketch, "E825", {"start": v(53.07, -38.8) * mm, "end": v(56.38, -38.8) * mm});
            skLineSegment(sketch, "E826", {"start": v(56.38, -38.8) * mm, "end": v(56.38, -39.71) * mm});
            skLineSegment(sketch, "E827", {"start": v(56.38, -39.71) * mm, "end": v(58.1, -39.71) * mm});
            skLineSegment(sketch, "E828", {"start": v(58.1, -39.71) * mm, "end": v(58.1, -40.51) * mm});
            skLineSegment(sketch, "E829", {"start": v(58.1, -40.51) * mm, "end": v(58.87, -40.51) * mm});
            skLineSegment(sketch, "E830", {"start": v(58.87, -40.51) * mm, "end": v(58.87, -39.24) * mm});
            skLineSegment(sketch, "E831", {"start": v(58.87, -39.24) * mm, "end": v(59.68, -39.24) * mm});
            skLineSegment(sketch, "E832", {"start": v(59.68, -39.24) * mm, "end": v(59.68, -38.24) * mm});
            skLineSegment(sketch, "E833", {"start": v(59.68, -38.24) * mm, "end": v(73.68, -38.24) * mm});
            skLineSegment(sketch, "E834", {"start": v(73.68, -38.24) * mm, "end": v(73.68, -39.24) * mm});
            skLineSegment(sketch, "E835", {"start": v(73.68, -39.24) * mm, "end": v(74.48, -39.24) * mm});
            skLineSegment(sketch, "E836", {"start": v(74.48, -39.24) * mm, "end": v(74.48, -40.51) * mm});
            skLineSegment(sketch, "E837", {"start": v(74.48, -40.51) * mm, "end": v(75.25, -40.51) * mm});
            skLineSegment(sketch, "E838", {"start": v(75.25, -40.51) * mm, "end": v(75.25, -39.71) * mm});
            skLineSegment(sketch, "E839", {"start": v(75.25, -39.71) * mm, "end": v(76.98, -39.71) * mm});
            skLineSegment(sketch, "E840", {"start": v(76.98, -39.71) * mm, "end": v(76.98, -38.8) * mm});
            skLineSegment(sketch, "E841", {"start": v(76.98, -38.8) * mm, "end": v(80.27, -38.8) * mm});
            skLineSegment(sketch, "E842", {"start": v(80.27, -38.8) * mm, "end": v(80.27, -39.71) * mm});
            skLineSegment(sketch, "E843", {"start": v(80.27, -39.71) * mm, "end": v(81.9, -39.71) * mm});
            skLineSegment(sketch, "E844", {"start": v(81.9, -39.71) * mm, "end": v(81.9, -42.94) * mm});
            skLineSegment(sketch, "E845", {"start": v(81.9, -42.94) * mm, "end": v(82.78, -42.94) * mm});
            skLineSegment(sketch, "E846", {"start": v(82.78, -42.94) * mm, "end": v(82.78, -45.74) * mm});
            skLineSegment(sketch, "E847", {"start": v(82.78, -45.74) * mm, "end": v(81.9, -45.74) * mm});
            skLineSegment(sketch, "E848", {"start": v(83.2, 24.96) * mm, "end": v(83.2, 23.96) * mm});
            skLineSegment(sketch, "E849", {"start": v(83.2, 23.96) * mm, "end": v(69.2, 23.96) * mm});
            skLineSegment(sketch, "E850", {"start": v(69.2, 23.96) * mm, "end": v(69.2, 24.96) * mm});
            skLineSegment(sketch, "E851", {"start": v(69.2, 24.96) * mm, "end": v(68.4, 24.96) * mm});
            skLineSegment(sketch, "E852", {"start": v(68.4, 24.96) * mm, "end": v(68.4, 28.06) * mm});
            skLineSegment(sketch, "E853", {"start": v(68.4, 28.06) * mm, "end": v(69.2, 28.06) * mm});
            skLineSegment(sketch, "E854", {"start": v(69.2, 28.06) * mm, "end": v(69.2, 33.86) * mm});
            skLineSegment(sketch, "E855", {"start": v(69.2, 33.86) * mm, "end": v(68.4, 33.86) * mm});
            skLineSegment(sketch, "E856", {"start": v(68.4, 33.86) * mm, "end": v(68.4, 36.96) * mm});
            skLineSegment(sketch, "E857", {"start": v(68.4, 36.96) * mm, "end": v(69.2, 36.96) * mm});
            skLineSegment(sketch, "E858", {"start": v(69.2, 36.96) * mm, "end": v(69.2, 37.96) * mm});
            skLineSegment(sketch, "E859", {"start": v(69.2, 37.96) * mm, "end": v(83.2, 37.96) * mm});
            skLineSegment(sketch, "E860", {"start": v(83.2, 37.96) * mm, "end": v(83.2, 36.96) * mm});
            skLineSegment(sketch, "E861", {"start": v(83.2, 36.96) * mm, "end": v(84, 36.96) * mm});
            skLineSegment(sketch, "E862", {"start": v(84, 36.96) * mm, "end": v(84, 33.86) * mm});
            skLineSegment(sketch, "E863", {"start": v(84, 33.86) * mm, "end": v(83.2, 33.86) * mm});
            skLineSegment(sketch, "E864", {"start": v(83.2, 33.86) * mm, "end": v(83.2, 28.06) * mm});
            skLineSegment(sketch, "E865", {"start": v(83.2, 28.06) * mm, "end": v(84, 28.06) * mm});
            skLineSegment(sketch, "E866", {"start": v(84, 28.06) * mm, "end": v(84, 24.96) * mm});
            skLineSegment(sketch, "E867", {"start": v(84, 24.96) * mm, "end": v(83.2, 24.96) * mm});
            skLineSegment(sketch, "E868", {"start": v(83.2, 5.9) * mm, "end": v(83.2, 4.9) * mm});
            skLineSegment(sketch, "E869", {"start": v(83.2, 4.9) * mm, "end": v(69.2, 4.9) * mm});
            skLineSegment(sketch, "E870", {"start": v(69.2, 4.9) * mm, "end": v(69.2, 5.9) * mm});
            skLineSegment(sketch, "E871", {"start": v(69.2, 5.9) * mm, "end": v(68.4, 5.9) * mm});
            skLineSegment(sketch, "E872", {"start": v(68.4, 5.9) * mm, "end": v(68.4, 9) * mm});
            skLineSegment(sketch, "E873", {"start": v(68.4, 9) * mm, "end": v(69.2, 9) * mm});
            skLineSegment(sketch, "E874", {"start": v(69.2, 9) * mm, "end": v(69.2, 14.8) * mm});
            skLineSegment(sketch, "E875", {"start": v(69.2, 14.8) * mm, "end": v(68.4, 14.8) * mm});
            skLineSegment(sketch, "E876", {"start": v(68.4, 14.8) * mm, "end": v(68.4, 17.9) * mm});
            skLineSegment(sketch, "E877", {"start": v(68.4, 17.9) * mm, "end": v(69.2, 17.9) * mm});
            skLineSegment(sketch, "E878", {"start": v(69.2, 17.9) * mm, "end": v(69.2, 18.9) * mm});
            skLineSegment(sketch, "E879", {"start": v(69.2, 18.9) * mm, "end": v(83.2, 18.9) * mm});
            skLineSegment(sketch, "E880", {"start": v(83.2, 18.9) * mm, "end": v(83.2, 17.9) * mm});
            skLineSegment(sketch, "E881", {"start": v(83.2, 17.9) * mm, "end": v(84, 17.9) * mm});
            skLineSegment(sketch, "E882", {"start": v(84, 17.9) * mm, "end": v(84, 14.8) * mm});
            skLineSegment(sketch, "E883", {"start": v(84, 14.8) * mm, "end": v(83.2, 14.8) * mm});
            skLineSegment(sketch, "E884", {"start": v(83.2, 14.8) * mm, "end": v(83.2, 9) * mm});
            skLineSegment(sketch, "E885", {"start": v(83.2, 9) * mm, "end": v(84, 9) * mm});
            skLineSegment(sketch, "E886", {"start": v(84, 9) * mm, "end": v(84, 5.9) * mm});
            skLineSegment(sketch, "E887", {"start": v(84, 5.9) * mm, "end": v(83.2, 5.9) * mm});
            skLineSegment(sketch, "E888", {"start": v(83.2, -13.14) * mm, "end": v(83.2, -14.14) * mm});
            skLineSegment(sketch, "E889", {"start": v(83.2, -14.14) * mm, "end": v(69.2, -14.14) * mm});
            skLineSegment(sketch, "E890", {"start": v(69.2, -14.14) * mm, "end": v(69.2, -13.14) * mm});
            skLineSegment(sketch, "E891", {"start": v(69.2, -13.14) * mm, "end": v(68.4, -13.14) * mm});
            skLineSegment(sketch, "E892", {"start": v(68.4, -13.14) * mm, "end": v(68.4, -10.04) * mm});
            skLineSegment(sketch, "E893", {"start": v(68.4, -10.04) * mm, "end": v(69.2, -10.04) * mm});
            skLineSegment(sketch, "E894", {"start": v(69.2, -10.04) * mm, "end": v(69.2, -4.24) * mm});
            skLineSegment(sketch, "E895", {"start": v(69.2, -4.24) * mm, "end": v(68.4, -4.24) * mm});
            skLineSegment(sketch, "E896", {"start": v(68.4, -4.24) * mm, "end": v(68.4, -1.14) * mm});
            skLineSegment(sketch, "E897", {"start": v(68.4, -1.14) * mm, "end": v(69.2, -1.14) * mm});
            skLineSegment(sketch, "E898", {"start": v(69.2, -1.14) * mm, "end": v(69.2, -0.14) * mm});
            skLineSegment(sketch, "E899", {"start": v(69.2, -0.14) * mm, "end": v(83.2, -0.14) * mm});
            skLineSegment(sketch, "E900", {"start": v(83.2, -0.14) * mm, "end": v(83.2, -1.14) * mm});
            skLineSegment(sketch, "E901", {"start": v(83.2, -1.14) * mm, "end": v(84, -1.14) * mm});
            skLineSegment(sketch, "E902", {"start": v(84, -1.14) * mm, "end": v(84, -4.24) * mm});
            skLineSegment(sketch, "E903", {"start": v(84, -4.24) * mm, "end": v(83.2, -4.24) * mm});
            skLineSegment(sketch, "E904", {"start": v(83.2, -4.24) * mm, "end": v(83.2, -10.04) * mm});
            skLineSegment(sketch, "E905", {"start": v(83.2, -10.04) * mm, "end": v(84, -10.04) * mm});
            skLineSegment(sketch, "E906", {"start": v(84, -10.04) * mm, "end": v(84, -13.14) * mm});
            skLineSegment(sketch, "E907", {"start": v(84, -13.14) * mm, "end": v(83.2, -13.14) * mm});
            skLineSegment(sketch, "E908", {"start": v(83.2, -32.2) * mm, "end": v(83.2, -33.2) * mm});
            skLineSegment(sketch, "E909", {"start": v(83.2, -33.2) * mm, "end": v(69.2, -33.2) * mm});
            skLineSegment(sketch, "E910", {"start": v(69.2, -33.2) * mm, "end": v(69.2, -32.2) * mm});
            skLineSegment(sketch, "E911", {"start": v(69.2, -32.2) * mm, "end": v(68.4, -32.2) * mm});
            skLineSegment(sketch, "E912", {"start": v(68.4, -32.2) * mm, "end": v(68.4, -29.1) * mm});
            skLineSegment(sketch, "E913", {"start": v(68.4, -29.1) * mm, "end": v(69.2, -29.1) * mm});
            skLineSegment(sketch, "E914", {"start": v(69.2, -29.1) * mm, "end": v(69.2, -23.3) * mm});
            skLineSegment(sketch, "E915", {"start": v(69.2, -23.3) * mm, "end": v(68.4, -23.3) * mm});
            skLineSegment(sketch, "E916", {"start": v(68.4, -23.3) * mm, "end": v(68.4, -20.2) * mm});
            skLineSegment(sketch, "E917", {"start": v(68.4, -20.2) * mm, "end": v(69.2, -20.2) * mm});
            skLineSegment(sketch, "E918", {"start": v(69.2, -20.2) * mm, "end": v(69.2, -19.2) * mm});
            skLineSegment(sketch, "E919", {"start": v(69.2, -19.2) * mm, "end": v(83.2, -19.2) * mm});
            skLineSegment(sketch, "E920", {"start": v(83.2, -19.2) * mm, "end": v(83.2, -20.2) * mm});
            skLineSegment(sketch, "E921", {"start": v(83.2, -20.2) * mm, "end": v(84, -20.2) * mm});
            skLineSegment(sketch, "E922", {"start": v(84, -20.2) * mm, "end": v(84, -23.3) * mm});
            skLineSegment(sketch, "E923", {"start": v(84, -23.3) * mm, "end": v(83.2, -23.3) * mm});
            skLineSegment(sketch, "E924", {"start": v(83.2, -23.3) * mm, "end": v(83.2, -29.1) * mm});
            skLineSegment(sketch, "E925", {"start": v(83.2, -29.1) * mm, "end": v(84, -29.1) * mm});
            skLineSegment(sketch, "E926", {"start": v(84, -29.1) * mm, "end": v(84, -32.2) * mm});
            skLineSegment(sketch, "E927", {"start": v(84, -32.2) * mm, "end": v(83.2, -32.2) * mm});
            skLineSegment(sketch, "E928.bottom", {"start": v(-84, 38.76) * mm, "end": v(-68.4, 38.76) * mm});
            skLineSegment(sketch, "E928.top", {"start": v(-84, 23.16) * mm, "end": v(-68.4, 23.16) * mm});
            skLineSegment(sketch, "E928.left", {"start": v(-84, 38.76) * mm, "end": v(-84, 23.16) * mm});
            skLineSegment(sketch, "E928.right", {"start": v(-68.4, 38.76) * mm, "end": v(-68.4, 23.16) * mm});
            skLineSegment(sketch, "E929.bottom", {"start": v(-84, 19.7) * mm, "end": v(-68.4, 19.7) * mm});
            skLineSegment(sketch, "E929.top", {"start": v(-84, 4.1) * mm, "end": v(-68.4, 4.1) * mm});
            skLineSegment(sketch, "E929.left", {"start": v(-84, 19.7) * mm, "end": v(-84, 4.1) * mm});
            skLineSegment(sketch, "E929.right", {"start": v(-68.4, 19.7) * mm, "end": v(-68.4, 4.1) * mm});
            skLineSegment(sketch, "E930.bottom", {"start": v(-84, 0.66) * mm, "end": v(-68.4, 0.66) * mm});
            skLineSegment(sketch, "E930.top", {"start": v(-84, -14.94) * mm, "end": v(-68.4, -14.94) * mm});
            skLineSegment(sketch, "E930.left", {"start": v(-84, 0.66) * mm, "end": v(-84, -14.94) * mm});
            skLineSegment(sketch, "E930.right", {"start": v(-68.4, 0.66) * mm, "end": v(-68.4, -14.94) * mm});
            skLineSegment(sketch, "E931.bottom", {"start": v(-64.95, 43.52) * mm, "end": v(-49.35, 43.52) * mm});
            skLineSegment(sketch, "E931.top", {"start": v(-64.95, 27.92) * mm, "end": v(-49.35, 27.92) * mm});
            skLineSegment(sketch, "E931.left", {"start": v(-64.95, 43.52) * mm, "end": v(-64.95, 27.92) * mm});
            skLineSegment(sketch, "E931.right", {"start": v(-49.35, 43.52) * mm, "end": v(-49.35, 27.92) * mm});
            skLineSegment(sketch, "E932.bottom", {"start": v(-64.95, 24.47) * mm, "end": v(-49.35, 24.47) * mm});
            skLineSegment(sketch, "E932.top", {"start": v(-64.95, 8.87) * mm, "end": v(-49.35, 8.87) * mm});
            skLineSegment(sketch, "E932.left", {"start": v(-64.95, 24.47) * mm, "end": v(-64.95, 8.87) * mm});
            skLineSegment(sketch, "E932.right", {"start": v(-49.35, 24.47) * mm, "end": v(-49.35, 8.87) * mm});
            skLineSegment(sketch, "E933.bottom", {"start": v(-64.95, 5.42) * mm, "end": v(-49.35, 5.42) * mm});
            skLineSegment(sketch, "E933.top", {"start": v(-64.95, -10.18) * mm, "end": v(-49.35, -10.18) * mm});
            skLineSegment(sketch, "E933.left", {"start": v(-64.95, 5.42) * mm, "end": v(-64.95, -10.18) * mm});
            skLineSegment(sketch, "E933.right", {"start": v(-49.35, 5.42) * mm, "end": v(-49.35, -10.18) * mm});
            skLineSegment(sketch, "E934.bottom", {"start": v(-64.95, -13.63) * mm, "end": v(-49.35, -13.63) * mm});
            skLineSegment(sketch, "E934.top", {"start": v(-64.95, -29.23) * mm, "end": v(-49.35, -29.23) * mm});
            skLineSegment(sketch, "E934.left", {"start": v(-64.95, -13.63) * mm, "end": v(-64.95, -29.23) * mm});
            skLineSegment(sketch, "E934.right", {"start": v(-49.35, -13.63) * mm, "end": v(-49.35, -29.23) * mm});
            skLineSegment(sketch, "E935.bottom", {"start": v(-64.95, -32.68) * mm, "end": v(-49.35, -32.68) * mm});
            skLineSegment(sketch, "E935.top", {"start": v(-64.95, -48.28) * mm, "end": v(-49.35, -48.28) * mm});
            skLineSegment(sketch, "E935.left", {"start": v(-64.95, -32.68) * mm, "end": v(-64.95, -48.28) * mm});
            skLineSegment(sketch, "E935.right", {"start": v(-49.35, -32.68) * mm, "end": v(-49.35, -48.28) * mm});
            skLineSegment(sketch, "E936.bottom", {"start": v(-45.9, 53.04) * mm, "end": v(-30.3, 53.04) * mm});
            skLineSegment(sketch, "E936.top", {"start": v(-45.9, 37.44) * mm, "end": v(-30.3, 37.44) * mm});
            skLineSegment(sketch, "E936.left", {"start": v(-45.9, 53.04) * mm, "end": v(-45.9, 37.44) * mm});
            skLineSegment(sketch, "E936.right", {"start": v(-30.3, 53.04) * mm, "end": v(-30.3, 37.44) * mm});
            skLineSegment(sketch, "E937.bottom", {"start": v(-45.9, 34) * mm, "end": v(-30.3, 34) * mm});
            skLineSegment(sketch, "E937.top", {"start": v(-45.9, 17.93) * mm, "end": v(-30.3, 17.93) * mm});
            skLineSegment(sketch, "E937.left", {"start": v(-45.9, 34) * mm, "end": v(-45.9, 17.93) * mm});
            skLineSegment(sketch, "E937.right", {"start": v(-30.3, 34) * mm, "end": v(-30.3, 17.93) * mm});
            skLineSegment(sketch, "E938.bottom", {"start": v(-45.9, 14.94) * mm, "end": v(-30.3, 14.94) * mm});
            skLineSegment(sketch, "E938.top", {"start": v(-45.9, -0.66) * mm, "end": v(-30.3, -0.66) * mm});
            skLineSegment(sketch, "E938.left", {"start": v(-45.9, 14.94) * mm, "end": v(-45.9, -0.66) * mm});
            skLineSegment(sketch, "E938.right", {"start": v(-30.3, 14.94) * mm, "end": v(-30.3, -0.66) * mm});
            skLineSegment(sketch, "E939.bottom", {"start": v(-45.9, -4.1) * mm, "end": v(-30.3, -4.1) * mm});
            skLineSegment(sketch, "E939.top", {"start": v(-45.9, -19.7) * mm, "end": v(-30.3, -19.7) * mm});
            skLineSegment(sketch, "E939.left", {"start": v(-45.9, -4.1) * mm, "end": v(-45.9, -19.7) * mm});
            skLineSegment(sketch, "E939.right", {"start": v(-30.3, -4.1) * mm, "end": v(-30.3, -19.7) * mm});
            skLineSegment(sketch, "E940.bottom", {"start": v(-45.9, -23.16) * mm, "end": v(-30.3, -23.16) * mm});
            skLineSegment(sketch, "E940.top", {"start": v(-45.9, -38.76) * mm, "end": v(-30.3, -38.76) * mm});
            skLineSegment(sketch, "E940.left", {"start": v(-45.9, -23.16) * mm, "end": v(-45.9, -38.76) * mm});
            skLineSegment(sketch, "E940.right", {"start": v(-30.3, -23.16) * mm, "end": v(-30.3, -38.76) * mm});
            skLineSegment(sketch, "E941.bottom", {"start": v(-26.85, -27.92) * mm, "end": v(-11.25, -27.92) * mm});
            skLineSegment(sketch, "E941.top", {"start": v(-26.85, -43.52) * mm, "end": v(-11.25, -43.52) * mm});
            skLineSegment(sketch, "E941.left", {"start": v(-26.85, -27.92) * mm, "end": v(-26.85, -43.52) * mm});
            skLineSegment(sketch, "E941.right", {"start": v(-11.25, -27.92) * mm, "end": v(-11.25, -43.52) * mm});
            skLineSegment(sketch, "E942.bottom", {"start": v(-26.85, -8.87) * mm, "end": v(-11.25, -8.87) * mm});
            skLineSegment(sketch, "E942.top", {"start": v(-26.85, -24.47) * mm, "end": v(-11.25, -24.47) * mm});
            skLineSegment(sketch, "E942.left", {"start": v(-26.85, -8.87) * mm, "end": v(-26.85, -24.47) * mm});
            skLineSegment(sketch, "E942.right", {"start": v(-11.25, -8.87) * mm, "end": v(-11.25, -24.47) * mm});
            skPoint(sketch, "E943.oppositeSnap0", {"position": v(-11.25, -2.07) * mm});
            skLineSegment(sketch, "E943.bottom", {"start": v(-26.85, 10.18) * mm, "end": v(-11.25, 10.18) * mm});
            skLineSegment(sketch, "E943.top", {"start": v(-26.85, -5.42) * mm, "end": v(-11.25, -5.42) * mm});
            skLineSegment(sketch, "E943.left", {"start": v(-26.85, 10.18) * mm, "end": v(-26.85, -5.42) * mm});
            skLineSegment(sketch, "E943.right", {"start": v(-11.25, 10.18) * mm, "end": v(-11.25, -5.42) * mm});
            skLineSegment(sketch, "E944.bottom", {"start": v(-26.85, 29.23) * mm, "end": v(-11.25, 29.23) * mm});
            skLineSegment(sketch, "E944.top", {"start": v(-26.85, 13.63) * mm, "end": v(-11.25, 13.63) * mm});
            skLineSegment(sketch, "E944.left", {"start": v(-26.85, 29.23) * mm, "end": v(-26.85, 13.63) * mm});
            skLineSegment(sketch, "E944.right", {"start": v(-11.25, 29.23) * mm, "end": v(-11.25, 13.63) * mm});
            skLineSegment(sketch, "E945.bottom", {"start": v(-26.85, 48.28) * mm, "end": v(-11.25, 48.28) * mm});
            skLineSegment(sketch, "E945.top", {"start": v(-26.85, 32.68) * mm, "end": v(-11.25, 32.68) * mm});
            skLineSegment(sketch, "E945.left", {"start": v(-26.85, 48.28) * mm, "end": v(-26.85, 32.68) * mm});
            skLineSegment(sketch, "E945.right", {"start": v(-11.25, 48.28) * mm, "end": v(-11.25, 32.68) * mm});
            skLineSegment(sketch, "E946.bottom", {"start": v(-7.8, 43.52) * mm, "end": v(7.8, 43.52) * mm});
            skLineSegment(sketch, "E946.top", {"start": v(-7.8, 27.92) * mm, "end": v(7.8, 27.92) * mm});
            skLineSegment(sketch, "E946.left", {"start": v(-7.8, 43.52) * mm, "end": v(-7.8, 27.92) * mm});
            skLineSegment(sketch, "E946.right", {"start": v(7.8, 43.52) * mm, "end": v(7.8, 27.92) * mm});
            skLineSegment(sketch, "E947.bottom", {"start": v(-7.8, 24.47) * mm, "end": v(7.8, 24.47) * mm});
            skLineSegment(sketch, "E947.top", {"start": v(-7.8, 8.87) * mm, "end": v(7.8, 8.87) * mm});
            skLineSegment(sketch, "E947.left", {"start": v(-7.8, 24.47) * mm, "end": v(-7.8, 8.87) * mm});
            skLineSegment(sketch, "E947.right", {"start": v(7.8, 24.47) * mm, "end": v(7.8, 8.87) * mm});
            skLineSegment(sketch, "E948.bottom", {"start": v(-7.8, 5.42) * mm, "end": v(7.8, 5.42) * mm});
            skLineSegment(sketch, "E948.top", {"start": v(-7.8, -10.18) * mm, "end": v(7.8, -10.18) * mm});
            skLineSegment(sketch, "E948.left", {"start": v(-7.8, 5.42) * mm, "end": v(-7.8, -10.18) * mm});
            skLineSegment(sketch, "E948.right", {"start": v(7.8, 5.42) * mm, "end": v(7.8, -10.18) * mm});
            skLineSegment(sketch, "E949.bottom", {"start": v(11.25, 38.76) * mm, "end": v(26.85, 38.76) * mm});
            skLineSegment(sketch, "E949.top", {"start": v(11.25, 23.16) * mm, "end": v(26.85, 23.16) * mm});
            skLineSegment(sketch, "E949.left", {"start": v(11.25, 38.76) * mm, "end": v(11.25, 23.16) * mm});
            skLineSegment(sketch, "E949.right", {"start": v(26.85, 38.76) * mm, "end": v(26.85, 23.16) * mm});
            skLineSegment(sketch, "E950.bottom", {"start": v(11.25, 19.7) * mm, "end": v(26.85, 19.7) * mm});
            skLineSegment(sketch, "E950.top", {"start": v(11.25, 4.1) * mm, "end": v(26.85, 4.1) * mm});
            skLineSegment(sketch, "E950.left", {"start": v(11.25, 19.7) * mm, "end": v(11.25, 4.1) * mm});
            skLineSegment(sketch, "E950.right", {"start": v(26.85, 19.7) * mm, "end": v(26.85, 4.1) * mm});
            skLineSegment(sketch, "E951.bottom", {"start": v(11.25, 0.66) * mm, "end": v(26.85, 0.66) * mm});
            skLineSegment(sketch, "E951.top", {"start": v(11.25, -14.94) * mm, "end": v(26.85, -14.94) * mm});
            skLineSegment(sketch, "E951.left", {"start": v(11.25, 0.66) * mm, "end": v(11.25, -14.94) * mm});
            skLineSegment(sketch, "E951.right", {"start": v(26.85, 0.66) * mm, "end": v(26.85, -14.94) * mm});
            skLineSegment(sketch, "E952.bottom", {"start": v(30.3, 38.76) * mm, "end": v(45.9, 38.76) * mm});
            skLineSegment(sketch, "E952.top", {"start": v(30.3, 23.16) * mm, "end": v(45.9, 23.16) * mm});
            skLineSegment(sketch, "E952.left", {"start": v(30.3, 38.76) * mm, "end": v(30.3, 23.16) * mm});
            skLineSegment(sketch, "E952.right", {"start": v(45.9, 38.76) * mm, "end": v(45.9, 23.16) * mm});
            skLineSegment(sketch, "E953.bottom", {"start": v(30.3, 19.7) * mm, "end": v(45.9, 19.7) * mm});
            skLineSegment(sketch, "E953.top", {"start": v(30.3, 4.1) * mm, "end": v(45.9, 4.1) * mm});
            skLineSegment(sketch, "E953.left", {"start": v(30.3, 19.7) * mm, "end": v(30.3, 4.1) * mm});
            skLineSegment(sketch, "E953.right", {"start": v(45.9, 19.7) * mm, "end": v(45.9, 4.1) * mm});
            skLineSegment(sketch, "E954.bottom", {"start": v(30.3, 0.66) * mm, "end": v(45.9, 0.66) * mm});
            skLineSegment(sketch, "E954.top", {"start": v(30.3, -14.94) * mm, "end": v(45.9, -14.94) * mm});
            skLineSegment(sketch, "E954.left", {"start": v(30.3, 0.66) * mm, "end": v(30.3, -14.94) * mm});
            skLineSegment(sketch, "E954.right", {"start": v(45.9, 0.66) * mm, "end": v(45.9, -14.94) * mm});
            skLineSegment(sketch, "E955.bottom", {"start": v(49.35, 38.76) * mm, "end": v(64.95, 38.76) * mm});
            skLineSegment(sketch, "E955.top", {"start": v(49.35, 23.16) * mm, "end": v(64.95, 23.16) * mm});
            skLineSegment(sketch, "E955.left", {"start": v(49.35, 38.76) * mm, "end": v(49.35, 23.16) * mm});
            skLineSegment(sketch, "E955.right", {"start": v(64.95, 38.76) * mm, "end": v(64.95, 23.16) * mm});
            skLineSegment(sketch, "E956.bottom", {"start": v(49.35, 19.7) * mm, "end": v(64.95, 19.7) * mm});
            skLineSegment(sketch, "E956.top", {"start": v(49.35, 4.1) * mm, "end": v(64.95, 4.1) * mm});
            skLineSegment(sketch, "E956.left", {"start": v(49.35, 19.7) * mm, "end": v(49.35, 4.1) * mm});
            skLineSegment(sketch, "E956.right", {"start": v(64.95, 19.7) * mm, "end": v(64.95, 4.1) * mm});
            skLineSegment(sketch, "E957.bottom", {"start": v(49.35, 0.66) * mm, "end": v(64.95, 0.66) * mm});
            skLineSegment(sketch, "E957.top", {"start": v(49.35, -14.94) * mm, "end": v(64.95, -14.94) * mm});
            skLineSegment(sketch, "E957.left", {"start": v(49.35, 0.66) * mm, "end": v(49.35, -14.94) * mm});
            skLineSegment(sketch, "E957.right", {"start": v(64.95, 0.66) * mm, "end": v(64.95, -14.94) * mm});
            skLineSegment(sketch, "E958.bottom", {"start": v(68.4, 38.76) * mm, "end": v(84, 38.76) * mm});
            skLineSegment(sketch, "E958.top", {"start": v(68.4, 23.16) * mm, "end": v(84, 23.16) * mm});
            skLineSegment(sketch, "E958.left", {"start": v(68.4, 38.76) * mm, "end": v(68.4, 23.16) * mm});
            skLineSegment(sketch, "E958.right", {"start": v(84, 38.76) * mm, "end": v(84, 23.16) * mm});
            skLineSegment(sketch, "E959.bottom", {"start": v(68.4, 19.7) * mm, "end": v(84, 19.7) * mm});
            skLineSegment(sketch, "E959.top", {"start": v(68.4, 4.1) * mm, "end": v(84, 4.1) * mm});
            skLineSegment(sketch, "E959.left", {"start": v(68.4, 19.7) * mm, "end": v(68.4, 4.1) * mm});
            skLineSegment(sketch, "E959.right", {"start": v(84, 19.7) * mm, "end": v(84, 4.1) * mm});
            skLineSegment(sketch, "E960.bottom", {"start": v(68.4, 0.66) * mm, "end": v(84, 0.66) * mm});
            skLineSegment(sketch, "E960.top", {"start": v(68.4, -14.94) * mm, "end": v(84, -14.94) * mm});
            skLineSegment(sketch, "E960.left", {"start": v(68.4, 0.66) * mm, "end": v(68.4, -14.94) * mm});
            skLineSegment(sketch, "E960.right", {"start": v(84, 0.66) * mm, "end": v(84, -14.94) * mm});
            skLineSegment(sketch, "E961.bottom", {"start": v(-7.8, -13.44) * mm, "end": v(7.8, -13.44) * mm});
            skLineSegment(sketch, "E961.top", {"start": v(-7.8, -29.57) * mm, "end": v(7.8, -29.57) * mm});
            skLineSegment(sketch, "E961.left", {"start": v(-7.8, -13.44) * mm, "end": v(-7.8, -29.57) * mm});
            skLineSegment(sketch, "E961.right", {"start": v(7.8, -13.44) * mm, "end": v(7.8, -29.57) * mm});
            skLineSegment(sketch, "E962.bottom", {"start": v(-7.8, -32.68) * mm, "end": v(7.8, -32.68) * mm});
            skLineSegment(sketch, "E962.top", {"start": v(-7.8, -48.28) * mm, "end": v(7.8, -48.28) * mm});
            skLineSegment(sketch, "E962.left", {"start": v(-7.8, -32.68) * mm, "end": v(-7.8, -48.28) * mm});
            skLineSegment(sketch, "E962.right", {"start": v(7.8, -32.68) * mm, "end": v(7.8, -48.28) * mm});
            skLineSegment(sketch, "E963.bottom", {"start": v(11.25, -18.4) * mm, "end": v(26.85, -18.4) * mm});
            skLineSegment(sketch, "E963.top", {"start": v(11.25, -34) * mm, "end": v(26.85, -34) * mm});
            skLineSegment(sketch, "E963.left", {"start": v(11.25, -18.4) * mm, "end": v(11.25, -34) * mm});
            skLineSegment(sketch, "E963.right", {"start": v(26.85, -18.4) * mm, "end": v(26.85, -34) * mm});
            skLineSegment(sketch, "E964.bottom", {"start": v(30.3, -18.4) * mm, "end": v(45.9, -18.4) * mm});
            skLineSegment(sketch, "E964.top", {"start": v(30.3, -34) * mm, "end": v(45.9, -34) * mm});
            skLineSegment(sketch, "E964.left", {"start": v(30.3, -18.4) * mm, "end": v(30.3, -34) * mm});
            skLineSegment(sketch, "E964.right", {"start": v(45.9, -18.4) * mm, "end": v(45.9, -34) * mm});
            skLineSegment(sketch, "E965.bottom", {"start": v(49.35, -18.4) * mm, "end": v(64.95, -18.4) * mm});
            skLineSegment(sketch, "E965.top", {"start": v(49.35, -34) * mm, "end": v(64.95, -34) * mm});
            skLineSegment(sketch, "E965.left", {"start": v(49.35, -18.4) * mm, "end": v(49.35, -34) * mm});
            skLineSegment(sketch, "E965.right", {"start": v(64.95, -18.4) * mm, "end": v(64.95, -34) * mm});
            skLineSegment(sketch, "E966.bottom", {"start": v(68.4, -18.4) * mm, "end": v(84, -18.4) * mm});
            skLineSegment(sketch, "E966.top", {"start": v(68.4, -34) * mm, "end": v(84, -34) * mm});
            skLineSegment(sketch, "E966.left", {"start": v(68.4, -18.4) * mm, "end": v(68.4, -34) * mm});
            skLineSegment(sketch, "E966.right", {"start": v(84, -18.4) * mm, "end": v(84, -34) * mm});
            skLineSegment(sketch, "E967.bottom", {"start": v(11.25, -37.44) * mm, "end": v(26.85, -37.44) * mm});
            skLineSegment(sketch, "E967.top", {"start": v(11.25, -53.04) * mm, "end": v(26.85, -53.04) * mm});
            skLineSegment(sketch, "E967.left", {"start": v(11.25, -37.44) * mm, "end": v(11.25, -53.04) * mm});
            skLineSegment(sketch, "E967.right", {"start": v(26.85, -37.44) * mm, "end": v(26.85, -53.04) * mm});
            skLineSegment(sketch, "E968.bottom", {"start": v(30.3, -37.44) * mm, "end": v(45.9, -37.44) * mm});
            skLineSegment(sketch, "E968.top", {"start": v(30.3, -53.04) * mm, "end": v(45.9, -53.04) * mm});
            skLineSegment(sketch, "E968.left", {"start": v(30.3, -37.44) * mm, "end": v(30.3, -53.04) * mm});
            skLineSegment(sketch, "E968.right", {"start": v(45.9, -37.44) * mm, "end": v(45.9, -53.04) * mm});
            skLineSegment(sketch, "E969.bottom", {"start": v(50.58, -37.44) * mm, "end": v(81.9, -37.44) * mm});
            skLineSegment(sketch, "E969.top", {"start": v(50.58, -54.35) * mm, "end": v(81.9, -54.35) * mm});
            skLineSegment(sketch, "E969.left", {"start": v(50.58, -37.44) * mm, "end": v(50.58, -54.35) * mm});
            skLineSegment(sketch, "E969.right", {"start": v(81.9, -37.44) * mm, "end": v(81.9, -54.35) * mm});
            skLineSegment(sketch, "E970.bottom", {"start": v(-67.56, -19.62) * mm, "end": v(-85.14, -19.62) * mm});
            skLineSegment(sketch, "E970.top", {"start": v(-67.56, -51.82) * mm, "end": v(-85.14, -51.82) * mm});
            skLineSegment(sketch, "E970.left", {"start": v(-67.56, -19.62) * mm, "end": v(-67.56, -51.82) * mm});
            skLineSegment(sketch, "E970.right", {"start": v(-85.14, -19.62) * mm, "end": v(-85.14, -51.82) * mm});
            skSolve(sketch);
        }
        {
            var Q0;
            Q0=makeQuery(id+"F0.imprint","IMPRINT",FACE,{"disambiguationData":[TD([[makeQuery(id+"F0.imprint","IMPRINT",EDGE,{"derivedFrom":sQuery(id+"F0.wireOp",EDGE,"E0")}),-1.0]])]});
            var Q1;
            {var subQ0=sQuery(id+"F0.wireOp",EDGE,"E65");Q1=makeQuery(id+"F0.imprint","IMPRINT",FACE,{"disambiguationData":[TD([[makeQuery(id+"F0.imprint","IMPRINT",EDGE,{"derivedFrom":subQ0}),1.0]])]});}
            var Q2;
            {var subQ0=sQuery(id+"F0.wireOp",EDGE,"E61");Q2=makeQuery(id+"F0.imprint","IMPRINT",FACE,{"disambiguationData":[TD([[makeQuery(id+"F0.imprint","IMPRINT",EDGE,{"derivedFrom":subQ0}),1.0]])]});}
            var Q3;
            Q3=makeQuery(id+"F0.imprint","IMPRINT",FACE,{"disambiguationData":[TD([[makeQuery(id+"F0.imprint","IMPRINT",EDGE,{"derivedFrom":sQuery(id+"F0.wireOp",EDGE,"E56")}),1.0]])]});
            var Q4;
            {var subQ0=sQuery(id+"F0.wireOp",EDGE,"E71");Q4=makeQuery(id+"F0.imprint","IMPRINT",FACE,{"disambiguationData":[TD([[makeQuery(id+"F0.imprint","IMPRINT",EDGE,{"derivedFrom":subQ0}),1.0]])]});}
            var Q5;
            {var subQ1=sQuery(id+"F0.wireOp",EDGE,"E85");Q5=makeQuery(id+"F0.imprint","IMPRINT",FACE,{"disambiguationData":[TD([[makeQuery(id+"F0.imprint","IMPRINT",EDGE,{"derivedFrom":subQ1}),1.0]])]});}
            var Q6;
            {var subQ0=sQuery(id+"F0.wireOp",EDGE,"E81");Q6=makeQuery(id+"F0.imprint","IMPRINT",FACE,{"disambiguationData":[TD([[makeQuery(id+"F0.imprint","IMPRINT",EDGE,{"derivedFrom":subQ0}),1.0]])]});}
            var Q7;
            Q7=makeQuery(id+"F0.imprint","IMPRINT",FACE,{"disambiguationData":[TD([[makeQuery(id+"F0.imprint","IMPRINT",EDGE,{"derivedFrom":sQuery(id+"F0.wireOp",EDGE,"E76")}),1.0]])]});
            var Q8;
            {var subQ0=sQuery(id+"F0.wireOp",EDGE,"E91");Q8=makeQuery(id+"F0.imprint","IMPRINT",FACE,{"disambiguationData":[TD([[makeQuery(id+"F0.imprint","IMPRINT",EDGE,{"derivedFrom":subQ0}),1.0]])]});}
            var Q9;
            Q9=makeQuery(id+"F0.imprint","IMPRINT",FACE,{"disambiguationData":[TD([[makeQuery(id+"F0.imprint","IMPRINT",EDGE,{"derivedFrom":sQuery(id+"F0.wireOp",EDGE,"E116")}),1.0]])]});
            var Q10;
            {var subQ0=sQuery(id+"F0.wireOp",EDGE,"E121");Q10=makeQuery(id+"F0.imprint","IMPRINT",FACE,{"disambiguationData":[TD([[makeQuery(id+"F0.imprint","IMPRINT",EDGE,{"derivedFrom":subQ0}),1.0]])]});}
            var Q11;
            {var subQ2=sQuery(id+"F0.wireOp",EDGE,"E125");Q11=makeQuery(id+"F0.imprint","IMPRINT",FACE,{"disambiguationData":[TD([[makeQuery(id+"F0.imprint","IMPRINT",EDGE,{"derivedFrom":subQ2}),1.0]])]});}
            var Q12;
            {var subQ0=sQuery(id+"F0.wireOp",EDGE,"E131");Q12=makeQuery(id+"F0.imprint","IMPRINT",FACE,{"disambiguationData":[TD([[makeQuery(id+"F0.imprint","IMPRINT",EDGE,{"derivedFrom":subQ0}),1.0]])]});}
            var Q13;
            {var subQ3=sQuery(id+"F0.wireOp",EDGE,"E145");Q13=makeQuery(id+"F0.imprint","IMPRINT",FACE,{"disambiguationData":[TD([[makeQuery(id+"F0.imprint","IMPRINT",EDGE,{"derivedFrom":subQ3}),1.0]])]});}
            var Q14;
            {var subQ0=sQuery(id+"F0.wireOp",EDGE,"E141");Q14=makeQuery(id+"F0.imprint","IMPRINT",FACE,{"disambiguationData":[TD([[makeQuery(id+"F0.imprint","IMPRINT",EDGE,{"derivedFrom":subQ0}),1.0]])]});}
            var Q15;
            {var subQ0=sQuery(id+"F0.wireOp",EDGE,"E151");Q15=makeQuery(id+"F0.imprint","IMPRINT",FACE,{"disambiguationData":[TD([[makeQuery(id+"F0.imprint","IMPRINT",EDGE,{"derivedFrom":subQ0}),1.0]])]});}
            var Q16;
            Q16=makeQuery(id+"F0.imprint","IMPRINT",FACE,{"disambiguationData":[TD([[makeQuery(id+"F0.imprint","IMPRINT",EDGE,{"derivedFrom":sQuery(id+"F0.wireOp",EDGE,"E136")}),1.0]])]});
            var Q17;
            Q17=makeQuery(id+"F0.imprint","IMPRINT",FACE,{"disambiguationData":[TD([[makeQuery(id+"F0.imprint","IMPRINT",EDGE,{"derivedFrom":sQuery(id+"F0.wireOp",EDGE,"E256")}),1.0]])]});
            var Q18;
            {var subQ0=sQuery(id+"F0.wireOp",EDGE,"E261");Q18=makeQuery(id+"F0.imprint","IMPRINT",FACE,{"disambiguationData":[TD([[makeQuery(id+"F0.imprint","IMPRINT",EDGE,{"derivedFrom":subQ0}),1.0]])]});}
            var Q19;
            {var subQ3=sQuery(id+"F0.wireOp",EDGE,"E265");Q19=makeQuery(id+"F0.imprint","IMPRINT",FACE,{"disambiguationData":[TD([[makeQuery(id+"F0.imprint","IMPRINT",EDGE,{"derivedFrom":subQ3}),1.0]])]});}
            var Q20;
            {var subQ0=sQuery(id+"F0.wireOp",EDGE,"E271");Q20=makeQuery(id+"F0.imprint","IMPRINT",FACE,{"disambiguationData":[TD([[makeQuery(id+"F0.imprint","IMPRINT",EDGE,{"derivedFrom":subQ0}),1.0]])]});}
            var Q21;
            Q21=makeQuery(id+"F0.imprint","IMPRINT",FACE,{"disambiguationData":[TD([[makeQuery(id+"F0.imprint","IMPRINT",EDGE,{"derivedFrom":sQuery(id+"F0.wireOp",EDGE,"E236")}),1.0]])]});
            var Q22;
            {var subQ0=sQuery(id+"F0.wireOp",EDGE,"E251");Q22=makeQuery(id+"F0.imprint","IMPRINT",FACE,{"disambiguationData":[TD([[makeQuery(id+"F0.imprint","IMPRINT",EDGE,{"derivedFrom":subQ0}),1.0]])]});}
            var Q23;
            {var subQ0=sQuery(id+"F0.wireOp",EDGE,"E241");Q23=makeQuery(id+"F0.imprint","IMPRINT",FACE,{"disambiguationData":[TD([[makeQuery(id+"F0.imprint","IMPRINT",EDGE,{"derivedFrom":subQ0}),1.0]])]});}
            var Q24;
            {var subQ3=sQuery(id+"F0.wireOp",EDGE,"E245");Q24=makeQuery(id+"F0.imprint","IMPRINT",FACE,{"disambiguationData":[TD([[makeQuery(id+"F0.imprint","IMPRINT",EDGE,{"derivedFrom":subQ3}),1.0]])]});}
            var Q25;
            Q25=makeQuery(id+"F0.imprint","IMPRINT",FACE,{"disambiguationData":[TD([[makeQuery(id+"F0.imprint","IMPRINT",EDGE,{"derivedFrom":sQuery(id+"F0.wireOp",EDGE,"E216")}),1.0]])]});
            var Q26;
            {var subQ0=sQuery(id+"F0.wireOp",EDGE,"E221");Q26=makeQuery(id+"F0.imprint","IMPRINT",FACE,{"disambiguationData":[TD([[makeQuery(id+"F0.imprint","IMPRINT",EDGE,{"derivedFrom":subQ0}),1.0]])]});}
            var Q27;
            {var subQ3=sQuery(id+"F0.wireOp",EDGE,"E225");Q27=makeQuery(id+"F0.imprint","IMPRINT",FACE,{"disambiguationData":[TD([[makeQuery(id+"F0.imprint","IMPRINT",EDGE,{"derivedFrom":subQ3}),1.0]])]});}
            var Q28;
            {var subQ0=sQuery(id+"F0.wireOp",EDGE,"E231");Q28=makeQuery(id+"F0.imprint","IMPRINT",FACE,{"disambiguationData":[TD([[makeQuery(id+"F0.imprint","IMPRINT",EDGE,{"derivedFrom":subQ0}),1.0]])]});}
            var Q29;
            {var subQ1=sQuery(id+"F0.wireOp",EDGE,"E105");Q29=makeQuery(id+"F0.imprint","IMPRINT",FACE,{"disambiguationData":[TD([[makeQuery(id+"F0.imprint","IMPRINT",EDGE,{"derivedFrom":subQ1}),1.0]])]});}
            var Q30;
            {var subQ0=sQuery(id+"F0.wireOp",EDGE,"E101");Q30=makeQuery(id+"F0.imprint","IMPRINT",FACE,{"disambiguationData":[TD([[makeQuery(id+"F0.imprint","IMPRINT",EDGE,{"derivedFrom":subQ0}),1.0]])]});}
            var Q31;
            {var subQ0=sQuery(id+"F0.wireOp",EDGE,"E111");Q31=makeQuery(id+"F0.imprint","IMPRINT",FACE,{"disambiguationData":[TD([[makeQuery(id+"F0.imprint","IMPRINT",EDGE,{"derivedFrom":subQ0}),1.0]])]});}
            var Q32;
            Q32=makeQuery(id+"F0.imprint","IMPRINT",FACE,{"disambiguationData":[TD([[makeQuery(id+"F0.imprint","IMPRINT",EDGE,{"derivedFrom":sQuery(id+"F0.wireOp",EDGE,"E96")}),1.0]])]});
            var Q33;
            Q33=makeQuery(id+"F0.imprint","IMPRINT",FACE,{"disambiguationData":[TD([[makeQuery(id+"F0.imprint","IMPRINT",EDGE,{"derivedFrom":sQuery(id+"F0.wireOp",EDGE,"E156")}),1.0]])]});
            var Q34;
            {var subQ0=sQuery(id+"F0.wireOp",EDGE,"E161");Q34=makeQuery(id+"F0.imprint","IMPRINT",FACE,{"disambiguationData":[TD([[makeQuery(id+"F0.imprint","IMPRINT",EDGE,{"derivedFrom":subQ0}),1.0]])]});}
            var Q35;
            {var subQ0=sQuery(id+"F0.wireOp",EDGE,"E165");Q35=makeQuery(id+"F0.imprint","IMPRINT",FACE,{"disambiguationData":[TD([[makeQuery(id+"F0.imprint","IMPRINT",EDGE,{"derivedFrom":subQ0}),1.0]])]});}
            var Q36;
            {var subQ0=sQuery(id+"F0.wireOp",EDGE,"E171");Q36=makeQuery(id+"F0.imprint","IMPRINT",FACE,{"disambiguationData":[TD([[makeQuery(id+"F0.imprint","IMPRINT",EDGE,{"derivedFrom":subQ0}),1.0]])]});}
            var Q37;
            Q37=makeQuery(id+"F0.imprint","IMPRINT",FACE,{"disambiguationData":[TD([[makeQuery(id+"F0.imprint","IMPRINT",EDGE,{"derivedFrom":sQuery(id+"F0.wireOp",EDGE,"E4")}),1.0]])]});
            var Q38;
            {var subQ2=sQuery(id+"F0.wireOp",EDGE,"E16");Q38=makeQuery(id+"F0.imprint","IMPRINT",FACE,{"disambiguationData":[TD([[makeQuery(id+"F0.imprint","IMPRINT",EDGE,{"derivedFrom":subQ2}),1.0]])]});}
            var Q39;
            Q39=makeQuery(id+"F0.imprint","IMPRINT",FACE,{"disambiguationData":[TD([[makeQuery(id+"F0.imprint","IMPRINT",EDGE,{"derivedFrom":sQuery(id+"F0.wireOp",EDGE,"E176")}),1.0]])]});
            var Q40;
            {var subQ0=sQuery(id+"F0.wireOp",EDGE,"E181");Q40=makeQuery(id+"F0.imprint","IMPRINT",FACE,{"disambiguationData":[TD([[makeQuery(id+"F0.imprint","IMPRINT",EDGE,{"derivedFrom":subQ0}),1.0]])]});}
            var Q41;
            {var subQ3=sQuery(id+"F0.wireOp",EDGE,"E185");Q41=makeQuery(id+"F0.imprint","IMPRINT",FACE,{"disambiguationData":[TD([[makeQuery(id+"F0.imprint","IMPRINT",EDGE,{"derivedFrom":subQ3}),1.0]])]});}
            var Q42;
            {var subQ0=sQuery(id+"F0.wireOp",EDGE,"E191");Q42=makeQuery(id+"F0.imprint","IMPRINT",FACE,{"disambiguationData":[TD([[makeQuery(id+"F0.imprint","IMPRINT",EDGE,{"derivedFrom":subQ0}),1.0]])]});}
            var Q43;
            {var subQ0=sQuery(id+"F0.wireOp",EDGE,"E205");Q43=makeQuery(id+"F0.imprint","IMPRINT",FACE,{"disambiguationData":[TD([[makeQuery(id+"F0.imprint","IMPRINT",EDGE,{"derivedFrom":subQ0}),1.0]])]});}
            var Q44;
            {var subQ0=sQuery(id+"F0.wireOp",EDGE,"E211");Q44=makeQuery(id+"F0.imprint","IMPRINT",FACE,{"disambiguationData":[TD([[makeQuery(id+"F0.imprint","IMPRINT",EDGE,{"derivedFrom":subQ0}),1.0]])]});}
            var Q45;
            {var subQ0=sQuery(id+"F0.wireOp",EDGE,"E201");Q45=makeQuery(id+"F0.imprint","IMPRINT",FACE,{"disambiguationData":[TD([[makeQuery(id+"F0.imprint","IMPRINT",EDGE,{"derivedFrom":subQ0}),1.0]])]});}
            var Q46;
            Q46=makeQuery(id+"F0.imprint","IMPRINT",FACE,{"disambiguationData":[TD([[makeQuery(id+"F0.imprint","IMPRINT",EDGE,{"derivedFrom":sQuery(id+"F0.wireOp",EDGE,"E196")}),1.0]])]});
            var Q47;
            Q47=makeQuery(id+"F0.imprint","IMPRINT",FACE,{"disambiguationData":[TD([[makeQuery(id+"F0.imprint","IMPRINT",EDGE,{"derivedFrom":sQuery(id+"F0.wireOp",EDGE,"E296")}),1.0]])]});
            var Q48;
            {var subQ0=sQuery(id+"F0.wireOp",EDGE,"E311");Q48=makeQuery(id+"F0.imprint","IMPRINT",FACE,{"disambiguationData":[TD([[makeQuery(id+"F0.imprint","IMPRINT",EDGE,{"derivedFrom":subQ0}),1.0]])]});}
            var Q49;
            {var subQ0=sQuery(id+"F0.wireOp",EDGE,"E301");Q49=makeQuery(id+"F0.imprint","IMPRINT",FACE,{"disambiguationData":[TD([[makeQuery(id+"F0.imprint","IMPRINT",EDGE,{"derivedFrom":subQ0}),1.0]])]});}
            var Q50;
            {var subQ1=sQuery(id+"F0.wireOp",EDGE,"E305");Q50=makeQuery(id+"F0.imprint","IMPRINT",FACE,{"disambiguationData":[TD([[makeQuery(id+"F0.imprint","IMPRINT",EDGE,{"derivedFrom":subQ1}),1.0]])]});}
            var Q51;
            Q51=makeQuery(id+"F0.imprint","IMPRINT",FACE,{"disambiguationData":[TD([[makeQuery(id+"F0.imprint","IMPRINT",EDGE,{"derivedFrom":sQuery(id+"F0.wireOp",EDGE,"E276")}),1.0]])]});
            var Q52;
            {var subQ0=sQuery(id+"F0.wireOp",EDGE,"E281");Q52=makeQuery(id+"F0.imprint","IMPRINT",FACE,{"disambiguationData":[TD([[makeQuery(id+"F0.imprint","IMPRINT",EDGE,{"derivedFrom":subQ0}),1.0]])]});}
            var Q53;
            {var subQ3=sQuery(id+"F0.wireOp",EDGE,"E285");Q53=makeQuery(id+"F0.imprint","IMPRINT",FACE,{"disambiguationData":[TD([[makeQuery(id+"F0.imprint","IMPRINT",EDGE,{"derivedFrom":subQ3}),1.0]])]});}
            var Q54;
            {var subQ0=sQuery(id+"F0.wireOp",EDGE,"E291");Q54=makeQuery(id+"F0.imprint","IMPRINT",FACE,{"disambiguationData":[TD([[makeQuery(id+"F0.imprint","IMPRINT",EDGE,{"derivedFrom":subQ0}),1.0]])]});}
            var Q55;
            Q55=makeQuery(id+"F0.imprint","IMPRINT",FACE,{"disambiguationData":[TD([[makeQuery(id+"F0.imprint","IMPRINT",EDGE,{"derivedFrom":sQuery(id+"F0.wireOp",EDGE,"E396")}),1.0]])]});
            var Q56;
            {var subQ0=sQuery(id+"F0.wireOp",EDGE,"E401");Q56=makeQuery(id+"F0.imprint","IMPRINT",FACE,{"disambiguationData":[TD([[makeQuery(id+"F0.imprint","IMPRINT",EDGE,{"derivedFrom":subQ0}),1.0]])]});}
            var Q57;
            {var subQ0=sQuery(id+"F0.wireOp",EDGE,"E405");Q57=makeQuery(id+"F0.imprint","IMPRINT",FACE,{"disambiguationData":[TD([[makeQuery(id+"F0.imprint","IMPRINT",EDGE,{"derivedFrom":subQ0}),1.0]])]});}
            var Q58;
            {var subQ0=sQuery(id+"F0.wireOp",EDGE,"E411");Q58=makeQuery(id+"F0.imprint","IMPRINT",FACE,{"disambiguationData":[TD([[makeQuery(id+"F0.imprint","IMPRINT",EDGE,{"derivedFrom":subQ0}),1.0]])]});}
            var Q59;
            Q59=makeQuery(id+"F0.imprint","IMPRINT",FACE,{"disambiguationData":[TD([[makeQuery(id+"F0.imprint","IMPRINT",EDGE,{"derivedFrom":sQuery(id+"F0.wireOp",EDGE,"E376")}),1.0]])]});
            var Q60;
            {var subQ0=sQuery(id+"F0.wireOp",EDGE,"E391");Q60=makeQuery(id+"F0.imprint","IMPRINT",FACE,{"disambiguationData":[TD([[makeQuery(id+"F0.imprint","IMPRINT",EDGE,{"derivedFrom":subQ0}),1.0]])]});}
            var Q61;
            {var subQ0=sQuery(id+"F0.wireOp",EDGE,"E381");Q61=makeQuery(id+"F0.imprint","IMPRINT",FACE,{"disambiguationData":[TD([[makeQuery(id+"F0.imprint","IMPRINT",EDGE,{"derivedFrom":subQ0}),1.0]])]});}
            var Q62;
            {var subQ1=sQuery(id+"F0.wireOp",EDGE,"E385");Q62=makeQuery(id+"F0.imprint","IMPRINT",FACE,{"disambiguationData":[TD([[makeQuery(id+"F0.imprint","IMPRINT",EDGE,{"derivedFrom":subQ1}),1.0]])]});}
            var Q63;
            Q63=makeQuery(id+"F0.imprint","IMPRINT",FACE,{"disambiguationData":[TD([[makeQuery(id+"F0.imprint","IMPRINT",EDGE,{"derivedFrom":sQuery(id+"F0.wireOp",EDGE,"E496")}),1.0]])]});
            var Q64;
            {var subQ0=sQuery(id+"F0.wireOp",EDGE,"E511");Q64=makeQuery(id+"F0.imprint","IMPRINT",FACE,{"disambiguationData":[TD([[makeQuery(id+"F0.imprint","IMPRINT",EDGE,{"derivedFrom":subQ0}),1.0]])]});}
            var Q65;
            {var subQ0=sQuery(id+"F0.wireOp",EDGE,"E501");Q65=makeQuery(id+"F0.imprint","IMPRINT",FACE,{"disambiguationData":[TD([[makeQuery(id+"F0.imprint","IMPRINT",EDGE,{"derivedFrom":subQ0}),1.0]])]});}
            var Q66;
            {var subQ0=sQuery(id+"F0.wireOp",EDGE,"E505");Q66=makeQuery(id+"F0.imprint","IMPRINT",FACE,{"disambiguationData":[TD([[makeQuery(id+"F0.imprint","IMPRINT",EDGE,{"derivedFrom":subQ0}),1.0]])]});}
            var Q67;
            Q67=makeQuery(id+"F0.imprint","IMPRINT",FACE,{"disambiguationData":[TD([[makeQuery(id+"F0.imprint","IMPRINT",EDGE,{"derivedFrom":sQuery(id+"F0.wireOp",EDGE,"E476")}),1.0]])]});
            var Q68;
            {var subQ0=sQuery(id+"F0.wireOp",EDGE,"E481");Q68=makeQuery(id+"F0.imprint","IMPRINT",FACE,{"disambiguationData":[TD([[makeQuery(id+"F0.imprint","IMPRINT",EDGE,{"derivedFrom":subQ0}),1.0]])]});}
            var Q69;
            {var subQ0=sQuery(id+"F0.wireOp",EDGE,"E491");Q69=makeQuery(id+"F0.imprint","IMPRINT",FACE,{"disambiguationData":[TD([[makeQuery(id+"F0.imprint","IMPRINT",EDGE,{"derivedFrom":subQ0}),1.0]])]});}
            var Q70;
            {var subQ1=sQuery(id+"F0.wireOp",EDGE,"E485");Q70=makeQuery(id+"F0.imprint","IMPRINT",FACE,{"disambiguationData":[TD([[makeQuery(id+"F0.imprint","IMPRINT",EDGE,{"derivedFrom":subQ1}),1.0]])]});}
            var Q71;
            Q71=makeQuery(id+"F0.imprint","IMPRINT",FACE,{"disambiguationData":[TD([[makeQuery(id+"F0.imprint","IMPRINT",EDGE,{"derivedFrom":sQuery(id+"F0.wireOp",EDGE,"E456")}),1.0]])]});
            var Q72;
            {var subQ0=sQuery(id+"F0.wireOp",EDGE,"E471");Q72=makeQuery(id+"F0.imprint","IMPRINT",FACE,{"disambiguationData":[TD([[makeQuery(id+"F0.imprint","IMPRINT",EDGE,{"derivedFrom":subQ0}),1.0]])]});}
            var Q73;
            {var subQ0=sQuery(id+"F0.wireOp",EDGE,"E461");Q73=makeQuery(id+"F0.imprint","IMPRINT",FACE,{"disambiguationData":[TD([[makeQuery(id+"F0.imprint","IMPRINT",EDGE,{"derivedFrom":subQ0}),1.0]])]});}
            var Q74;
            {var subQ3=sQuery(id+"F0.wireOp",EDGE,"E465");Q74=makeQuery(id+"F0.imprint","IMPRINT",FACE,{"disambiguationData":[TD([[makeQuery(id+"F0.imprint","IMPRINT",EDGE,{"derivedFrom":subQ3}),1.0]])]});}
            var Q75;
            Q75=makeQuery(id+"F0.imprint","IMPRINT",FACE,{"disambiguationData":[TD([[makeQuery(id+"F0.imprint","IMPRINT",EDGE,{"derivedFrom":sQuery(id+"F0.wireOp",EDGE,"E356")}),1.0]])]});
            var Q76;
            {var subQ0=sQuery(id+"F0.wireOp",EDGE,"E371");Q76=makeQuery(id+"F0.imprint","IMPRINT",FACE,{"disambiguationData":[TD([[makeQuery(id+"F0.imprint","IMPRINT",EDGE,{"derivedFrom":subQ0}),1.0]])]});}
            var Q77;
            {var subQ0=sQuery(id+"F0.wireOp",EDGE,"E361");Q77=makeQuery(id+"F0.imprint","IMPRINT",FACE,{"disambiguationData":[TD([[makeQuery(id+"F0.imprint","IMPRINT",EDGE,{"derivedFrom":subQ0}),1.0]])]});}
            var Q78;
            {var subQ1=sQuery(id+"F0.wireOp",EDGE,"E365");Q78=makeQuery(id+"F0.imprint","IMPRINT",FACE,{"disambiguationData":[TD([[makeQuery(id+"F0.imprint","IMPRINT",EDGE,{"derivedFrom":subQ1}),1.0]])]});}
            var Q79;
            Q79=makeQuery(id+"F0.imprint","IMPRINT",FACE,{"disambiguationData":[TD([[makeQuery(id+"F0.imprint","IMPRINT",EDGE,{"derivedFrom":sQuery(id+"F0.wireOp",EDGE,"E336")}),1.0]])]});
            var Q80;
            {var subQ0=sQuery(id+"F0.wireOp",EDGE,"E341");Q80=makeQuery(id+"F0.imprint","IMPRINT",FACE,{"disambiguationData":[TD([[makeQuery(id+"F0.imprint","IMPRINT",EDGE,{"derivedFrom":subQ0}),1.0]])]});}
            var Q81;
            {var subQ0=sQuery(id+"F0.wireOp",EDGE,"E345");Q81=makeQuery(id+"F0.imprint","IMPRINT",FACE,{"disambiguationData":[TD([[makeQuery(id+"F0.imprint","IMPRINT",EDGE,{"derivedFrom":subQ0}),1.0]])]});}
            var Q82;
            {var subQ0=sQuery(id+"F0.wireOp",EDGE,"E351");Q82=makeQuery(id+"F0.imprint","IMPRINT",FACE,{"disambiguationData":[TD([[makeQuery(id+"F0.imprint","IMPRINT",EDGE,{"derivedFrom":subQ0}),1.0]])]});}
            var Q83;
            Q83=makeQuery(id+"F0.imprint","IMPRINT",FACE,{"disambiguationData":[TD([[makeQuery(id+"F0.imprint","IMPRINT",EDGE,{"derivedFrom":sQuery(id+"F0.wireOp",EDGE,"E436")}),1.0]])]});
            var Q84;
            {var subQ0=sQuery(id+"F0.wireOp",EDGE,"E441");Q84=makeQuery(id+"F0.imprint","IMPRINT",FACE,{"disambiguationData":[TD([[makeQuery(id+"F0.imprint","IMPRINT",EDGE,{"derivedFrom":subQ0}),1.0]])]});}
            var Q85;
            {var subQ0=sQuery(id+"F0.wireOp",EDGE,"E451");Q85=makeQuery(id+"F0.imprint","IMPRINT",FACE,{"disambiguationData":[TD([[makeQuery(id+"F0.imprint","IMPRINT",EDGE,{"derivedFrom":subQ0}),1.0]])]});}
            var Q86;
            {var subQ3=sQuery(id+"F0.wireOp",EDGE,"E445");Q86=makeQuery(id+"F0.imprint","IMPRINT",FACE,{"disambiguationData":[TD([[makeQuery(id+"F0.imprint","IMPRINT",EDGE,{"derivedFrom":subQ3}),1.0]])]});}
            var Q87;
            Q87=makeQuery(id+"F0.imprint","IMPRINT",FACE,{"disambiguationData":[TD([[makeQuery(id+"F0.imprint","IMPRINT",EDGE,{"derivedFrom":sQuery(id+"F0.wireOp",EDGE,"E416")}),1.0]])]});
            var Q88;
            {var subQ0=sQuery(id+"F0.wireOp",EDGE,"E431");Q88=makeQuery(id+"F0.imprint","IMPRINT",FACE,{"disambiguationData":[TD([[makeQuery(id+"F0.imprint","IMPRINT",EDGE,{"derivedFrom":subQ0}),1.0]])]});}
            var Q89;
            {var subQ0=sQuery(id+"F0.wireOp",EDGE,"E421");Q89=makeQuery(id+"F0.imprint","IMPRINT",FACE,{"disambiguationData":[TD([[makeQuery(id+"F0.imprint","IMPRINT",EDGE,{"derivedFrom":subQ0}),1.0]])]});}
            var Q90;
            {var subQ0=sQuery(id+"F0.wireOp",EDGE,"E425");Q90=makeQuery(id+"F0.imprint","IMPRINT",FACE,{"disambiguationData":[TD([[makeQuery(id+"F0.imprint","IMPRINT",EDGE,{"derivedFrom":subQ0}),1.0]])]});}
            var Q91;
            {var subQ1=sQuery(id+"F0.wireOp",EDGE,"E325");Q91=makeQuery(id+"F0.imprint","IMPRINT",FACE,{"disambiguationData":[TD([[makeQuery(id+"F0.imprint","IMPRINT",EDGE,{"derivedFrom":subQ1}),1.0]])]});}
            var Q92;
            {var subQ0=sQuery(id+"F0.wireOp",EDGE,"E331");Q92=makeQuery(id+"F0.imprint","IMPRINT",FACE,{"disambiguationData":[TD([[makeQuery(id+"F0.imprint","IMPRINT",EDGE,{"derivedFrom":subQ0}),1.0]])]});}
            var Q93;
            {var subQ0=sQuery(id+"F0.wireOp",EDGE,"E321");Q93=makeQuery(id+"F0.imprint","IMPRINT",FACE,{"disambiguationData":[TD([[makeQuery(id+"F0.imprint","IMPRINT",EDGE,{"derivedFrom":subQ0}),1.0]])]});}
            var Q94;
            Q94=makeQuery(id+"F0.imprint","IMPRINT",FACE,{"disambiguationData":[TD([[makeQuery(id+"F0.imprint","IMPRINT",EDGE,{"derivedFrom":sQuery(id+"F0.wireOp",EDGE,"E316")}),1.0]])]});
            var Q95;
            {var subQ3=sQuery(id+"F0.wireOp",EDGE,"E525");Q95=makeQuery(id+"F0.imprint","IMPRINT",FACE,{"disambiguationData":[TD([[makeQuery(id+"F0.imprint","IMPRINT",EDGE,{"derivedFrom":subQ3}),1.0]])]});}
            var Q96;
            {var subQ0=sQuery(id+"F0.wireOp",EDGE,"E521");Q96=makeQuery(id+"F0.imprint","IMPRINT",FACE,{"disambiguationData":[TD([[makeQuery(id+"F0.imprint","IMPRINT",EDGE,{"derivedFrom":subQ0}),1.0]])]});}
            var Q97;
            Q97=makeQuery(id+"F0.imprint","IMPRINT",FACE,{"disambiguationData":[TD([[makeQuery(id+"F0.imprint","IMPRINT",EDGE,{"derivedFrom":sQuery(id+"F0.wireOp",EDGE,"E516")}),1.0]])]});
            var Q98;
            {var subQ0=sQuery(id+"F0.wireOp",EDGE,"E531");Q98=makeQuery(id+"F0.imprint","IMPRINT",FACE,{"disambiguationData":[TD([[makeQuery(id+"F0.imprint","IMPRINT",EDGE,{"derivedFrom":subQ0}),1.0]])]});}
            var Q99;
            {var subQ0=sQuery(id+"F0.wireOp",EDGE,"E621");Q99=makeQuery(id+"F0.imprint","IMPRINT",FACE,{"disambiguationData":[TD([[makeQuery(id+"F0.imprint","IMPRINT",EDGE,{"derivedFrom":subQ0}),1.0]])]});}
            var Q100;
            {var subQ0=sQuery(id+"F0.wireOp",EDGE,"E625");Q100=makeQuery(id+"F0.imprint","IMPRINT",FACE,{"disambiguationData":[TD([[makeQuery(id+"F0.imprint","IMPRINT",EDGE,{"derivedFrom":subQ0}),1.0]])]});}
            var Q101;
            {var subQ0=sQuery(id+"F0.wireOp",EDGE,"E631");Q101=makeQuery(id+"F0.imprint","IMPRINT",FACE,{"disambiguationData":[TD([[makeQuery(id+"F0.imprint","IMPRINT",EDGE,{"derivedFrom":subQ0}),1.0]])]});}
            var Q102;
            Q102=makeQuery(id+"F0.imprint","IMPRINT",FACE,{"disambiguationData":[TD([[makeQuery(id+"F0.imprint","IMPRINT",EDGE,{"derivedFrom":sQuery(id+"F0.wireOp",EDGE,"E616")}),1.0]])]});
            var Q103;
            Q103=makeQuery(id+"F0.imprint","IMPRINT",FACE,{"disambiguationData":[TD([[makeQuery(id+"F0.imprint","IMPRINT",EDGE,{"derivedFrom":sQuery(id+"F0.wireOp",EDGE,"E716")}),1.0]])]});
            var Q104;
            {var subQ0=sQuery(id+"F0.wireOp",EDGE,"E721");Q104=makeQuery(id+"F0.imprint","IMPRINT",FACE,{"disambiguationData":[TD([[makeQuery(id+"F0.imprint","IMPRINT",EDGE,{"derivedFrom":subQ0}),1.0]])]});}
            var Q105;
            {var subQ1=sQuery(id+"F0.wireOp",EDGE,"E725");Q105=makeQuery(id+"F0.imprint","IMPRINT",FACE,{"disambiguationData":[TD([[makeQuery(id+"F0.imprint","IMPRINT",EDGE,{"derivedFrom":subQ1}),1.0]])]});}
            var Q106;
            {var subQ0=sQuery(id+"F0.wireOp",EDGE,"E731");Q106=makeQuery(id+"F0.imprint","IMPRINT",FACE,{"disambiguationData":[TD([[makeQuery(id+"F0.imprint","IMPRINT",EDGE,{"derivedFrom":subQ0}),1.0]])]});}
            var Q107;
            {var subQ0=sQuery(id+"F0.wireOp",EDGE,"E853");Q107=makeQuery(id+"F0.imprint","IMPRINT",FACE,{"disambiguationData":[TD([[makeQuery(id+"F0.imprint","IMPRINT",EDGE,{"derivedFrom":subQ0}),1.0]])]});}
            var Q108;
            {var subQ1=sQuery(id+"F0.wireOp",EDGE,"E857");Q108=makeQuery(id+"F0.imprint","IMPRINT",FACE,{"disambiguationData":[TD([[makeQuery(id+"F0.imprint","IMPRINT",EDGE,{"derivedFrom":subQ1}),1.0]])]});}
            var Q109;
            {var subQ0=sQuery(id+"F0.wireOp",EDGE,"E863");Q109=makeQuery(id+"F0.imprint","IMPRINT",FACE,{"disambiguationData":[TD([[makeQuery(id+"F0.imprint","IMPRINT",EDGE,{"derivedFrom":subQ0}),1.0]])]});}
            var Q110;
            Q110=makeQuery(id+"F0.imprint","IMPRINT",FACE,{"disambiguationData":[TD([[makeQuery(id+"F0.imprint","IMPRINT",EDGE,{"derivedFrom":sQuery(id+"F0.wireOp",EDGE,"E848")}),1.0]])]});
            var Q111;
            {var subQ3=sQuery(id+"F0.wireOp",EDGE,"E877");Q111=makeQuery(id+"F0.imprint","IMPRINT",FACE,{"disambiguationData":[TD([[makeQuery(id+"F0.imprint","IMPRINT",EDGE,{"derivedFrom":subQ3}),1.0]])]});}
            var Q112;
            {var subQ0=sQuery(id+"F0.wireOp",EDGE,"E883");Q112=makeQuery(id+"F0.imprint","IMPRINT",FACE,{"disambiguationData":[TD([[makeQuery(id+"F0.imprint","IMPRINT",EDGE,{"derivedFrom":subQ0}),1.0]])]});}
            var Q113;
            Q113=makeQuery(id+"F0.imprint","IMPRINT",FACE,{"disambiguationData":[TD([[makeQuery(id+"F0.imprint","IMPRINT",EDGE,{"derivedFrom":sQuery(id+"F0.wireOp",EDGE,"E868")}),1.0]])]});
            var Q114;
            {var subQ0=sQuery(id+"F0.wireOp",EDGE,"E873");Q114=makeQuery(id+"F0.imprint","IMPRINT",FACE,{"disambiguationData":[TD([[makeQuery(id+"F0.imprint","IMPRINT",EDGE,{"derivedFrom":subQ0}),1.0]])]});}
            var Q115;
            {var subQ1=sQuery(id+"F0.wireOp",EDGE,"E897");Q115=makeQuery(id+"F0.imprint","IMPRINT",FACE,{"disambiguationData":[TD([[makeQuery(id+"F0.imprint","IMPRINT",EDGE,{"derivedFrom":subQ1}),1.0]])]});}
            var Q116;
            {var subQ0=sQuery(id+"F0.wireOp",EDGE,"E893");Q116=makeQuery(id+"F0.imprint","IMPRINT",FACE,{"disambiguationData":[TD([[makeQuery(id+"F0.imprint","IMPRINT",EDGE,{"derivedFrom":subQ0}),1.0]])]});}
            var Q117;
            Q117=makeQuery(id+"F0.imprint","IMPRINT",FACE,{"disambiguationData":[TD([[makeQuery(id+"F0.imprint","IMPRINT",EDGE,{"derivedFrom":sQuery(id+"F0.wireOp",EDGE,"E888")}),1.0]])]});
            var Q118;
            {var subQ0=sQuery(id+"F0.wireOp",EDGE,"E903");Q118=makeQuery(id+"F0.imprint","IMPRINT",FACE,{"disambiguationData":[TD([[makeQuery(id+"F0.imprint","IMPRINT",EDGE,{"derivedFrom":subQ0}),1.0]])]});}
            var Q119;
            {var subQ0=sQuery(id+"F0.wireOp",EDGE,"E751");Q119=makeQuery(id+"F0.imprint","IMPRINT",FACE,{"disambiguationData":[TD([[makeQuery(id+"F0.imprint","IMPRINT",EDGE,{"derivedFrom":subQ0}),1.0]])]});}
            var Q120;
            {var subQ3=sQuery(id+"F0.wireOp",EDGE,"E745");Q120=makeQuery(id+"F0.imprint","IMPRINT",FACE,{"disambiguationData":[TD([[makeQuery(id+"F0.imprint","IMPRINT",EDGE,{"derivedFrom":subQ3}),1.0]])]});}
            var Q121;
            {var subQ0=sQuery(id+"F0.wireOp",EDGE,"E741");Q121=makeQuery(id+"F0.imprint","IMPRINT",FACE,{"disambiguationData":[TD([[makeQuery(id+"F0.imprint","IMPRINT",EDGE,{"derivedFrom":subQ0}),1.0]])]});}
            var Q122;
            Q122=makeQuery(id+"F0.imprint","IMPRINT",FACE,{"disambiguationData":[TD([[makeQuery(id+"F0.imprint","IMPRINT",EDGE,{"derivedFrom":sQuery(id+"F0.wireOp",EDGE,"E736")}),1.0]])]});
            var Q123;
            {var subQ2=sQuery(id+"F0.wireOp",EDGE,"E765");Q123=makeQuery(id+"F0.imprint","IMPRINT",FACE,{"disambiguationData":[TD([[makeQuery(id+"F0.imprint","IMPRINT",EDGE,{"derivedFrom":subQ2}),1.0]])]});}
            var Q124;
            {var subQ0=sQuery(id+"F0.wireOp",EDGE,"E761");Q124=makeQuery(id+"F0.imprint","IMPRINT",FACE,{"disambiguationData":[TD([[makeQuery(id+"F0.imprint","IMPRINT",EDGE,{"derivedFrom":subQ0}),1.0]])]});}
            var Q125;
            Q125=makeQuery(id+"F0.imprint","IMPRINT",FACE,{"disambiguationData":[TD([[makeQuery(id+"F0.imprint","IMPRINT",EDGE,{"derivedFrom":sQuery(id+"F0.wireOp",EDGE,"E756")}),1.0]])]});
            var Q126;
            {var subQ0=sQuery(id+"F0.wireOp",EDGE,"E771");Q126=makeQuery(id+"F0.imprint","IMPRINT",FACE,{"disambiguationData":[TD([[makeQuery(id+"F0.imprint","IMPRINT",EDGE,{"derivedFrom":subQ0}),1.0]])]});}
            var Q127;
            {var subQ0=sQuery(id+"F0.wireOp",EDGE,"E665");Q127=makeQuery(id+"F0.imprint","IMPRINT",FACE,{"disambiguationData":[TD([[makeQuery(id+"F0.imprint","IMPRINT",EDGE,{"derivedFrom":subQ0}),1.0]])]});}
            var Q128;
            {var subQ0=sQuery(id+"F0.wireOp",EDGE,"E671");Q128=makeQuery(id+"F0.imprint","IMPRINT",FACE,{"disambiguationData":[TD([[makeQuery(id+"F0.imprint","IMPRINT",EDGE,{"derivedFrom":subQ0}),1.0]])]});}
            var Q129;
            {var subQ0=sQuery(id+"F0.wireOp",EDGE,"E661");Q129=makeQuery(id+"F0.imprint","IMPRINT",FACE,{"disambiguationData":[TD([[makeQuery(id+"F0.imprint","IMPRINT",EDGE,{"derivedFrom":subQ0}),1.0]])]});}
            var Q130;
            Q130=makeQuery(id+"F0.imprint","IMPRINT",FACE,{"disambiguationData":[TD([[makeQuery(id+"F0.imprint","IMPRINT",EDGE,{"derivedFrom":sQuery(id+"F0.wireOp",EDGE,"E656")}),1.0]])]});
            var Q131;
            Q131=makeQuery(id+"F0.imprint","IMPRINT",FACE,{"disambiguationData":[TD([[makeQuery(id+"F0.imprint","IMPRINT",EDGE,{"derivedFrom":sQuery(id+"F0.wireOp",EDGE,"E636")}),1.0]])]});
            var Q132;
            {var subQ0=sQuery(id+"F0.wireOp",EDGE,"E641");Q132=makeQuery(id+"F0.imprint","IMPRINT",FACE,{"disambiguationData":[TD([[makeQuery(id+"F0.imprint","IMPRINT",EDGE,{"derivedFrom":subQ0}),1.0]])]});}
            var Q133;
            {var subQ1=sQuery(id+"F0.wireOp",EDGE,"E645");Q133=makeQuery(id+"F0.imprint","IMPRINT",FACE,{"disambiguationData":[TD([[makeQuery(id+"F0.imprint","IMPRINT",EDGE,{"derivedFrom":subQ1}),1.0]])]});}
            var Q134;
            {var subQ0=sQuery(id+"F0.wireOp",EDGE,"E651");Q134=makeQuery(id+"F0.imprint","IMPRINT",FACE,{"disambiguationData":[TD([[makeQuery(id+"F0.imprint","IMPRINT",EDGE,{"derivedFrom":subQ0}),1.0]])]});}
            var Q135;
            {var subQ0=sQuery(id+"F0.wireOp",EDGE,"E545");Q135=makeQuery(id+"F0.imprint","IMPRINT",FACE,{"disambiguationData":[TD([[makeQuery(id+"F0.imprint","IMPRINT",EDGE,{"derivedFrom":subQ0}),1.0]])]});}
            var Q136;
            {var subQ0=sQuery(id+"F0.wireOp",EDGE,"E541");Q136=makeQuery(id+"F0.imprint","IMPRINT",FACE,{"disambiguationData":[TD([[makeQuery(id+"F0.imprint","IMPRINT",EDGE,{"derivedFrom":subQ0}),1.0]])]});}
            var Q137;
            Q137=makeQuery(id+"F0.imprint","IMPRINT",FACE,{"disambiguationData":[TD([[makeQuery(id+"F0.imprint","IMPRINT",EDGE,{"derivedFrom":sQuery(id+"F0.wireOp",EDGE,"E536")}),1.0]])]});
            var Q138;
            {var subQ0=sQuery(id+"F0.wireOp",EDGE,"E551");Q138=makeQuery(id+"F0.imprint","IMPRINT",FACE,{"disambiguationData":[TD([[makeQuery(id+"F0.imprint","IMPRINT",EDGE,{"derivedFrom":subQ0}),1.0]])]});}
            var Q139;
            {var subQ1=sQuery(id+"F0.wireOp",EDGE,"E565");Q139=makeQuery(id+"F0.imprint","IMPRINT",FACE,{"disambiguationData":[TD([[makeQuery(id+"F0.imprint","IMPRINT",EDGE,{"derivedFrom":subQ1}),1.0]])]});}
            var Q140;
            {var subQ0=sQuery(id+"F0.wireOp",EDGE,"E561");Q140=makeQuery(id+"F0.imprint","IMPRINT",FACE,{"disambiguationData":[TD([[makeQuery(id+"F0.imprint","IMPRINT",EDGE,{"derivedFrom":subQ0}),1.0]])]});}
            var Q141;
            Q141=makeQuery(id+"F0.imprint","IMPRINT",FACE,{"disambiguationData":[TD([[makeQuery(id+"F0.imprint","IMPRINT",EDGE,{"derivedFrom":sQuery(id+"F0.wireOp",EDGE,"E556")}),1.0]])]});
            var Q142;
            {var subQ0=sQuery(id+"F0.wireOp",EDGE,"E571");Q142=makeQuery(id+"F0.imprint","IMPRINT",FACE,{"disambiguationData":[TD([[makeQuery(id+"F0.imprint","IMPRINT",EDGE,{"derivedFrom":subQ0}),1.0]])]});}
            var Q143;
            {var subQ0=sQuery(id+"F0.wireOp",EDGE,"E585");Q143=makeQuery(id+"F0.imprint","IMPRINT",FACE,{"disambiguationData":[TD([[makeQuery(id+"F0.imprint","IMPRINT",EDGE,{"derivedFrom":subQ0}),1.0]])]});}
            var Q144;
            {var subQ0=sQuery(id+"F0.wireOp",EDGE,"E591");Q144=makeQuery(id+"F0.imprint","IMPRINT",FACE,{"disambiguationData":[TD([[makeQuery(id+"F0.imprint","IMPRINT",EDGE,{"derivedFrom":subQ0}),1.0]])]});}
            var Q145;
            {var subQ0=sQuery(id+"F0.wireOp",EDGE,"E581");Q145=makeQuery(id+"F0.imprint","IMPRINT",FACE,{"disambiguationData":[TD([[makeQuery(id+"F0.imprint","IMPRINT",EDGE,{"derivedFrom":subQ0}),1.0]])]});}
            var Q146;
            Q146=makeQuery(id+"F0.imprint","IMPRINT",FACE,{"disambiguationData":[TD([[makeQuery(id+"F0.imprint","IMPRINT",EDGE,{"derivedFrom":sQuery(id+"F0.wireOp",EDGE,"E576")}),1.0]])]});
            var Q147;
            {var subQ1=sQuery(id+"F0.wireOp",EDGE,"E605");Q147=makeQuery(id+"F0.imprint","IMPRINT",FACE,{"disambiguationData":[TD([[makeQuery(id+"F0.imprint","IMPRINT",EDGE,{"derivedFrom":subQ1}),1.0]])]});}
            var Q148;
            {var subQ0=sQuery(id+"F0.wireOp",EDGE,"E601");Q148=makeQuery(id+"F0.imprint","IMPRINT",FACE,{"disambiguationData":[TD([[makeQuery(id+"F0.imprint","IMPRINT",EDGE,{"derivedFrom":subQ0}),1.0]])]});}
            var Q149;
            Q149=makeQuery(id+"F0.imprint","IMPRINT",FACE,{"disambiguationData":[TD([[makeQuery(id+"F0.imprint","IMPRINT",EDGE,{"derivedFrom":sQuery(id+"F0.wireOp",EDGE,"E596")}),1.0]])]});
            var Q150;
            {var subQ0=sQuery(id+"F0.wireOp",EDGE,"E611");Q150=makeQuery(id+"F0.imprint","IMPRINT",FACE,{"disambiguationData":[TD([[makeQuery(id+"F0.imprint","IMPRINT",EDGE,{"derivedFrom":subQ0}),1.0]])]});}
            var Q151;
            {var subQ0=sQuery(id+"F0.wireOp",EDGE,"E701");Q151=makeQuery(id+"F0.imprint","IMPRINT",FACE,{"disambiguationData":[TD([[makeQuery(id+"F0.imprint","IMPRINT",EDGE,{"derivedFrom":subQ0}),1.0]])]});}
            var Q152;
            {var subQ3=sQuery(id+"F0.wireOp",EDGE,"E705");Q152=makeQuery(id+"F0.imprint","IMPRINT",FACE,{"disambiguationData":[TD([[makeQuery(id+"F0.imprint","IMPRINT",EDGE,{"derivedFrom":subQ3}),1.0]])]});}
            var Q153;
            Q153=makeQuery(id+"F0.imprint","IMPRINT",FACE,{"disambiguationData":[TD([[makeQuery(id+"F0.imprint","IMPRINT",EDGE,{"derivedFrom":sQuery(id+"F0.wireOp",EDGE,"E696")}),1.0]])]});
            var Q154;
            {var subQ0=sQuery(id+"F0.wireOp",EDGE,"E711");Q154=makeQuery(id+"F0.imprint","IMPRINT",FACE,{"disambiguationData":[TD([[makeQuery(id+"F0.imprint","IMPRINT",EDGE,{"derivedFrom":subQ0}),1.0]])]});}
            var Q155;
            {var subQ0=sQuery(id+"F0.wireOp",EDGE,"E691");Q155=makeQuery(id+"F0.imprint","IMPRINT",FACE,{"disambiguationData":[TD([[makeQuery(id+"F0.imprint","IMPRINT",EDGE,{"derivedFrom":subQ0}),1.0]])]});}
            var Q156;
            {var subQ4=sQuery(id+"F0.wireOp",EDGE,"E685");Q156=makeQuery(id+"F0.imprint","IMPRINT",FACE,{"disambiguationData":[TD([[makeQuery(id+"F0.imprint","IMPRINT",EDGE,{"derivedFrom":subQ4}),1.0]])]});}
            var Q157;
            {var subQ0=sQuery(id+"F0.wireOp",EDGE,"E681");Q157=makeQuery(id+"F0.imprint","IMPRINT",FACE,{"disambiguationData":[TD([[makeQuery(id+"F0.imprint","IMPRINT",EDGE,{"derivedFrom":subQ0}),1.0]])]});}
            var Q158;
            Q158=makeQuery(id+"F0.imprint","IMPRINT",FACE,{"disambiguationData":[TD([[makeQuery(id+"F0.imprint","IMPRINT",EDGE,{"derivedFrom":sQuery(id+"F0.wireOp",EDGE,"E676")}),1.0]])]});
            var Q159;
            {var subQ0=sQuery(id+"F0.wireOp",EDGE,"E781");Q159=makeQuery(id+"F0.imprint","IMPRINT",FACE,{"disambiguationData":[TD([[makeQuery(id+"F0.imprint","IMPRINT",EDGE,{"derivedFrom":subQ0}),1.0]])]});}
            var Q160;
            {var subQ1=sQuery(id+"F0.wireOp",EDGE,"E785");Q160=makeQuery(id+"F0.imprint","IMPRINT",FACE,{"disambiguationData":[TD([[makeQuery(id+"F0.imprint","IMPRINT",EDGE,{"derivedFrom":subQ1}),1.0]])]});}
            var Q161;
            {var subQ0=sQuery(id+"F0.wireOp",EDGE,"E791");Q161=makeQuery(id+"F0.imprint","IMPRINT",FACE,{"disambiguationData":[TD([[makeQuery(id+"F0.imprint","IMPRINT",EDGE,{"derivedFrom":subQ0}),1.0]])]});}
            var Q162;
            Q162=makeQuery(id+"F0.imprint","IMPRINT",FACE,{"disambiguationData":[TD([[makeQuery(id+"F0.imprint","IMPRINT",EDGE,{"derivedFrom":sQuery(id+"F0.wireOp",EDGE,"E776")}),1.0]])]});
            var Q163;
            {var subQ0=sQuery(id+"F0.wireOp",EDGE,"E821");Q163=makeQuery(id+"F0.imprint","IMPRINT",FACE,{"disambiguationData":[TD([[makeQuery(id+"F0.imprint","IMPRINT",EDGE,{"derivedFrom":subQ0}),1.0]])]});}
            var Q164;
            {var subQ2=sQuery(id+"F0.wireOp",EDGE,"E797");Q164=makeQuery(id+"F0.imprint","IMPRINT",FACE,{"disambiguationData":[TD([[makeQuery(id+"F0.imprint","IMPRINT",EDGE,{"derivedFrom":subQ2}),1.0]])]});}
            var Q165;
            {var subQ3=sQuery(id+"F0.wireOp",EDGE,"E917");Q165=makeQuery(id+"F0.imprint","IMPRINT",FACE,{"disambiguationData":[TD([[makeQuery(id+"F0.imprint","IMPRINT",EDGE,{"derivedFrom":subQ3}),1.0]])]});}
            var Q166;
            {var subQ0=sQuery(id+"F0.wireOp",EDGE,"E923");Q166=makeQuery(id+"F0.imprint","IMPRINT",FACE,{"disambiguationData":[TD([[makeQuery(id+"F0.imprint","IMPRINT",EDGE,{"derivedFrom":subQ0}),1.0]])]});}
            var Q167;
            {var subQ0=sQuery(id+"F0.wireOp",EDGE,"E913");Q167=makeQuery(id+"F0.imprint","IMPRINT",FACE,{"disambiguationData":[TD([[makeQuery(id+"F0.imprint","IMPRINT",EDGE,{"derivedFrom":subQ0}),1.0]])]});}
            var Q168;
            Q168=makeQuery(id+"F0.imprint","IMPRINT",FACE,{"disambiguationData":[TD([[makeQuery(id+"F0.imprint","IMPRINT",EDGE,{"derivedFrom":sQuery(id+"F0.wireOp",EDGE,"E908")}),1.0]])]});
            extrude(context, id + "F1", {"entities" : qUnion([Q0, Q1, Q2, Q3, Q4, Q5, Q6, Q7, Q8, Q9, Q10, Q11, Q12, Q13, Q14, Q15, Q16, Q17, Q18, Q19, Q20, Q21, Q22, Q23, Q24, Q25, Q26, Q27, Q28, Q29, Q30, Q31, Q32, Q33, Q34, Q35, Q36, Q37, Q38, Q39, Q40, Q41, Q42, Q43, Q44, Q45, Q46, Q47, Q48, Q49, Q50, Q51, Q52, Q53, Q54, Q55, Q56, Q57, Q58, Q59, Q60, Q61, Q62, Q63, Q64, Q65, Q66, Q67, Q68, Q69, Q70, Q71, Q72, Q73, Q74, Q75, Q76, Q77, Q78, Q79, Q80, Q81, Q82, Q83, Q84, Q85, Q86, Q87, Q88, Q89, Q90, Q91, Q92, Q93, Q94, Q95, Q96, Q97, Q98, Q99, Q100, Q101, Q102, Q103, Q104, Q105, Q106, Q107, Q108, Q109, Q110, Q111, Q112, Q113, Q114, Q115, Q116, Q117, Q118, Q119, Q120, Q121, Q122, Q123, Q124, Q125, Q126, Q127, Q128, Q129, Q130, Q131, Q132, Q133, Q134, Q135, Q136, Q137, Q138, Q139, Q140, Q141, Q142, Q143, Q144, Q145, Q146, Q147, Q148, Q149, Q150, Q151, Q152, Q153, Q154, Q155, Q156, Q157, Q158, Q159, Q160, Q161, Q162, Q163, Q164, Q165, Q166, Q167, Q168]), "depth" : 1.5 * mm});
        }
        {
            var Q0;
            Q0=qSketchRegion(id+"F0",true);
            extrude(context, id + "F2", {"entities" : qUnion([Q0]), "operationType" : NewBodyOperationType.ADD, "depth" : 3 * mm});
        }
        {
            var Q0;
            {var subQ0=sQuery(id+"F0.wireOp",EDGE,"E3");var subQ1=sQuery(id+"F0.wireOp",EDGE,"E2");Q0=makeQuery(id+"F2.boolean.opBoolean","MERGE",EDGE,{"derivedFrom":[makeQuery(id+"F1.opExtrude","SWEPT_EDGE",EDGE,{"disambiguationData":[OSD([subQ1,subQ0])]}),makeQuery(id+"F2.opExtrude","SWEPT_EDGE",EDGE,{"disambiguationData":[OSD([subQ1,subQ0])]})]});}
            var Q1;
            {var subQ0=sQuery(id+"F0.wireOp",EDGE,"E3");var subQ1=sQuery(id+"F0.wireOp",EDGE,"E0");Q1=makeQuery(id+"F2.boolean.opBoolean","MERGE",EDGE,{"derivedFrom":[makeQuery(id+"F1.opExtrude","SWEPT_EDGE",EDGE,{"disambiguationData":[OSD([subQ1,subQ0])]}),makeQuery(id+"F2.opExtrude","SWEPT_EDGE",EDGE,{"disambiguationData":[OSD([subQ1,subQ0])]})]});}
            var Q2;
            {var subQ0=sQuery(id+"F0.wireOp",EDGE,"E1");var subQ1=sQuery(id+"F0.wireOp",EDGE,"E0");Q2=makeQuery(id+"F2.boolean.opBoolean","MERGE",EDGE,{"derivedFrom":[makeQuery(id+"F1.opExtrude","SWEPT_EDGE",EDGE,{"disambiguationData":[OSD([subQ1,subQ0])]}),makeQuery(id+"F2.opExtrude","SWEPT_EDGE",EDGE,{"disambiguationData":[OSD([subQ1,subQ0])]})]});}
            var Q3;
            {var subQ0=sQuery(id+"F0.wireOp",EDGE,"E2");var subQ1=sQuery(id+"F0.wireOp",EDGE,"E1");Q3=makeQuery(id+"F2.boolean.opBoolean","MERGE",EDGE,{"derivedFrom":[makeQuery(id+"F1.opExtrude","SWEPT_EDGE",EDGE,{"disambiguationData":[OSD([subQ1,subQ0])]}),makeQuery(id+"F2.opExtrude","SWEPT_EDGE",EDGE,{"disambiguationData":[OSD([subQ1,subQ0])]})]});}
            fillet(context, id + "F3", {"entities" : qUnion([Q0, Q1, Q2, Q3]), "radius" : 5 * mm, "tangentPropagation" : true, "allowEdgeOverflow" : false});
        }
        {
            var Q0;
            Q0=makeQuery(id+"F2.opExtrude","CAP_FACE",FACE,{"disambiguationData":[OSD([sQuery(id+"F0.wireOp",EDGE,"E0"),sQuery(id+"F0.wireOp",EDGE,"E1"),sQuery(id+"F0.wireOp",EDGE,"E2"),sQuery(id+"F0.wireOp",EDGE,"E3"),sQuery(id+"F0.wireOp",EDGE,"E845"),sQuery(id+"F0.wireOp",EDGE,"E846"),sQuery(id+"F0.wireOp",EDGE,"E847"),sQuery(id+"F0.wireOp",EDGE,"E928.bottom"),sQuery(id+"F0.wireOp",EDGE,"E928.top"),sQuery(id+"F0.wireOp",EDGE,"E928.left"),sQuery(id+"F0.wireOp",EDGE,"E928.right"),sQuery(id+"F0.wireOp",EDGE,"E929.bottom"),sQuery(id+"F0.wireOp",EDGE,"E929.top"),sQuery(id+"F0.wireOp",EDGE,"E929.left"),sQuery(id+"F0.wireOp",EDGE,"E929.right"),sQuery(id+"F0.wireOp",EDGE,"E930.bottom"),sQuery(id+"F0.wireOp",EDGE,"E930.top"),sQuery(id+"F0.wireOp",EDGE,"E930.left"),sQuery(id+"F0.wireOp",EDGE,"E930.right"),sQuery(id+"F0.wireOp",EDGE,"E931.bottom"),sQuery(id+"F0.wireOp",EDGE,"E931.top"),sQuery(id+"F0.wireOp",EDGE,"E931.left"),sQuery(id+"F0.wireOp",EDGE,"E931.right"),sQuery(id+"F0.wireOp",EDGE,"E932.bottom"),sQuery(id+"F0.wireOp",EDGE,"E932.top"),sQuery(id+"F0.wireOp",EDGE,"E932.left"),sQuery(id+"F0.wireOp",EDGE,"E932.right"),sQuery(id+"F0.wireOp",EDGE,"E933.bottom"),sQuery(id+"F0.wireOp",EDGE,"E933.top"),sQuery(id+"F0.wireOp",EDGE,"E933.left"),sQuery(id+"F0.wireOp",EDGE,"E933.right"),sQuery(id+"F0.wireOp",EDGE,"E934.bottom"),sQuery(id+"F0.wireOp",EDGE,"E934.top"),sQuery(id+"F0.wireOp",EDGE,"E934.left"),sQuery(id+"F0.wireOp",EDGE,"E934.right"),sQuery(id+"F0.wireOp",EDGE,"E935.bottom"),sQuery(id+"F0.wireOp",EDGE,"E935.top"),sQuery(id+"F0.wireOp",EDGE,"E935.left"),sQuery(id+"F0.wireOp",EDGE,"E935.right"),sQuery(id+"F0.wireOp",EDGE,"E936.bottom"),sQuery(id+"F0.wireOp",EDGE,"E936.top"),sQuery(id+"F0.wireOp",EDGE,"E936.left"),sQuery(id+"F0.wireOp",EDGE,"E936.right"),sQuery(id+"F0.wireOp",EDGE,"E937.bottom"),sQuery(id+"F0.wireOp",EDGE,"E937.top"),sQuery(id+"F0.wireOp",EDGE,"E937.left"),sQuery(id+"F0.wireOp",EDGE,"E937.right"),sQuery(id+"F0.wireOp",EDGE,"E938.bottom"),sQuery(id+"F0.wireOp",EDGE,"E938.top"),sQuery(id+"F0.wireOp",EDGE,"E938.left"),sQuery(id+"F0.wireOp",EDGE,"E938.right"),sQuery(id+"F0.wireOp",EDGE,"E939.bottom"),sQuery(id+"F0.wireOp",EDGE,"E939.top"),sQuery(id+"F0.wireOp",EDGE,"E939.left"),sQuery(id+"F0.wireOp",EDGE,"E939.right"),sQuery(id+"F0.wireOp",EDGE,"E940.bottom"),sQuery(id+"F0.wireOp",EDGE,"E940.top"),sQuery(id+"F0.wireOp",EDGE,"E940.left"),sQuery(id+"F0.wireOp",EDGE,"E940.right"),sQuery(id+"F0.wireOp",EDGE,"E941.bottom"),sQuery(id+"F0.wireOp",EDGE,"E941.top"),sQuery(id+"F0.wireOp",EDGE,"E941.left"),sQuery(id+"F0.wireOp",EDGE,"E941.right"),sQuery(id+"F0.wireOp",EDGE,"E942.bottom"),sQuery(id+"F0.wireOp",EDGE,"E942.top"),sQuery(id+"F0.wireOp",EDGE,"E942.left"),sQuery(id+"F0.wireOp",EDGE,"E942.right"),sQuery(id+"F0.wireOp",EDGE,"E943.bottom"),sQuery(id+"F0.wireOp",EDGE,"E943.top"),sQuery(id+"F0.wireOp",EDGE,"E943.left"),sQuery(id+"F0.wireOp",EDGE,"E943.right"),sQuery(id+"F0.wireOp",EDGE,"E944.bottom"),sQuery(id+"F0.wireOp",EDGE,"E944.top"),sQuery(id+"F0.wireOp",EDGE,"E944.left"),sQuery(id+"F0.wireOp",EDGE,"E944.right"),sQuery(id+"F0.wireOp",EDGE,"E945.bottom"),sQuery(id+"F0.wireOp",EDGE,"E945.top"),sQuery(id+"F0.wireOp",EDGE,"E945.left"),sQuery(id+"F0.wireOp",EDGE,"E945.right"),sQuery(id+"F0.wireOp",EDGE,"E946.bottom"),sQuery(id+"F0.wireOp",EDGE,"E946.top"),sQuery(id+"F0.wireOp",EDGE,"E946.left"),sQuery(id+"F0.wireOp",EDGE,"E946.right"),sQuery(id+"F0.wireOp",EDGE,"E947.bottom"),sQuery(id+"F0.wireOp",EDGE,"E947.top"),sQuery(id+"F0.wireOp",EDGE,"E947.left"),sQuery(id+"F0.wireOp",EDGE,"E947.right"),sQuery(id+"F0.wireOp",EDGE,"E948.bottom"),sQuery(id+"F0.wireOp",EDGE,"E948.top"),sQuery(id+"F0.wireOp",EDGE,"E948.left"),sQuery(id+"F0.wireOp",EDGE,"E948.right"),sQuery(id+"F0.wireOp",EDGE,"E949.bottom"),sQuery(id+"F0.wireOp",EDGE,"E949.top"),sQuery(id+"F0.wireOp",EDGE,"E949.left"),sQuery(id+"F0.wireOp",EDGE,"E949.right"),sQuery(id+"F0.wireOp",EDGE,"E950.bottom"),sQuery(id+"F0.wireOp",EDGE,"E950.top"),sQuery(id+"F0.wireOp",EDGE,"E950.left"),sQuery(id+"F0.wireOp",EDGE,"E950.right"),sQuery(id+"F0.wireOp",EDGE,"E951.bottom"),sQuery(id+"F0.wireOp",EDGE,"E951.top"),sQuery(id+"F0.wireOp",EDGE,"E951.left"),sQuery(id+"F0.wireOp",EDGE,"E951.right"),sQuery(id+"F0.wireOp",EDGE,"E952.bottom"),sQuery(id+"F0.wireOp",EDGE,"E952.top"),sQuery(id+"F0.wireOp",EDGE,"E952.left"),sQuery(id+"F0.wireOp",EDGE,"E952.right"),sQuery(id+"F0.wireOp",EDGE,"E953.bottom"),sQuery(id+"F0.wireOp",EDGE,"E953.top"),sQuery(id+"F0.wireOp",EDGE,"E953.left"),sQuery(id+"F0.wireOp",EDGE,"E953.right"),sQuery(id+"F0.wireOp",EDGE,"E954.bottom"),sQuery(id+"F0.wireOp",EDGE,"E954.top"),sQuery(id+"F0.wireOp",EDGE,"E954.left"),sQuery(id+"F0.wireOp",EDGE,"E954.right"),sQuery(id+"F0.wireOp",EDGE,"E955.bottom"),sQuery(id+"F0.wireOp",EDGE,"E955.top"),sQuery(id+"F0.wireOp",EDGE,"E955.left"),sQuery(id+"F0.wireOp",EDGE,"E955.right"),sQuery(id+"F0.wireOp",EDGE,"E956.bottom"),sQuery(id+"F0.wireOp",EDGE,"E956.top"),sQuery(id+"F0.wireOp",EDGE,"E956.left"),sQuery(id+"F0.wireOp",EDGE,"E956.right"),sQuery(id+"F0.wireOp",EDGE,"E957.bottom"),sQuery(id+"F0.wireOp",EDGE,"E957.top"),sQuery(id+"F0.wireOp",EDGE,"E957.left"),sQuery(id+"F0.wireOp",EDGE,"E957.right"),sQuery(id+"F0.wireOp",EDGE,"E958.bottom"),sQuery(id+"F0.wireOp",EDGE,"E958.top"),sQuery(id+"F0.wireOp",EDGE,"E958.left"),sQuery(id+"F0.wireOp",EDGE,"E958.right"),sQuery(id+"F0.wireOp",EDGE,"E959.bottom"),sQuery(id+"F0.wireOp",EDGE,"E959.top"),sQuery(id+"F0.wireOp",EDGE,"E959.left"),sQuery(id+"F0.wireOp",EDGE,"E959.right"),sQuery(id+"F0.wireOp",EDGE,"E960.bottom"),sQuery(id+"F0.wireOp",EDGE,"E960.top"),sQuery(id+"F0.wireOp",EDGE,"E960.left"),sQuery(id+"F0.wireOp",EDGE,"E960.right"),sQuery(id+"F0.wireOp",EDGE,"E961.bottom"),sQuery(id+"F0.wireOp",EDGE,"E961.top"),sQuery(id+"F0.wireOp",EDGE,"E961.left"),sQuery(id+"F0.wireOp",EDGE,"E961.right"),sQuery(id+"F0.wireOp",EDGE,"E962.bottom"),sQuery(id+"F0.wireOp",EDGE,"E962.top"),sQuery(id+"F0.wireOp",EDGE,"E962.left"),sQuery(id+"F0.wireOp",EDGE,"E962.right"),sQuery(id+"F0.wireOp",EDGE,"E963.bottom"),sQuery(id+"F0.wireOp",EDGE,"E963.top"),sQuery(id+"F0.wireOp",EDGE,"E963.left"),sQuery(id+"F0.wireOp",EDGE,"E963.right"),sQuery(id+"F0.wireOp",EDGE,"E964.bottom"),sQuery(id+"F0.wireOp",EDGE,"E964.top"),sQuery(id+"F0.wireOp",EDGE,"E964.left"),sQuery(id+"F0.wireOp",EDGE,"E964.right"),sQuery(id+"F0.wireOp",EDGE,"E965.bottom"),sQuery(id+"F0.wireOp",EDGE,"E965.top"),sQuery(id+"F0.wireOp",EDGE,"E965.left"),sQuery(id+"F0.wireOp",EDGE,"E965.right"),sQuery(id+"F0.wireOp",EDGE,"E966.bottom"),sQuery(id+"F0.wireOp",EDGE,"E966.top"),sQuery(id+"F0.wireOp",EDGE,"E966.left"),sQuery(id+"F0.wireOp",EDGE,"E966.right"),sQuery(id+"F0.wireOp",EDGE,"E967.bottom"),sQuery(id+"F0.wireOp",EDGE,"E967.top"),sQuery(id+"F0.wireOp",EDGE,"E967.left"),sQuery(id+"F0.wireOp",EDGE,"E967.right"),sQuery(id+"F0.wireOp",EDGE,"E968.bottom"),sQuery(id+"F0.wireOp",EDGE,"E968.top"),sQuery(id+"F0.wireOp",EDGE,"E968.left"),sQuery(id+"F0.wireOp",EDGE,"E968.right"),sQuery(id+"F0.wireOp",EDGE,"E969.bottom"),sQuery(id+"F0.wireOp",EDGE,"E969.top"),sQuery(id+"F0.wireOp",EDGE,"E969.left"),sQuery(id+"F0.wireOp",EDGE,"E969.right"),sQuery(id+"F0.wireOp",EDGE,"E970.bottom"),sQuery(id+"F0.wireOp",EDGE,"E970.top"),sQuery(id+"F0.wireOp",EDGE,"E970.left"),sQuery(id+"F0.wireOp",EDGE,"E970.right")])],"isStart":false});
            var sketch = newSketch(context, id + "F4", { "sketchPlane" : qUnion([Q0])});
            skLineSegment(sketch, "E971", {"start": v(-88.23, 62.4) * mm, "end": v(-88.23, -70.68) * mm, "construction": true});
            skLineSegment(sketch, "E972", {"start": v(-95.44, -57.27) * mm, "end": v(100.01, -57.27) * mm, "construction": true});
            skCircle(sketch, "E973", {"center": v(-86.43, -55.47) * mm, "radius": 1.8 * mm});
            skCircle(sketch, "E974", {"center": v(-86.43, -55.47) * mm, "radius": 1 * mm});
            skLineSegment(sketch, "E975", {"start": v(88.23, 63.56) * mm, "end": v(88.23, -70.44) * mm, "construction": true});
            skLineSegment(sketch, "E976", {"start": v(-93.88, 57.27) * mm, "end": v(102.3, 57.27) * mm, "construction": true});
            skCircle(sketch, "E977", {"center": v(86.43, -55.47) * mm, "radius": 1.8 * mm});
            skCircle(sketch, "E978", {"center": v(86.43, -55.47) * mm, "radius": 1 * mm});
            skCircle(sketch, "E979", {"center": v(86.43, 55.47) * mm, "radius": 1.8 * mm});
            skCircle(sketch, "E980", {"center": v(86.43, 55.47) * mm, "radius": 1 * mm});
            skCircle(sketch, "E981", {"center": v(-86.43, 55.47) * mm, "radius": 1.8 * mm});
            skCircle(sketch, "E982", {"center": v(-86.43, 55.47) * mm, "radius": 1 * mm});
            skLineSegment(sketch, "E983", {"start": v(-13.52, 7.15) * mm, "end": v(16.13, 7.15) * mm, "construction": true});
            skCircle(sketch, "E984", {"center": v(0, 7.15) * mm, "radius": 1.8 * mm});
            skCircle(sketch, "E985", {"center": v(0, 7.15) * mm, "radius": 1 * mm});
            skCircle(sketch, "E986", {"center": v(47.63, -7.14) * mm, "radius": 1.8 * mm});
            skPoint(sketch, "E986.centerSnap0", {"position": v(45.9, -7.14) * mm});
            skCircle(sketch, "E987", {"center": v(47.63, -7.14) * mm, "radius": 1 * mm});
            skLineSegment(sketch, "E988", {"start": v(-96.84, 55.47) * mm, "end": v(98.86, 55.47) * mm, "construction": true});
            skCircle(sketch, "E989", {"center": v(-47.7, -2.38) * mm, "radius": 1.8 * mm});
            skPoint(sketch, "E989.centerSnap0", {"position": v(-49.35, -2.38) * mm});
            skLineSegment(sketch, "E990", {"start": v(-45.9, -0.66) * mm, "end": v(-45.9, -4.1) * mm, "construction": true});
            skCircle(sketch, "E991", {"center": v(-47.7, -2.38) * mm, "radius": 1 * mm});
            skLineSegment(sketch, "E992", {"start": v(-101.67, -55.47) * mm, "end": v(94.09, -55.47) * mm, "construction": true});
            skCircle(sketch, "E993", {"center": v(-47.7, 55.47) * mm, "radius": 1.8 * mm});
            skCircle(sketch, "E994", {"center": v(-47.7, 55.47) * mm, "radius": 1 * mm});
            skCircle(sketch, "E995", {"center": v(-47.7, -55.47) * mm, "radius": 1.8 * mm});
            skCircle(sketch, "E996", {"center": v(-47.7, -55.47) * mm, "radius": 1 * mm});
            skCircle(sketch, "E997", {"center": v(0, 55.47) * mm, "radius": 1.8 * mm});
            skCircle(sketch, "E998", {"center": v(0, 55.47) * mm, "radius": 1 * mm});
            skCircle(sketch, "E999", {"center": v(0, -55.47) * mm, "radius": 1.8 * mm});
            skPoint(sketch, "E999.centerSnap0", {"position": v(0, -59.77) * mm});
            skCircle(sketch, "E1000", {"center": v(0, -55.47) * mm, "radius": 1 * mm});
            skCircle(sketch, "E1001", {"center": v(47.63, 55.47) * mm, "radius": 1.8 * mm});
            skCircle(sketch, "E1002", {"center": v(47.63, 55.47) * mm, "radius": 1 * mm});
            skCircle(sketch, "E1003", {"center": v(47.63, -55.47) * mm, "radius": 1.8 * mm});
            skCircle(sketch, "E1004", {"center": v(47.63, -55.47) * mm, "radius": 1 * mm});
            skLineSegment(sketch, "E1005", {"start": v(-86.43, 64.95) * mm, "end": v(-86.43, -63.77) * mm, "construction": true});
            skLineSegment(sketch, "E1006", {"start": v(-81.83, 4.1) * mm, "end": v(-81.83, 0.66) * mm, "construction": true});
            skCircle(sketch, "E1007", {"center": v(-86.43, 2.38) * mm, "radius": 1.8 * mm});
            skPoint(sketch, "E1007.centerSnap0", {"position": v(-81.83, 2.38) * mm});
            skCircle(sketch, "E1008", {"center": v(-86.43, 2.38) * mm, "radius": 1 * mm});
            skLineSegment(sketch, "E1009", {"start": v(86.43, 64.29) * mm, "end": v(86.43, -64.23) * mm, "construction": true});
            skCircle(sketch, "E1010", {"center": v(86.43, 2.38) * mm, "radius": 1.8 * mm});
            skCircle(sketch, "E1011", {"center": v(86.43, 2.38) * mm, "radius": 1 * mm});
            skSolve(sketch);
        }
        {
            var Q0;
            Q0=makeQuery(id+"F4.imprint","IMPRINT",FACE,{"disambiguationData":[TD([[makeQuery(id+"F4.imprint","IMPRINT",EDGE,{"derivedFrom":sQuery(id+"F4.wireOp",EDGE,"E973")}),1.0]])]});
            var Q1;
            Q1=makeQuery(id+"F4.imprint","IMPRINT",FACE,{"disambiguationData":[TD([[makeQuery(id+"F4.imprint","IMPRINT",EDGE,{"derivedFrom":sQuery(id+"F4.wireOp",EDGE,"E981")}),1.0]])]});
            var Q2;
            Q2=makeQuery(id+"F4.imprint","IMPRINT",FACE,{"disambiguationData":[TD([[makeQuery(id+"F4.imprint","IMPRINT",EDGE,{"derivedFrom":sQuery(id+"F4.wireOp",EDGE,"E979")}),1.0]])]});
            var Q3;
            Q3=makeQuery(id+"F4.imprint","IMPRINT",FACE,{"disambiguationData":[TD([[makeQuery(id+"F4.imprint","IMPRINT",EDGE,{"derivedFrom":sQuery(id+"F4.wireOp",EDGE,"E977")}),1.0]])]});
            var Q4;
            Q4=makeQuery(id+"F4.imprint","IMPRINT",FACE,{"disambiguationData":[TD([[makeQuery(id+"F4.imprint","IMPRINT",EDGE,{"derivedFrom":sQuery(id+"F4.wireOp",EDGE,"E984")}),1.0]])]});
            var Q5;
            Q5=makeQuery(id+"F4.imprint","IMPRINT",FACE,{"disambiguationData":[TD([[makeQuery(id+"F4.imprint","IMPRINT",EDGE,{"derivedFrom":sQuery(id+"F4.wireOp",EDGE,"cNVPEYgd-NHac-0NUT-Bswb-2n5QcBwe0s6R")}),1.0]])]});
            var Q6;
            Q6=makeQuery(id+"F4.imprint","IMPRINT",FACE,{"disambiguationData":[TD([[makeQuery(id+"F4.imprint","IMPRINT",EDGE,{"derivedFrom":sQuery(id+"F4.wireOp",EDGE,"E987")}),-1.0]])]});
            var Q7;
            Q7=makeQuery(id+"F4.imprint","IMPRINT",FACE,{"disambiguationData":[TD([[makeQuery(id+"F4.imprint","IMPRINT",EDGE,{"derivedFrom":sQuery(id+"F4.wireOp",EDGE,"E997")}),1.0]])]});
            var Q8;
            Q8=makeQuery(id+"F4.imprint","IMPRINT",FACE,{"disambiguationData":[TD([[makeQuery(id+"F4.imprint","IMPRINT",EDGE,{"derivedFrom":sQuery(id+"F4.wireOp",EDGE,"E999")}),1.0]])]});
            var Q9;
            Q9=makeQuery(id+"F4.imprint","IMPRINT",FACE,{"disambiguationData":[TD([[makeQuery(id+"F4.imprint","IMPRINT",EDGE,{"derivedFrom":sQuery(id+"F4.wireOp",EDGE,"E991")}),-1.0]])]});
            var Q10;
            Q10=makeQuery(id+"F4.imprint","IMPRINT",FACE,{"disambiguationData":[TD([[makeQuery(id+"F4.imprint","IMPRINT",EDGE,{"derivedFrom":sQuery(id+"F4.wireOp",EDGE,"E1007")}),1.0]])]});
            var Q11;
            Q11=makeQuery(id+"F4.imprint","IMPRINT",FACE,{"disambiguationData":[TD([[makeQuery(id+"F4.imprint","IMPRINT",EDGE,{"derivedFrom":sQuery(id+"F4.wireOp",EDGE,"E1010")}),1.0]])]});
            extrude(context, id + "F5", {"entities" : qUnion([Q0, Q1, Q2, Q3, Q4, Q5, Q6, Q7, Q8, Q9, Q10, Q11]), "operationType" : NewBodyOperationType.REMOVE, "oppositeDirection" : true, "depth" : 1.5 * mm});
        }
        {
            var Q0;
            Q0=makeQuery(id+"F4.imprint","IMPRINT",FACE,{"disambiguationData":[TD([[makeQuery(id+"F4.imprint","IMPRINT",EDGE,{"derivedFrom":sQuery(id+"F4.wireOp",EDGE,"E978")}),1.0]])]});
            var Q1;
            Q1=makeQuery(id+"F4.imprint","IMPRINT",FACE,{"disambiguationData":[TD([[makeQuery(id+"F4.imprint","IMPRINT",EDGE,{"derivedFrom":sQuery(id+"F4.wireOp",EDGE,"E980")}),1.0]])]});
            var Q2;
            Q2=makeQuery(id+"F4.imprint","IMPRINT",FACE,{"disambiguationData":[TD([[makeQuery(id+"F4.imprint","IMPRINT",EDGE,{"derivedFrom":sQuery(id+"F4.wireOp",EDGE,"E982")}),1.0]])]});
            var Q3;
            Q3=makeQuery(id+"F4.imprint","IMPRINT",FACE,{"disambiguationData":[TD([[makeQuery(id+"F4.imprint","IMPRINT",EDGE,{"derivedFrom":sQuery(id+"F4.wireOp",EDGE,"E974")}),1.0]])]});
            var Q4;
            Q4=makeQuery(id+"F4.imprint","IMPRINT",FACE,{"disambiguationData":[TD([[makeQuery(id+"F4.imprint","IMPRINT",EDGE,{"derivedFrom":sQuery(id+"F4.wireOp",EDGE,"E985")}),1.0]])]});
            var Q5;
            Q5=makeQuery(id+"F4.imprint","IMPRINT",FACE,{"disambiguationData":[TD([[makeQuery(id+"F4.imprint","IMPRINT",EDGE,{"derivedFrom":sQuery(id+"F4.wireOp",EDGE,"ujkoGJg9-zatk-nCZ3-epMn-KVPZoMVvY8ag")}),1.0]])]});
            var Q6;
            Q6=makeQuery(id+"F4.imprint","IMPRINT",FACE,{"disambiguationData":[TD([[makeQuery(id+"F4.imprint","IMPRINT",EDGE,{"derivedFrom":sQuery(id+"F4.wireOp",EDGE,"E987")}),1.0]])]});
            var Q7;
            Q7=makeQuery(id+"F4.imprint","IMPRINT",FACE,{"disambiguationData":[TD([[makeQuery(id+"F4.imprint","IMPRINT",EDGE,{"derivedFrom":sQuery(id+"F4.wireOp",EDGE,"E998")}),1.0]])]});
            var Q8;
            Q8=makeQuery(id+"F4.imprint","IMPRINT",FACE,{"disambiguationData":[TD([[makeQuery(id+"F4.imprint","IMPRINT",EDGE,{"derivedFrom":sQuery(id+"F4.wireOp",EDGE,"E991")}),1.0]])]});
            var Q9;
            Q9=makeQuery(id+"F4.imprint","IMPRINT",FACE,{"disambiguationData":[TD([[makeQuery(id+"F4.imprint","IMPRINT",EDGE,{"derivedFrom":sQuery(id+"F4.wireOp",EDGE,"E1000")}),1.0]])]});
            var Q10;
            Q10=makeQuery(id+"F4.imprint","IMPRINT",FACE,{"disambiguationData":[TD([[makeQuery(id+"F4.imprint","IMPRINT",EDGE,{"derivedFrom":sQuery(id+"F4.wireOp",EDGE,"E1011")}),1.0]])]});
            var Q11;
            Q11=makeQuery(id+"F4.imprint","IMPRINT",FACE,{"disambiguationData":[TD([[makeQuery(id+"F4.imprint","IMPRINT",EDGE,{"derivedFrom":sQuery(id+"F4.wireOp",EDGE,"E1008")}),1.0]])]});
            extrude(context, id + "F6", {"entities" : qUnion([Q0, Q1, Q2, Q3, Q4, Q5, Q6, Q7, Q8, Q9, Q10, Q11]), "operationType" : NewBodyOperationType.REMOVE, "oppositeDirection" : true, "depth" : 3 * mm});
        }
    });
